annotation { "Feature Type Name" : "Feature", "Feature Type Description" : "" }
export const myFeature = defineFeature(function(context is Context, id is Id, definition is map)
    precondition{}
    {
        {
            var Q0;
            Q0=qCreatedBy(makeId("Front.planeOp"),FACE);
            var sketch = newSketch(context, id + "F0", { "sketchPlane" : qUnion([Q0])});
            skLineSegment(sketch, "E0.bottom", {"start": v(-63.5, 38.1) * mm, "end": v(63.5, 38.1) * mm});
            skLineSegment(sketch, "E0.top", {"start": v(-63.5, -38.1) * mm, "end": v(63.5, -38.1) * mm});
            skLineSegment(sketch, "E0.left", {"start": v(-63.5, 38.1) * mm, "end": v(-63.5, -38.1) * mm});
            skLineSegment(sketch, "E0.right", {"start": v(63.5, 38.1) * mm, "end": v(63.5, -38.1) * mm});
            skPoint(sketch, "E1", {"position": v(-57.15, 31.75) * mm});
            skPoint(sketch, "E2", {"position": v(57.15, 31.75) * mm});
            skPoint(sketch, "E3", {"position": v(57.15, -31.75) * mm});
            skPoint(sketch, "E4", {"position": v(-57.15, -31.75) * mm});
            skSolve(sketch);
        }
        {
            var Q0;
            Q0=makeQuery(id+"F0.imprint","IMPRINT",FACE,{"disambiguationData":[TD([[makeQuery(id+"F0.imprint","IMPRINT",EDGE,{"derivedFrom":sQuery(id+"F0.wireOp",EDGE,"E0.bottom")}),-1.0]])]});
            extrude(context, id + "F1", {"entities" : qUnion([Q0]), "depth" : 1.52 * mm});
        }
        {
            var Q0;
            Q0=makeQuery(id+"F1.opExtrude","CAP_FACE",FACE,{"disambiguationData":[OSD([sQuery(id+"F0.wireOp",EDGE,"E0.bottom"),sQuery(id+"F0.wireOp",EDGE,"E0.top"),sQuery(id+"F0.wireOp",EDGE,"E0.left"),sQuery(id+"F0.wireOp",EDGE,"E0.right")])],"isStart":false});
            var sketch = newSketch(context, id + "F2", { "sketchPlane" : qUnion([Q0])});
            skText(sketch, "E5", { "text": "DRIFTER II", "fontName": "OpenSans-Regular.ttf"});
            skLineSegment(sketch, "E6", {"start": v(0, 5.62) * mm, "end": v(0, -4.17) * mm, "construction": true});
            skText(sketch, "E7", { "text": "Rustler 36 designed by Holman and Pye", "fontName": "OpenSans-Regular.ttf"});
            skText(sketch, "E8", { "text": "Built by Orion Marine, Falmouth,England", "fontName": "OpenSans-Regular.ttf"});
            skText(sketch, "E9", { "text": "Fitted out by Paul Litton, Harold Greenslade\n", "fontName": "OpenSans-Regular.ttf"});
            skText(sketch, "E10", { "text": "and Walter Randolph to interior and \n\n", "fontName": "OpenSans-Regular.ttf"});
            skText(sketch, "E11", { "text": "extra rigging designs by Walter Randolph", "fontName": "OpenSans-Regular.ttf"});
            skText(sketch, "E12", { "text": "Launched August 1991", "fontName": "OpenSans-Regular.ttf"});
            skText(sketch, "E13", { "text": "Hull No. 40 - SSR 66775", "fontName": "OpenSans-Regular.ttf"});
            const initialGuessF2  = {"E5": [-0.02106, 0.02396, 1, 0, 0.00652], "E7": [-0.05139, 0.01598, 1, 0, 0.004], "E8": [-0.05248, 0.00799, 1, 0, 0.004], "E9": [-0.0566, 0, 1, 0, 0.004], "E10": [-0.04651, -0.00798, 1, 0, 0.00399], "E11": [-0.05278, -0.01595, 1, 0, 0.00399], "E12": [-0.02895, -0.03553, 1, 0, 0.00399], "E13": [-0.02999, -0.02756, 1, 0, 0.00399]};
            skSetInitialGuess(sketch, initialGuessF2);
            skSolve(sketch);
        }
        {
            var Q0;
            Q0=sQuery(id+"F0.wireOp",VERTEX,"E1");
            var Q1;
            Q1=sQuery(id+"F0.wireOp",VERTEX,"E2");
            var Q2;
            Q2=sQuery(id+"F0.wireOp",VERTEX,"E4");
            var Q3;
            Q3=sQuery(id+"F0.wireOp",VERTEX,"E3");
            var Q4;
            Q4=makeQuery(id+"F1.opExtrude","SWEPT_BODY",BODY,{"disambiguationData":[OSD([sQuery(id+"F0.wireOp",EDGE,"E0.bottom"),sQuery(id+"F0.wireOp",EDGE,"E0.top"),sQuery(id+"F0.wireOp",EDGE,"E0.left"),sQuery(id+"F0.wireOp",EDGE,"E0.right")])]});
            hole(context, id + "F3", {"style" : HoleStyle.SIMPLE, "endStyle" : HoleEndStyle.THROUGH, "oppositeDirection" : true, "holeDiameter" : 4 * mm, "isTappedThrough" : true, "tappedDepth" : 12.7 * mm, "tapClearance" : 0, "startFromSketch" : true, "locations" : qUnion([Q0, Q1, Q2, Q3]), "scope" : qUnion([Q4])});
        }
        {
            var Q0;
            Q0 = qSketchRegion(id + "F2", true);
            extrude(context, id + "F4", {"entities" : qUnion([Q0]), "oppositeDirection" : true, "offsetDistance" : 25.4 * mm, "depth" : 0.5 * mm});
        }
        {
            var Q0;
            Q0=makeQuery(id+"F4.opExtrude","SWEPT_BODY",BODY,{"disambiguationData":[OSD([sQuery(id+"F2.wireOp",EDGE,"E5.sketch_text.stroke-0"),sQuery(id+"F2.wireOp",EDGE,"E5.sketch_text.stroke-1"),sQuery(id+"F2.wireOp",EDGE,"E5.sketch_text.stroke-2"),sQuery(id+"F2.wireOp",EDGE,"E5.sketch_text.stroke-3"),sQuery(id+"F2.wireOp",EDGE,"E5.sketch_text.stroke-4"),sQuery(id+"F2.wireOp",EDGE,"E5.sketch_text.stroke-5"),sQuery(id+"F2.wireOp",EDGE,"E5.sketch_text.stroke-6"),sQuery(id+"F2.wireOp",EDGE,"E5.sketch_text.stroke-7"),sQuery(id+"F2.wireOp",EDGE,"E5.sketch_text.stroke-8"),sQuery(id+"F2.wireOp",EDGE,"E5.sketch_text.stroke-9"),sQuery(id+"F2.wireOp",EDGE,"E5.sketch_text.stroke-10"),sQuery(id+"F2.wireOp",EDGE,"E5.sketch_text.stroke-11"),sQuery(id+"F2.wireOp",EDGE,"E5.sketch_text.stroke-12"),sQuery(id+"F2.wireOp",EDGE,"E5.sketch_text.stroke-13")])]});
            var Q1;
            Q1=makeQuery(id+"F4.opExtrude","SWEPT_BODY",BODY,{"disambiguationData":[OSD([sQuery(id+"F2.wireOp",EDGE,"E13.sketch_text.stroke-246"),sQuery(id+"F2.wireOp",EDGE,"E13.sketch_text.stroke-247"),sQuery(id+"F2.wireOp",EDGE,"E13.sketch_text.stroke-248"),sQuery(id+"F2.wireOp",EDGE,"E13.sketch_text.stroke-249"),sQuery(id+"F2.wireOp",EDGE,"E13.sketch_text.stroke-250"),sQuery(id+"F2.wireOp",EDGE,"E13.sketch_text.stroke-251"),sQuery(id+"F2.wireOp",EDGE,"E13.sketch_text.stroke-252"),sQuery(id+"F2.wireOp",EDGE,"E13.sketch_text.stroke-253"),sQuery(id+"F2.wireOp",EDGE,"E13.sketch_text.stroke-254"),sQuery(id+"F2.wireOp",EDGE,"E13.sketch_text.stroke-255"),sQuery(id+"F2.wireOp",EDGE,"E13.sketch_text.stroke-256"),sQuery(id+"F2.wireOp",EDGE,"E13.sketch_text.stroke-257"),sQuery(id+"F2.wireOp",EDGE,"E13.sketch_text.stroke-258"),sQuery(id+"F2.wireOp",EDGE,"E13.sketch_text.stroke-259"),sQuery(id+"F2.wireOp",EDGE,"E13.sketch_text.stroke-260"),sQuery(id+"F2.wireOp",EDGE,"E13.sketch_text.stroke-261"),sQuery(id+"F2.wireOp",EDGE,"E13.sketch_text.stroke-262"),sQuery(id+"F2.wireOp",EDGE,"E13.sketch_text.stroke-263"),sQuery(id+"F2.wireOp",EDGE,"E13.sketch_text.stroke-264")])]});
            var Q2;
            Q2=makeQuery(id+"F4.opExtrude","SWEPT_BODY",BODY,{"disambiguationData":[OSD([sQuery(id+"F2.wireOp",EDGE,"E7.sketch_text.stroke-523"),sQuery(id+"F2.wireOp",EDGE,"E7.sketch_text.stroke-524"),sQuery(id+"F2.wireOp",EDGE,"E7.sketch_text.stroke-525"),sQuery(id+"F2.wireOp",EDGE,"E7.sketch_text.stroke-526"),sQuery(id+"F2.wireOp",EDGE,"E7.sketch_text.stroke-527"),sQuery(id+"F2.wireOp",EDGE,"E7.sketch_text.stroke-528"),sQuery(id+"F2.wireOp",EDGE,"E7.sketch_text.stroke-529"),sQuery(id+"F2.wireOp",EDGE,"E7.sketch_text.stroke-530"),sQuery(id+"F2.wireOp",EDGE,"E7.sketch_text.stroke-531"),sQuery(id+"F2.wireOp",EDGE,"E7.sketch_text.stroke-532"),sQuery(id+"F2.wireOp",EDGE,"E7.sketch_text.stroke-533"),sQuery(id+"F2.wireOp",EDGE,"E7.sketch_text.stroke-534"),sQuery(id+"F2.wireOp",EDGE,"E7.sketch_text.stroke-535"),sQuery(id+"F2.wireOp",EDGE,"E7.sketch_text.stroke-536"),sQuery(id+"F2.wireOp",EDGE,"E7.sketch_text.stroke-537"),sQuery(id+"F2.wireOp",EDGE,"E7.sketch_text.stroke-538"),sQuery(id+"F2.wireOp",EDGE,"E7.sketch_text.stroke-539")])]});
            var Q3;
            Q3=makeQuery(id+"F4.opExtrude","SWEPT_BODY",BODY,{"disambiguationData":[OSD([sQuery(id+"F2.wireOp",EDGE,"E7.sketch_text.stroke-540"),sQuery(id+"F2.wireOp",EDGE,"E7.sketch_text.stroke-541"),sQuery(id+"F2.wireOp",EDGE,"E7.sketch_text.stroke-542"),sQuery(id+"F2.wireOp",EDGE,"E7.sketch_text.stroke-543"),sQuery(id+"F2.wireOp",EDGE,"E7.sketch_text.stroke-544"),sQuery(id+"F2.wireOp",EDGE,"E7.sketch_text.stroke-545"),sQuery(id+"F2.wireOp",EDGE,"E7.sketch_text.stroke-546"),sQuery(id+"F2.wireOp",EDGE,"E7.sketch_text.stroke-547"),sQuery(id+"F2.wireOp",EDGE,"E7.sketch_text.stroke-548"),sQuery(id+"F2.wireOp",EDGE,"E7.sketch_text.stroke-549"),sQuery(id+"F2.wireOp",EDGE,"E7.sketch_text.stroke-550"),sQuery(id+"F2.wireOp",EDGE,"E7.sketch_text.stroke-551"),sQuery(id+"F2.wireOp",EDGE,"E7.sketch_text.stroke-552"),sQuery(id+"F2.wireOp",EDGE,"E7.sketch_text.stroke-553"),sQuery(id+"F2.wireOp",EDGE,"E7.sketch_text.stroke-554"),sQuery(id+"F2.wireOp",EDGE,"E7.sketch_text.stroke-555"),sQuery(id+"F2.wireOp",EDGE,"E7.sketch_text.stroke-556"),sQuery(id+"F2.wireOp",EDGE,"E7.sketch_text.stroke-557"),sQuery(id+"F2.wireOp",EDGE,"E7.sketch_text.stroke-558"),sQuery(id+"F2.wireOp",EDGE,"E7.sketch_text.stroke-559"),sQuery(id+"F2.wireOp",EDGE,"E7.sketch_text.stroke-560"),sQuery(id+"F2.wireOp",EDGE,"E7.sketch_text.stroke-561"),sQuery(id+"F2.wireOp",EDGE,"E7.sketch_text.stroke-562"),sQuery(id+"F2.wireOp",EDGE,"E7.sketch_text.stroke-563")])]});
            var Q4;
            Q4=makeQuery(id+"F4.opExtrude","SWEPT_BODY",BODY,{"disambiguationData":[OSD([sQuery(id+"F2.wireOp",EDGE,"E7.sketch_text.stroke-564"),sQuery(id+"F2.wireOp",EDGE,"E7.sketch_text.stroke-565"),sQuery(id+"F2.wireOp",EDGE,"E7.sketch_text.stroke-566"),sQuery(id+"F2.wireOp",EDGE,"E7.sketch_text.stroke-567"),sQuery(id+"F2.wireOp",EDGE,"E7.sketch_text.stroke-568"),sQuery(id+"F2.wireOp",EDGE,"E7.sketch_text.stroke-569"),sQuery(id+"F2.wireOp",EDGE,"E7.sketch_text.stroke-570"),sQuery(id+"F2.wireOp",EDGE,"E7.sketch_text.stroke-571"),sQuery(id+"F2.wireOp",EDGE,"E7.sketch_text.stroke-572"),sQuery(id+"F2.wireOp",EDGE,"E7.sketch_text.stroke-573"),sQuery(id+"F2.wireOp",EDGE,"E7.sketch_text.stroke-574"),sQuery(id+"F2.wireOp",EDGE,"E7.sketch_text.stroke-575"),sQuery(id+"F2.wireOp",EDGE,"E7.sketch_text.stroke-576"),sQuery(id+"F2.wireOp",EDGE,"E7.sketch_text.stroke-577"),sQuery(id+"F2.wireOp",EDGE,"E7.sketch_text.stroke-578")])]});
            var Q5;
            Q5=makeQuery(id+"F4.opExtrude","SWEPT_BODY",BODY,{"disambiguationData":[OSD([sQuery(id+"F2.wireOp",EDGE,"E7.sketch_text.stroke-579"),sQuery(id+"F2.wireOp",EDGE,"E7.sketch_text.stroke-580"),sQuery(id+"F2.wireOp",EDGE,"E7.sketch_text.stroke-581"),sQuery(id+"F2.wireOp",EDGE,"E7.sketch_text.stroke-582"),sQuery(id+"F2.wireOp",EDGE,"E7.sketch_text.stroke-583"),sQuery(id+"F2.wireOp",EDGE,"E7.sketch_text.stroke-584"),sQuery(id+"F2.wireOp",EDGE,"E7.sketch_text.stroke-585"),sQuery(id+"F2.wireOp",EDGE,"E7.sketch_text.stroke-586"),sQuery(id+"F2.wireOp",EDGE,"E7.sketch_text.stroke-587"),sQuery(id+"F2.wireOp",EDGE,"E7.sketch_text.stroke-588"),sQuery(id+"F2.wireOp",EDGE,"E7.sketch_text.stroke-589"),sQuery(id+"F2.wireOp",EDGE,"E7.sketch_text.stroke-590"),sQuery(id+"F2.wireOp",EDGE,"E7.sketch_text.stroke-591"),sQuery(id+"F2.wireOp",EDGE,"E7.sketch_text.stroke-592"),sQuery(id+"F2.wireOp",EDGE,"E7.sketch_text.stroke-593"),sQuery(id+"F2.wireOp",EDGE,"E7.sketch_text.stroke-594")])]});
            var Q6;
            Q6=makeQuery(id+"F4.opExtrude","SWEPT_BODY",BODY,{"disambiguationData":[OSD([sQuery(id+"F2.wireOp",EDGE,"E7.sketch_text.stroke-595"),sQuery(id+"F2.wireOp",EDGE,"E7.sketch_text.stroke-596"),sQuery(id+"F2.wireOp",EDGE,"E7.sketch_text.stroke-597"),sQuery(id+"F2.wireOp",EDGE,"E7.sketch_text.stroke-598"),sQuery(id+"F2.wireOp",EDGE,"E7.sketch_text.stroke-599"),sQuery(id+"F2.wireOp",EDGE,"E7.sketch_text.stroke-600"),sQuery(id+"F2.wireOp",EDGE,"E7.sketch_text.stroke-601"),sQuery(id+"F2.wireOp",EDGE,"E7.sketch_text.stroke-602"),sQuery(id+"F2.wireOp",EDGE,"E7.sketch_text.stroke-603"),sQuery(id+"F2.wireOp",EDGE,"E7.sketch_text.stroke-604"),sQuery(id+"F2.wireOp",EDGE,"E7.sketch_text.stroke-605"),sQuery(id+"F2.wireOp",EDGE,"E7.sketch_text.stroke-606"),sQuery(id+"F2.wireOp",EDGE,"E7.sketch_text.stroke-607"),sQuery(id+"F2.wireOp",EDGE,"E7.sketch_text.stroke-608"),sQuery(id+"F2.wireOp",EDGE,"E7.sketch_text.stroke-609"),sQuery(id+"F2.wireOp",EDGE,"E7.sketch_text.stroke-610"),sQuery(id+"F2.wireOp",EDGE,"E7.sketch_text.stroke-611"),sQuery(id+"F2.wireOp",EDGE,"E7.sketch_text.stroke-612"),sQuery(id+"F2.wireOp",EDGE,"E7.sketch_text.stroke-613")])]});
            var Q7;
            Q7=makeQuery(id+"F4.opExtrude","SWEPT_BODY",BODY,{"disambiguationData":[OSD([sQuery(id+"F2.wireOp",EDGE,"E8.sketch_text.stroke-0"),sQuery(id+"F2.wireOp",EDGE,"E8.sketch_text.stroke-1"),sQuery(id+"F2.wireOp",EDGE,"E8.sketch_text.stroke-2"),sQuery(id+"F2.wireOp",EDGE,"E8.sketch_text.stroke-3"),sQuery(id+"F2.wireOp",EDGE,"E8.sketch_text.stroke-4"),sQuery(id+"F2.wireOp",EDGE,"E8.sketch_text.stroke-5"),sQuery(id+"F2.wireOp",EDGE,"E8.sketch_text.stroke-6"),sQuery(id+"F2.wireOp",EDGE,"E8.sketch_text.stroke-7"),sQuery(id+"F2.wireOp",EDGE,"E8.sketch_text.stroke-8"),sQuery(id+"F2.wireOp",EDGE,"E8.sketch_text.stroke-9"),sQuery(id+"F2.wireOp",EDGE,"E8.sketch_text.stroke-10"),sQuery(id+"F2.wireOp",EDGE,"E8.sketch_text.stroke-11"),sQuery(id+"F2.wireOp",EDGE,"E8.sketch_text.stroke-12"),sQuery(id+"F2.wireOp",EDGE,"E8.sketch_text.stroke-13"),sQuery(id+"F2.wireOp",EDGE,"E8.sketch_text.stroke-14"),sQuery(id+"F2.wireOp",EDGE,"E8.sketch_text.stroke-15"),sQuery(id+"F2.wireOp",EDGE,"E8.sketch_text.stroke-16"),sQuery(id+"F2.wireOp",EDGE,"E8.sketch_text.stroke-17"),sQuery(id+"F2.wireOp",EDGE,"E8.sketch_text.stroke-18"),sQuery(id+"F2.wireOp",EDGE,"E8.sketch_text.stroke-19"),sQuery(id+"F2.wireOp",EDGE,"E8.sketch_text.stroke-20"),sQuery(id+"F2.wireOp",EDGE,"E8.sketch_text.stroke-21"),sQuery(id+"F2.wireOp",EDGE,"E8.sketch_text.stroke-22"),sQuery(id+"F2.wireOp",EDGE,"E8.sketch_text.stroke-23"),sQuery(id+"F2.wireOp",EDGE,"E8.sketch_text.stroke-24")])]});
            var Q8;
            Q8=makeQuery(id+"F4.opExtrude","SWEPT_BODY",BODY,{"disambiguationData":[OSD([sQuery(id+"F2.wireOp",EDGE,"E8.sketch_text.stroke-25"),sQuery(id+"F2.wireOp",EDGE,"E8.sketch_text.stroke-26"),sQuery(id+"F2.wireOp",EDGE,"E8.sketch_text.stroke-27"),sQuery(id+"F2.wireOp",EDGE,"E8.sketch_text.stroke-28"),sQuery(id+"F2.wireOp",EDGE,"E8.sketch_text.stroke-29"),sQuery(id+"F2.wireOp",EDGE,"E8.sketch_text.stroke-30"),sQuery(id+"F2.wireOp",EDGE,"E8.sketch_text.stroke-31"),sQuery(id+"F2.wireOp",EDGE,"E8.sketch_text.stroke-32"),sQuery(id+"F2.wireOp",EDGE,"E8.sketch_text.stroke-33"),sQuery(id+"F2.wireOp",EDGE,"E8.sketch_text.stroke-34"),sQuery(id+"F2.wireOp",EDGE,"E8.sketch_text.stroke-35"),sQuery(id+"F2.wireOp",EDGE,"E8.sketch_text.stroke-36"),sQuery(id+"F2.wireOp",EDGE,"E8.sketch_text.stroke-37"),sQuery(id+"F2.wireOp",EDGE,"E8.sketch_text.stroke-38"),sQuery(id+"F2.wireOp",EDGE,"E8.sketch_text.stroke-39"),sQuery(id+"F2.wireOp",EDGE,"E8.sketch_text.stroke-40"),sQuery(id+"F2.wireOp",EDGE,"E8.sketch_text.stroke-41")])]});
            var Q9;
            Q9=makeQuery(id+"F4.opExtrude","SWEPT_BODY",BODY,{"disambiguationData":[OSD([sQuery(id+"F2.wireOp",EDGE,"E8.sketch_text.stroke-42"),sQuery(id+"F2.wireOp",EDGE,"E8.sketch_text.stroke-43"),sQuery(id+"F2.wireOp",EDGE,"E8.sketch_text.stroke-44"),sQuery(id+"F2.wireOp",EDGE,"E8.sketch_text.stroke-45")])]});
            var Q10;
            Q10=makeQuery(id+"F4.opExtrude","SWEPT_BODY",BODY,{"disambiguationData":[OSD([sQuery(id+"F2.wireOp",EDGE,"E8.sketch_text.stroke-46"),sQuery(id+"F2.wireOp",EDGE,"E8.sketch_text.stroke-47"),sQuery(id+"F2.wireOp",EDGE,"E8.sketch_text.stroke-48"),sQuery(id+"F2.wireOp",EDGE,"E8.sketch_text.stroke-49"),sQuery(id+"F2.wireOp",EDGE,"E8.sketch_text.stroke-50"),sQuery(id+"F2.wireOp",EDGE,"E8.sketch_text.stroke-51"),sQuery(id+"F2.wireOp",EDGE,"E8.sketch_text.stroke-52"),sQuery(id+"F2.wireOp",EDGE,"E8.sketch_text.stroke-53")])]});
            var Q11;
            Q11=makeQuery(id+"F4.opExtrude","SWEPT_BODY",BODY,{"disambiguationData":[OSD([sQuery(id+"F2.wireOp",EDGE,"E8.sketch_text.stroke-54"),sQuery(id+"F2.wireOp",EDGE,"E8.sketch_text.stroke-55"),sQuery(id+"F2.wireOp",EDGE,"E8.sketch_text.stroke-56"),sQuery(id+"F2.wireOp",EDGE,"E8.sketch_text.stroke-57")])]});
            var Q12;
            Q12=makeQuery(id+"F4.opExtrude","SWEPT_BODY",BODY,{"disambiguationData":[OSD([sQuery(id+"F2.wireOp",EDGE,"E8.sketch_text.stroke-58"),sQuery(id+"F2.wireOp",EDGE,"E8.sketch_text.stroke-59"),sQuery(id+"F2.wireOp",EDGE,"E8.sketch_text.stroke-60"),sQuery(id+"F2.wireOp",EDGE,"E8.sketch_text.stroke-61"),sQuery(id+"F2.wireOp",EDGE,"E8.sketch_text.stroke-62"),sQuery(id+"F2.wireOp",EDGE,"E8.sketch_text.stroke-63"),sQuery(id+"F2.wireOp",EDGE,"E8.sketch_text.stroke-64"),sQuery(id+"F2.wireOp",EDGE,"E8.sketch_text.stroke-65"),sQuery(id+"F2.wireOp",EDGE,"E8.sketch_text.stroke-66"),sQuery(id+"F2.wireOp",EDGE,"E8.sketch_text.stroke-67"),sQuery(id+"F2.wireOp",EDGE,"E8.sketch_text.stroke-68"),sQuery(id+"F2.wireOp",EDGE,"E8.sketch_text.stroke-69"),sQuery(id+"F2.wireOp",EDGE,"E8.sketch_text.stroke-70"),sQuery(id+"F2.wireOp",EDGE,"E8.sketch_text.stroke-71"),sQuery(id+"F2.wireOp",EDGE,"E8.sketch_text.stroke-72"),sQuery(id+"F2.wireOp",EDGE,"E8.sketch_text.stroke-73"),sQuery(id+"F2.wireOp",EDGE,"E8.sketch_text.stroke-74"),sQuery(id+"F2.wireOp",EDGE,"E8.sketch_text.stroke-75"),sQuery(id+"F2.wireOp",EDGE,"E8.sketch_text.stroke-76")])]});
            var Q13;
            Q13=makeQuery(id+"F4.opExtrude","SWEPT_BODY",BODY,{"disambiguationData":[OSD([sQuery(id+"F2.wireOp",EDGE,"E8.sketch_text.stroke-77"),sQuery(id+"F2.wireOp",EDGE,"E8.sketch_text.stroke-78"),sQuery(id+"F2.wireOp",EDGE,"E8.sketch_text.stroke-79"),sQuery(id+"F2.wireOp",EDGE,"E8.sketch_text.stroke-80"),sQuery(id+"F2.wireOp",EDGE,"E8.sketch_text.stroke-81"),sQuery(id+"F2.wireOp",EDGE,"E8.sketch_text.stroke-82"),sQuery(id+"F2.wireOp",EDGE,"E8.sketch_text.stroke-83"),sQuery(id+"F2.wireOp",EDGE,"E8.sketch_text.stroke-84"),sQuery(id+"F2.wireOp",EDGE,"E8.sketch_text.stroke-85"),sQuery(id+"F2.wireOp",EDGE,"E8.sketch_text.stroke-86"),sQuery(id+"F2.wireOp",EDGE,"E8.sketch_text.stroke-87"),sQuery(id+"F2.wireOp",EDGE,"E8.sketch_text.stroke-88"),sQuery(id+"F2.wireOp",EDGE,"E8.sketch_text.stroke-89"),sQuery(id+"F2.wireOp",EDGE,"E8.sketch_text.stroke-90"),sQuery(id+"F2.wireOp",EDGE,"E8.sketch_text.stroke-91"),sQuery(id+"F2.wireOp",EDGE,"E8.sketch_text.stroke-92"),sQuery(id+"F2.wireOp",EDGE,"E8.sketch_text.stroke-93"),sQuery(id+"F2.wireOp",EDGE,"E8.sketch_text.stroke-94"),sQuery(id+"F2.wireOp",EDGE,"E8.sketch_text.stroke-95"),sQuery(id+"F2.wireOp",EDGE,"E8.sketch_text.stroke-96"),sQuery(id+"F2.wireOp",EDGE,"E8.sketch_text.stroke-97"),sQuery(id+"F2.wireOp",EDGE,"E8.sketch_text.stroke-98"),sQuery(id+"F2.wireOp",EDGE,"E8.sketch_text.stroke-99")])]});
            var Q14;
            Q14=makeQuery(id+"F4.opExtrude","SWEPT_BODY",BODY,{"disambiguationData":[OSD([sQuery(id+"F2.wireOp",EDGE,"E8.sketch_text.stroke-100"),sQuery(id+"F2.wireOp",EDGE,"E8.sketch_text.stroke-101"),sQuery(id+"F2.wireOp",EDGE,"E8.sketch_text.stroke-102"),sQuery(id+"F2.wireOp",EDGE,"E8.sketch_text.stroke-103"),sQuery(id+"F2.wireOp",EDGE,"E8.sketch_text.stroke-104"),sQuery(id+"F2.wireOp",EDGE,"E8.sketch_text.stroke-105"),sQuery(id+"F2.wireOp",EDGE,"E8.sketch_text.stroke-106"),sQuery(id+"F2.wireOp",EDGE,"E8.sketch_text.stroke-107"),sQuery(id+"F2.wireOp",EDGE,"E8.sketch_text.stroke-108"),sQuery(id+"F2.wireOp",EDGE,"E8.sketch_text.stroke-109"),sQuery(id+"F2.wireOp",EDGE,"E8.sketch_text.stroke-110"),sQuery(id+"F2.wireOp",EDGE,"E8.sketch_text.stroke-111"),sQuery(id+"F2.wireOp",EDGE,"E8.sketch_text.stroke-112"),sQuery(id+"F2.wireOp",EDGE,"E8.sketch_text.stroke-113"),sQuery(id+"F2.wireOp",EDGE,"E8.sketch_text.stroke-114"),sQuery(id+"F2.wireOp",EDGE,"E8.sketch_text.stroke-115")])]});
            var Q15;
            Q15=makeQuery(id+"F4.opExtrude","SWEPT_BODY",BODY,{"disambiguationData":[OSD([sQuery(id+"F2.wireOp",EDGE,"E8.sketch_text.stroke-116"),sQuery(id+"F2.wireOp",EDGE,"E8.sketch_text.stroke-117"),sQuery(id+"F2.wireOp",EDGE,"E8.sketch_text.stroke-118"),sQuery(id+"F2.wireOp",EDGE,"E8.sketch_text.stroke-119"),sQuery(id+"F2.wireOp",EDGE,"E8.sketch_text.stroke-120"),sQuery(id+"F2.wireOp",EDGE,"E8.sketch_text.stroke-121"),sQuery(id+"F2.wireOp",EDGE,"E8.sketch_text.stroke-122"),sQuery(id+"F2.wireOp",EDGE,"E8.sketch_text.stroke-123"),sQuery(id+"F2.wireOp",EDGE,"E8.sketch_text.stroke-124"),sQuery(id+"F2.wireOp",EDGE,"E8.sketch_text.stroke-125"),sQuery(id+"F2.wireOp",EDGE,"E8.sketch_text.stroke-126"),sQuery(id+"F2.wireOp",EDGE,"E8.sketch_text.stroke-127"),sQuery(id+"F2.wireOp",EDGE,"E8.sketch_text.stroke-128"),sQuery(id+"F2.wireOp",EDGE,"E8.sketch_text.stroke-129"),sQuery(id+"F2.wireOp",EDGE,"E8.sketch_text.stroke-130"),sQuery(id+"F2.wireOp",EDGE,"E8.sketch_text.stroke-131")])]});
            var Q16;
            Q16=makeQuery(id+"F4.opExtrude","SWEPT_BODY",BODY,{"disambiguationData":[OSD([sQuery(id+"F2.wireOp",EDGE,"E8.sketch_text.stroke-132"),sQuery(id+"F2.wireOp",EDGE,"E8.sketch_text.stroke-133"),sQuery(id+"F2.wireOp",EDGE,"E8.sketch_text.stroke-134"),sQuery(id+"F2.wireOp",EDGE,"E8.sketch_text.stroke-135"),sQuery(id+"F2.wireOp",EDGE,"E8.sketch_text.stroke-136"),sQuery(id+"F2.wireOp",EDGE,"E8.sketch_text.stroke-137"),sQuery(id+"F2.wireOp",EDGE,"E8.sketch_text.stroke-138"),sQuery(id+"F2.wireOp",EDGE,"E8.sketch_text.stroke-139"),sQuery(id+"F2.wireOp",EDGE,"E8.sketch_text.stroke-140"),sQuery(id+"F2.wireOp",EDGE,"E8.sketch_text.stroke-141"),sQuery(id+"F2.wireOp",EDGE,"E8.sketch_text.stroke-142"),sQuery(id+"F2.wireOp",EDGE,"E8.sketch_text.stroke-143"),sQuery(id+"F2.wireOp",EDGE,"E8.sketch_text.stroke-144")])]});
            var Q17;
            Q17=makeQuery(id+"F4.opExtrude","SWEPT_BODY",BODY,{"disambiguationData":[OSD([sQuery(id+"F2.wireOp",EDGE,"E8.sketch_text.stroke-145"),sQuery(id+"F2.wireOp",EDGE,"E8.sketch_text.stroke-146"),sQuery(id+"F2.wireOp",EDGE,"E8.sketch_text.stroke-147"),sQuery(id+"F2.wireOp",EDGE,"E8.sketch_text.stroke-148")])]});
            var Q18;
            Q18=makeQuery(id+"F4.opExtrude","SWEPT_BODY",BODY,{"disambiguationData":[OSD([sQuery(id+"F2.wireOp",EDGE,"E8.sketch_text.stroke-149"),sQuery(id+"F2.wireOp",EDGE,"E8.sketch_text.stroke-150"),sQuery(id+"F2.wireOp",EDGE,"E8.sketch_text.stroke-151"),sQuery(id+"F2.wireOp",EDGE,"E8.sketch_text.stroke-152"),sQuery(id+"F2.wireOp",EDGE,"E8.sketch_text.stroke-153"),sQuery(id+"F2.wireOp",EDGE,"E8.sketch_text.stroke-154"),sQuery(id+"F2.wireOp",EDGE,"E8.sketch_text.stroke-155"),sQuery(id+"F2.wireOp",EDGE,"E8.sketch_text.stroke-156")])]});
            var Q19;
            Q19=makeQuery(id+"F4.opExtrude","SWEPT_BODY",BODY,{"disambiguationData":[OSD([sQuery(id+"F2.wireOp",EDGE,"E8.sketch_text.stroke-157"),sQuery(id+"F2.wireOp",EDGE,"E8.sketch_text.stroke-158"),sQuery(id+"F2.wireOp",EDGE,"E8.sketch_text.stroke-159"),sQuery(id+"F2.wireOp",EDGE,"E8.sketch_text.stroke-160"),sQuery(id+"F2.wireOp",EDGE,"E8.sketch_text.stroke-161"),sQuery(id+"F2.wireOp",EDGE,"E8.sketch_text.stroke-162"),sQuery(id+"F2.wireOp",EDGE,"E8.sketch_text.stroke-163"),sQuery(id+"F2.wireOp",EDGE,"E8.sketch_text.stroke-164"),sQuery(id+"F2.wireOp",EDGE,"E8.sketch_text.stroke-165"),sQuery(id+"F2.wireOp",EDGE,"E8.sketch_text.stroke-166"),sQuery(id+"F2.wireOp",EDGE,"E8.sketch_text.stroke-167"),sQuery(id+"F2.wireOp",EDGE,"E8.sketch_text.stroke-168"),sQuery(id+"F2.wireOp",EDGE,"E8.sketch_text.stroke-169"),sQuery(id+"F2.wireOp",EDGE,"E8.sketch_text.stroke-170"),sQuery(id+"F2.wireOp",EDGE,"E8.sketch_text.stroke-171"),sQuery(id+"F2.wireOp",EDGE,"E8.sketch_text.stroke-172"),sQuery(id+"F2.wireOp",EDGE,"E8.sketch_text.stroke-173")])]});
            var Q20;
            Q20=makeQuery(id+"F4.opExtrude","SWEPT_BODY",BODY,{"disambiguationData":[OSD([sQuery(id+"F2.wireOp",EDGE,"E8.sketch_text.stroke-174"),sQuery(id+"F2.wireOp",EDGE,"E8.sketch_text.stroke-175"),sQuery(id+"F2.wireOp",EDGE,"E8.sketch_text.stroke-176"),sQuery(id+"F2.wireOp",EDGE,"E8.sketch_text.stroke-177"),sQuery(id+"F2.wireOp",EDGE,"E8.sketch_text.stroke-178"),sQuery(id+"F2.wireOp",EDGE,"E8.sketch_text.stroke-179"),sQuery(id+"F2.wireOp",EDGE,"E8.sketch_text.stroke-180"),sQuery(id+"F2.wireOp",EDGE,"E8.sketch_text.stroke-181"),sQuery(id+"F2.wireOp",EDGE,"E8.sketch_text.stroke-182"),sQuery(id+"F2.wireOp",EDGE,"E8.sketch_text.stroke-183"),sQuery(id+"F2.wireOp",EDGE,"E8.sketch_text.stroke-184"),sQuery(id+"F2.wireOp",EDGE,"E8.sketch_text.stroke-185"),sQuery(id+"F2.wireOp",EDGE,"E8.sketch_text.stroke-186"),sQuery(id+"F2.wireOp",EDGE,"E8.sketch_text.stroke-187"),sQuery(id+"F2.wireOp",EDGE,"E8.sketch_text.stroke-188"),sQuery(id+"F2.wireOp",EDGE,"E8.sketch_text.stroke-189"),sQuery(id+"F2.wireOp",EDGE,"E8.sketch_text.stroke-190")])]});
            var Q21;
            Q21=makeQuery(id+"F4.opExtrude","SWEPT_BODY",BODY,{"disambiguationData":[OSD([sQuery(id+"F2.wireOp",EDGE,"E8.sketch_text.stroke-191"),sQuery(id+"F2.wireOp",EDGE,"E8.sketch_text.stroke-192"),sQuery(id+"F2.wireOp",EDGE,"E8.sketch_text.stroke-193"),sQuery(id+"F2.wireOp",EDGE,"E8.sketch_text.stroke-194"),sQuery(id+"F2.wireOp",EDGE,"E8.sketch_text.stroke-195"),sQuery(id+"F2.wireOp",EDGE,"E8.sketch_text.stroke-196"),sQuery(id+"F2.wireOp",EDGE,"E8.sketch_text.stroke-197"),sQuery(id+"F2.wireOp",EDGE,"E8.sketch_text.stroke-198"),sQuery(id+"F2.wireOp",EDGE,"E8.sketch_text.stroke-199"),sQuery(id+"F2.wireOp",EDGE,"E8.sketch_text.stroke-200"),sQuery(id+"F2.wireOp",EDGE,"E8.sketch_text.stroke-201"),sQuery(id+"F2.wireOp",EDGE,"E8.sketch_text.stroke-202"),sQuery(id+"F2.wireOp",EDGE,"E8.sketch_text.stroke-203"),sQuery(id+"F2.wireOp",EDGE,"E8.sketch_text.stroke-204"),sQuery(id+"F2.wireOp",EDGE,"E8.sketch_text.stroke-205"),sQuery(id+"F2.wireOp",EDGE,"E8.sketch_text.stroke-206"),sQuery(id+"F2.wireOp",EDGE,"E8.sketch_text.stroke-207"),sQuery(id+"F2.wireOp",EDGE,"E8.sketch_text.stroke-208")])]});
            var Q22;
            Q22=makeQuery(id+"F4.opExtrude","SWEPT_BODY",BODY,{"disambiguationData":[OSD([sQuery(id+"F2.wireOp",EDGE,"E8.sketch_text.stroke-209"),sQuery(id+"F2.wireOp",EDGE,"E8.sketch_text.stroke-210"),sQuery(id+"F2.wireOp",EDGE,"E8.sketch_text.stroke-211"),sQuery(id+"F2.wireOp",EDGE,"E8.sketch_text.stroke-212"),sQuery(id+"F2.wireOp",EDGE,"E8.sketch_text.stroke-213"),sQuery(id+"F2.wireOp",EDGE,"E8.sketch_text.stroke-214"),sQuery(id+"F2.wireOp",EDGE,"E8.sketch_text.stroke-215"),sQuery(id+"F2.wireOp",EDGE,"E8.sketch_text.stroke-216"),sQuery(id+"F2.wireOp",EDGE,"E8.sketch_text.stroke-217"),sQuery(id+"F2.wireOp",EDGE,"E8.sketch_text.stroke-218"),sQuery(id+"F2.wireOp",EDGE,"E8.sketch_text.stroke-219"),sQuery(id+"F2.wireOp",EDGE,"E8.sketch_text.stroke-220"),sQuery(id+"F2.wireOp",EDGE,"E8.sketch_text.stroke-221"),sQuery(id+"F2.wireOp",EDGE,"E8.sketch_text.stroke-222"),sQuery(id+"F2.wireOp",EDGE,"E8.sketch_text.stroke-223"),sQuery(id+"F2.wireOp",EDGE,"E8.sketch_text.stroke-224"),sQuery(id+"F2.wireOp",EDGE,"E8.sketch_text.stroke-225"),sQuery(id+"F2.wireOp",EDGE,"E8.sketch_text.stroke-226"),sQuery(id+"F2.wireOp",EDGE,"E8.sketch_text.stroke-227"),sQuery(id+"F2.wireOp",EDGE,"E8.sketch_text.stroke-228"),sQuery(id+"F2.wireOp",EDGE,"E8.sketch_text.stroke-229"),sQuery(id+"F2.wireOp",EDGE,"E8.sketch_text.stroke-230"),sQuery(id+"F2.wireOp",EDGE,"E8.sketch_text.stroke-231"),sQuery(id+"F2.wireOp",EDGE,"E8.sketch_text.stroke-232"),sQuery(id+"F2.wireOp",EDGE,"E8.sketch_text.stroke-233"),sQuery(id+"F2.wireOp",EDGE,"E8.sketch_text.stroke-234"),sQuery(id+"F2.wireOp",EDGE,"E8.sketch_text.stroke-235")])]});
            var Q23;
            Q23=makeQuery(id+"F4.opExtrude","SWEPT_BODY",BODY,{"disambiguationData":[OSD([sQuery(id+"F2.wireOp",EDGE,"E8.sketch_text.stroke-236"),sQuery(id+"F2.wireOp",EDGE,"E8.sketch_text.stroke-237"),sQuery(id+"F2.wireOp",EDGE,"E8.sketch_text.stroke-238"),sQuery(id+"F2.wireOp",EDGE,"E8.sketch_text.stroke-239"),sQuery(id+"F2.wireOp",EDGE,"E8.sketch_text.stroke-240"),sQuery(id+"F2.wireOp",EDGE,"E8.sketch_text.stroke-241"),sQuery(id+"F2.wireOp",EDGE,"E8.sketch_text.stroke-242"),sQuery(id+"F2.wireOp",EDGE,"E8.sketch_text.stroke-243"),sQuery(id+"F2.wireOp",EDGE,"E8.sketch_text.stroke-244"),sQuery(id+"F2.wireOp",EDGE,"E8.sketch_text.stroke-245"),sQuery(id+"F2.wireOp",EDGE,"E8.sketch_text.stroke-246"),sQuery(id+"F2.wireOp",EDGE,"E8.sketch_text.stroke-247"),sQuery(id+"F2.wireOp",EDGE,"E8.sketch_text.stroke-248")])]});
            var Q24;
            Q24=makeQuery(id+"F4.opExtrude","SWEPT_BODY",BODY,{"disambiguationData":[OSD([sQuery(id+"F2.wireOp",EDGE,"E8.sketch_text.stroke-249"),sQuery(id+"F2.wireOp",EDGE,"E8.sketch_text.stroke-250"),sQuery(id+"F2.wireOp",EDGE,"E8.sketch_text.stroke-251"),sQuery(id+"F2.wireOp",EDGE,"E8.sketch_text.stroke-252")])]});
            var Q25;
            Q25=makeQuery(id+"F4.opExtrude","SWEPT_BODY",BODY,{"disambiguationData":[OSD([sQuery(id+"F2.wireOp",EDGE,"E8.sketch_text.stroke-253"),sQuery(id+"F2.wireOp",EDGE,"E8.sketch_text.stroke-254"),sQuery(id+"F2.wireOp",EDGE,"E8.sketch_text.stroke-255"),sQuery(id+"F2.wireOp",EDGE,"E8.sketch_text.stroke-256"),sQuery(id+"F2.wireOp",EDGE,"E8.sketch_text.stroke-257"),sQuery(id+"F2.wireOp",EDGE,"E8.sketch_text.stroke-258"),sQuery(id+"F2.wireOp",EDGE,"E8.sketch_text.stroke-259"),sQuery(id+"F2.wireOp",EDGE,"E8.sketch_text.stroke-260")])]});
            var Q26;
            Q26=makeQuery(id+"F4.opExtrude","SWEPT_BODY",BODY,{"disambiguationData":[OSD([sQuery(id+"F2.wireOp",EDGE,"E8.sketch_text.stroke-261"),sQuery(id+"F2.wireOp",EDGE,"E8.sketch_text.stroke-262"),sQuery(id+"F2.wireOp",EDGE,"E8.sketch_text.stroke-263"),sQuery(id+"F2.wireOp",EDGE,"E8.sketch_text.stroke-264"),sQuery(id+"F2.wireOp",EDGE,"E8.sketch_text.stroke-265"),sQuery(id+"F2.wireOp",EDGE,"E8.sketch_text.stroke-266"),sQuery(id+"F2.wireOp",EDGE,"E8.sketch_text.stroke-267"),sQuery(id+"F2.wireOp",EDGE,"E8.sketch_text.stroke-268"),sQuery(id+"F2.wireOp",EDGE,"E8.sketch_text.stroke-269"),sQuery(id+"F2.wireOp",EDGE,"E8.sketch_text.stroke-270"),sQuery(id+"F2.wireOp",EDGE,"E8.sketch_text.stroke-271"),sQuery(id+"F2.wireOp",EDGE,"E8.sketch_text.stroke-272"),sQuery(id+"F2.wireOp",EDGE,"E8.sketch_text.stroke-273"),sQuery(id+"F2.wireOp",EDGE,"E8.sketch_text.stroke-274"),sQuery(id+"F2.wireOp",EDGE,"E8.sketch_text.stroke-275"),sQuery(id+"F2.wireOp",EDGE,"E8.sketch_text.stroke-276"),sQuery(id+"F2.wireOp",EDGE,"E8.sketch_text.stroke-277")])]});
            var Q27;
            Q27=makeQuery(id+"F4.opExtrude","SWEPT_BODY",BODY,{"disambiguationData":[OSD([sQuery(id+"F2.wireOp",EDGE,"E8.sketch_text.stroke-278"),sQuery(id+"F2.wireOp",EDGE,"E8.sketch_text.stroke-279"),sQuery(id+"F2.wireOp",EDGE,"E8.sketch_text.stroke-280"),sQuery(id+"F2.wireOp",EDGE,"E8.sketch_text.stroke-281"),sQuery(id+"F2.wireOp",EDGE,"E8.sketch_text.stroke-282"),sQuery(id+"F2.wireOp",EDGE,"E8.sketch_text.stroke-283"),sQuery(id+"F2.wireOp",EDGE,"E8.sketch_text.stroke-284"),sQuery(id+"F2.wireOp",EDGE,"E8.sketch_text.stroke-285"),sQuery(id+"F2.wireOp",EDGE,"E8.sketch_text.stroke-286"),sQuery(id+"F2.wireOp",EDGE,"E8.sketch_text.stroke-287"),sQuery(id+"F2.wireOp",EDGE,"E8.sketch_text.stroke-288"),sQuery(id+"F2.wireOp",EDGE,"E8.sketch_text.stroke-289"),sQuery(id+"F2.wireOp",EDGE,"E8.sketch_text.stroke-290"),sQuery(id+"F2.wireOp",EDGE,"E8.sketch_text.stroke-291"),sQuery(id+"F2.wireOp",EDGE,"E8.sketch_text.stroke-292"),sQuery(id+"F2.wireOp",EDGE,"E8.sketch_text.stroke-293"),sQuery(id+"F2.wireOp",EDGE,"E8.sketch_text.stroke-294"),sQuery(id+"F2.wireOp",EDGE,"E8.sketch_text.stroke-295"),sQuery(id+"F2.wireOp",EDGE,"E8.sketch_text.stroke-296")])]});
            var Q28;
            Q28=makeQuery(id+"F4.opExtrude","SWEPT_BODY",BODY,{"disambiguationData":[OSD([sQuery(id+"F2.wireOp",EDGE,"E8.sketch_text.stroke-297"),sQuery(id+"F2.wireOp",EDGE,"E8.sketch_text.stroke-298"),sQuery(id+"F2.wireOp",EDGE,"E8.sketch_text.stroke-299"),sQuery(id+"F2.wireOp",EDGE,"E8.sketch_text.stroke-300"),sQuery(id+"F2.wireOp",EDGE,"E8.sketch_text.stroke-301"),sQuery(id+"F2.wireOp",EDGE,"E8.sketch_text.stroke-302"),sQuery(id+"F2.wireOp",EDGE,"E8.sketch_text.stroke-303")])]});
            var Q29;
            Q29=makeQuery(id+"F4.opExtrude","SWEPT_BODY",BODY,{"disambiguationData":[OSD([sQuery(id+"F2.wireOp",EDGE,"E8.sketch_text.stroke-304"),sQuery(id+"F2.wireOp",EDGE,"E8.sketch_text.stroke-305"),sQuery(id+"F2.wireOp",EDGE,"E8.sketch_text.stroke-306"),sQuery(id+"F2.wireOp",EDGE,"E8.sketch_text.stroke-307"),sQuery(id+"F2.wireOp",EDGE,"E8.sketch_text.stroke-308"),sQuery(id+"F2.wireOp",EDGE,"E8.sketch_text.stroke-309"),sQuery(id+"F2.wireOp",EDGE,"E8.sketch_text.stroke-310"),sQuery(id+"F2.wireOp",EDGE,"E8.sketch_text.stroke-311"),sQuery(id+"F2.wireOp",EDGE,"E8.sketch_text.stroke-312"),sQuery(id+"F2.wireOp",EDGE,"E8.sketch_text.stroke-313")])]});
            var Q30;
            Q30=makeQuery(id+"F4.opExtrude","SWEPT_BODY",BODY,{"disambiguationData":[OSD([sQuery(id+"F2.wireOp",EDGE,"E8.sketch_text.stroke-314"),sQuery(id+"F2.wireOp",EDGE,"E8.sketch_text.stroke-315"),sQuery(id+"F2.wireOp",EDGE,"E8.sketch_text.stroke-316"),sQuery(id+"F2.wireOp",EDGE,"E8.sketch_text.stroke-317"),sQuery(id+"F2.wireOp",EDGE,"E8.sketch_text.stroke-318"),sQuery(id+"F2.wireOp",EDGE,"E8.sketch_text.stroke-319"),sQuery(id+"F2.wireOp",EDGE,"E8.sketch_text.stroke-320"),sQuery(id+"F2.wireOp",EDGE,"E8.sketch_text.stroke-321"),sQuery(id+"F2.wireOp",EDGE,"E8.sketch_text.stroke-322"),sQuery(id+"F2.wireOp",EDGE,"E8.sketch_text.stroke-323"),sQuery(id+"F2.wireOp",EDGE,"E8.sketch_text.stroke-324"),sQuery(id+"F2.wireOp",EDGE,"E8.sketch_text.stroke-325"),sQuery(id+"F2.wireOp",EDGE,"E8.sketch_text.stroke-326"),sQuery(id+"F2.wireOp",EDGE,"E8.sketch_text.stroke-327"),sQuery(id+"F2.wireOp",EDGE,"E8.sketch_text.stroke-328"),sQuery(id+"F2.wireOp",EDGE,"E8.sketch_text.stroke-329"),sQuery(id+"F2.wireOp",EDGE,"E8.sketch_text.stroke-330"),sQuery(id+"F2.wireOp",EDGE,"E8.sketch_text.stroke-331"),sQuery(id+"F2.wireOp",EDGE,"E8.sketch_text.stroke-332"),sQuery(id+"F2.wireOp",EDGE,"E8.sketch_text.stroke-333"),sQuery(id+"F2.wireOp",EDGE,"E8.sketch_text.stroke-334"),sQuery(id+"F2.wireOp",EDGE,"E8.sketch_text.stroke-335"),sQuery(id+"F2.wireOp",EDGE,"E8.sketch_text.stroke-336"),sQuery(id+"F2.wireOp",EDGE,"E8.sketch_text.stroke-337"),sQuery(id+"F2.wireOp",EDGE,"E8.sketch_text.stroke-338"),sQuery(id+"F2.wireOp",EDGE,"E8.sketch_text.stroke-339"),sQuery(id+"F2.wireOp",EDGE,"E8.sketch_text.stroke-340")])]});
            var Q31;
            Q31=makeQuery(id+"F4.opExtrude","SWEPT_BODY",BODY,{"disambiguationData":[OSD([sQuery(id+"F2.wireOp",EDGE,"E8.sketch_text.stroke-341"),sQuery(id+"F2.wireOp",EDGE,"E8.sketch_text.stroke-342"),sQuery(id+"F2.wireOp",EDGE,"E8.sketch_text.stroke-343"),sQuery(id+"F2.wireOp",EDGE,"E8.sketch_text.stroke-344")])]});
            var Q32;
            Q32=makeQuery(id+"F4.opExtrude","SWEPT_BODY",BODY,{"disambiguationData":[OSD([sQuery(id+"F2.wireOp",EDGE,"E8.sketch_text.stroke-345"),sQuery(id+"F2.wireOp",EDGE,"E8.sketch_text.stroke-346"),sQuery(id+"F2.wireOp",EDGE,"E8.sketch_text.stroke-347"),sQuery(id+"F2.wireOp",EDGE,"E8.sketch_text.stroke-348"),sQuery(id+"F2.wireOp",EDGE,"E8.sketch_text.stroke-349"),sQuery(id+"F2.wireOp",EDGE,"E8.sketch_text.stroke-350"),sQuery(id+"F2.wireOp",EDGE,"E8.sketch_text.stroke-351"),sQuery(id+"F2.wireOp",EDGE,"E8.sketch_text.stroke-352"),sQuery(id+"F2.wireOp",EDGE,"E8.sketch_text.stroke-353"),sQuery(id+"F2.wireOp",EDGE,"E8.sketch_text.stroke-354"),sQuery(id+"F2.wireOp",EDGE,"E8.sketch_text.stroke-355"),sQuery(id+"F2.wireOp",EDGE,"E8.sketch_text.stroke-356"),sQuery(id+"F2.wireOp",EDGE,"E8.sketch_text.stroke-357"),sQuery(id+"F2.wireOp",EDGE,"E8.sketch_text.stroke-358"),sQuery(id+"F2.wireOp",EDGE,"E8.sketch_text.stroke-359"),sQuery(id+"F2.wireOp",EDGE,"E8.sketch_text.stroke-360"),sQuery(id+"F2.wireOp",EDGE,"E8.sketch_text.stroke-361"),sQuery(id+"F2.wireOp",EDGE,"E8.sketch_text.stroke-362"),sQuery(id+"F2.wireOp",EDGE,"E8.sketch_text.stroke-363"),sQuery(id+"F2.wireOp",EDGE,"E8.sketch_text.stroke-364"),sQuery(id+"F2.wireOp",EDGE,"E8.sketch_text.stroke-365"),sQuery(id+"F2.wireOp",EDGE,"E8.sketch_text.stroke-366"),sQuery(id+"F2.wireOp",EDGE,"E8.sketch_text.stroke-367"),sQuery(id+"F2.wireOp",EDGE,"E8.sketch_text.stroke-368"),sQuery(id+"F2.wireOp",EDGE,"E8.sketch_text.stroke-369"),sQuery(id+"F2.wireOp",EDGE,"E8.sketch_text.stroke-370"),sQuery(id+"F2.wireOp",EDGE,"E8.sketch_text.stroke-371"),sQuery(id+"F2.wireOp",EDGE,"E8.sketch_text.stroke-372")])]});
            var Q33;
            Q33=makeQuery(id+"F4.opExtrude","SWEPT_BODY",BODY,{"disambiguationData":[OSD([sQuery(id+"F2.wireOp",EDGE,"E8.sketch_text.stroke-373"),sQuery(id+"F2.wireOp",EDGE,"E8.sketch_text.stroke-374"),sQuery(id+"F2.wireOp",EDGE,"E8.sketch_text.stroke-375"),sQuery(id+"F2.wireOp",EDGE,"E8.sketch_text.stroke-376"),sQuery(id+"F2.wireOp",EDGE,"E8.sketch_text.stroke-377"),sQuery(id+"F2.wireOp",EDGE,"E8.sketch_text.stroke-378"),sQuery(id+"F2.wireOp",EDGE,"E8.sketch_text.stroke-379"),sQuery(id+"F2.wireOp",EDGE,"E8.sketch_text.stroke-380"),sQuery(id+"F2.wireOp",EDGE,"E8.sketch_text.stroke-381"),sQuery(id+"F2.wireOp",EDGE,"E8.sketch_text.stroke-382"),sQuery(id+"F2.wireOp",EDGE,"E8.sketch_text.stroke-383"),sQuery(id+"F2.wireOp",EDGE,"E8.sketch_text.stroke-384"),sQuery(id+"F2.wireOp",EDGE,"E8.sketch_text.stroke-385"),sQuery(id+"F2.wireOp",EDGE,"E8.sketch_text.stroke-386"),sQuery(id+"F2.wireOp",EDGE,"E8.sketch_text.stroke-387"),sQuery(id+"F2.wireOp",EDGE,"E8.sketch_text.stroke-388"),sQuery(id+"F2.wireOp",EDGE,"E8.sketch_text.stroke-389")])]});
            var Q34;
            Q34=makeQuery(id+"F4.opExtrude","SWEPT_BODY",BODY,{"disambiguationData":[OSD([sQuery(id+"F2.wireOp",EDGE,"E8.sketch_text.stroke-390"),sQuery(id+"F2.wireOp",EDGE,"E8.sketch_text.stroke-391"),sQuery(id+"F2.wireOp",EDGE,"E8.sketch_text.stroke-392"),sQuery(id+"F2.wireOp",EDGE,"E8.sketch_text.stroke-393"),sQuery(id+"F2.wireOp",EDGE,"E8.sketch_text.stroke-394"),sQuery(id+"F2.wireOp",EDGE,"E8.sketch_text.stroke-395"),sQuery(id+"F2.wireOp",EDGE,"E8.sketch_text.stroke-396"),sQuery(id+"F2.wireOp",EDGE,"E8.sketch_text.stroke-397"),sQuery(id+"F2.wireOp",EDGE,"E8.sketch_text.stroke-398"),sQuery(id+"F2.wireOp",EDGE,"E8.sketch_text.stroke-399"),sQuery(id+"F2.wireOp",EDGE,"E8.sketch_text.stroke-400"),sQuery(id+"F2.wireOp",EDGE,"E8.sketch_text.stroke-401"),sQuery(id+"F2.wireOp",EDGE,"E8.sketch_text.stroke-402"),sQuery(id+"F2.wireOp",EDGE,"E8.sketch_text.stroke-403"),sQuery(id+"F2.wireOp",EDGE,"E8.sketch_text.stroke-404"),sQuery(id+"F2.wireOp",EDGE,"E8.sketch_text.stroke-405"),sQuery(id+"F2.wireOp",EDGE,"E8.sketch_text.stroke-406")])]});
            var Q35;
            Q35=makeQuery(id+"F4.opExtrude","SWEPT_BODY",BODY,{"disambiguationData":[OSD([sQuery(id+"F2.wireOp",EDGE,"E8.sketch_text.stroke-407"),sQuery(id+"F2.wireOp",EDGE,"E8.sketch_text.stroke-408"),sQuery(id+"F2.wireOp",EDGE,"E8.sketch_text.stroke-409"),sQuery(id+"F2.wireOp",EDGE,"E8.sketch_text.stroke-410"),sQuery(id+"F2.wireOp",EDGE,"E8.sketch_text.stroke-411"),sQuery(id+"F2.wireOp",EDGE,"E8.sketch_text.stroke-412"),sQuery(id+"F2.wireOp",EDGE,"E8.sketch_text.stroke-413"),sQuery(id+"F2.wireOp",EDGE,"E8.sketch_text.stroke-414"),sQuery(id+"F2.wireOp",EDGE,"E8.sketch_text.stroke-415"),sQuery(id+"F2.wireOp",EDGE,"E8.sketch_text.stroke-416"),sQuery(id+"F2.wireOp",EDGE,"E8.sketch_text.stroke-417"),sQuery(id+"F2.wireOp",EDGE,"E8.sketch_text.stroke-418"),sQuery(id+"F2.wireOp",EDGE,"E8.sketch_text.stroke-419"),sQuery(id+"F2.wireOp",EDGE,"E8.sketch_text.stroke-420"),sQuery(id+"F2.wireOp",EDGE,"E8.sketch_text.stroke-421"),sQuery(id+"F2.wireOp",EDGE,"E8.sketch_text.stroke-422"),sQuery(id+"F2.wireOp",EDGE,"E8.sketch_text.stroke-423"),sQuery(id+"F2.wireOp",EDGE,"E8.sketch_text.stroke-424"),sQuery(id+"F2.wireOp",EDGE,"E8.sketch_text.stroke-425")])]});
            var Q36;
            Q36=makeQuery(id+"F4.opExtrude","SWEPT_BODY",BODY,{"disambiguationData":[OSD([sQuery(id+"F2.wireOp",EDGE,"E8.sketch_text.stroke-426"),sQuery(id+"F2.wireOp",EDGE,"E8.sketch_text.stroke-427"),sQuery(id+"F2.wireOp",EDGE,"E8.sketch_text.stroke-428"),sQuery(id+"F2.wireOp",EDGE,"E8.sketch_text.stroke-429"),sQuery(id+"F2.wireOp",EDGE,"E8.sketch_text.stroke-430"),sQuery(id+"F2.wireOp",EDGE,"E8.sketch_text.stroke-431"),sQuery(id+"F2.wireOp",EDGE,"E8.sketch_text.stroke-432"),sQuery(id+"F2.wireOp",EDGE,"E8.sketch_text.stroke-433"),sQuery(id+"F2.wireOp",EDGE,"E8.sketch_text.stroke-434"),sQuery(id+"F2.wireOp",EDGE,"E8.sketch_text.stroke-435"),sQuery(id+"F2.wireOp",EDGE,"E8.sketch_text.stroke-436"),sQuery(id+"F2.wireOp",EDGE,"E8.sketch_text.stroke-437"),sQuery(id+"F2.wireOp",EDGE,"E8.sketch_text.stroke-438"),sQuery(id+"F2.wireOp",EDGE,"E8.sketch_text.stroke-439"),sQuery(id+"F2.wireOp",EDGE,"E8.sketch_text.stroke-440"),sQuery(id+"F2.wireOp",EDGE,"E8.sketch_text.stroke-441"),sQuery(id+"F2.wireOp",EDGE,"E8.sketch_text.stroke-442"),sQuery(id+"F2.wireOp",EDGE,"E8.sketch_text.stroke-443")])]});
            var Q37;
            Q37=makeQuery(id+"F4.opExtrude","SWEPT_BODY",BODY,{"disambiguationData":[OSD([sQuery(id+"F2.wireOp",EDGE,"E8.sketch_text.stroke-444"),sQuery(id+"F2.wireOp",EDGE,"E8.sketch_text.stroke-445"),sQuery(id+"F2.wireOp",EDGE,"E8.sketch_text.stroke-446"),sQuery(id+"F2.wireOp",EDGE,"E8.sketch_text.stroke-447"),sQuery(id+"F2.wireOp",EDGE,"E8.sketch_text.stroke-448"),sQuery(id+"F2.wireOp",EDGE,"E8.sketch_text.stroke-449"),sQuery(id+"F2.wireOp",EDGE,"E8.sketch_text.stroke-450")])]});
            var Q38;
            Q38=makeQuery(id+"F4.opExtrude","SWEPT_BODY",BODY,{"disambiguationData":[OSD([sQuery(id+"F2.wireOp",EDGE,"E8.sketch_text.stroke-451"),sQuery(id+"F2.wireOp",EDGE,"E8.sketch_text.stroke-452"),sQuery(id+"F2.wireOp",EDGE,"E8.sketch_text.stroke-453"),sQuery(id+"F2.wireOp",EDGE,"E8.sketch_text.stroke-454"),sQuery(id+"F2.wireOp",EDGE,"E8.sketch_text.stroke-455"),sQuery(id+"F2.wireOp",EDGE,"E8.sketch_text.stroke-456"),sQuery(id+"F2.wireOp",EDGE,"E8.sketch_text.stroke-457"),sQuery(id+"F2.wireOp",EDGE,"E8.sketch_text.stroke-458"),sQuery(id+"F2.wireOp",EDGE,"E8.sketch_text.stroke-459"),sQuery(id+"F2.wireOp",EDGE,"E8.sketch_text.stroke-460"),sQuery(id+"F2.wireOp",EDGE,"E8.sketch_text.stroke-461"),sQuery(id+"F2.wireOp",EDGE,"E8.sketch_text.stroke-462")])]});
            var Q39;
            Q39=makeQuery(id+"F4.opExtrude","SWEPT_BODY",BODY,{"disambiguationData":[OSD([sQuery(id+"F2.wireOp",EDGE,"E8.sketch_text.stroke-463"),sQuery(id+"F2.wireOp",EDGE,"E8.sketch_text.stroke-464"),sQuery(id+"F2.wireOp",EDGE,"E8.sketch_text.stroke-465"),sQuery(id+"F2.wireOp",EDGE,"E8.sketch_text.stroke-466"),sQuery(id+"F2.wireOp",EDGE,"E8.sketch_text.stroke-467"),sQuery(id+"F2.wireOp",EDGE,"E8.sketch_text.stroke-468"),sQuery(id+"F2.wireOp",EDGE,"E8.sketch_text.stroke-469"),sQuery(id+"F2.wireOp",EDGE,"E8.sketch_text.stroke-470"),sQuery(id+"F2.wireOp",EDGE,"E8.sketch_text.stroke-471"),sQuery(id+"F2.wireOp",EDGE,"E8.sketch_text.stroke-472"),sQuery(id+"F2.wireOp",EDGE,"E8.sketch_text.stroke-473"),sQuery(id+"F2.wireOp",EDGE,"E8.sketch_text.stroke-474"),sQuery(id+"F2.wireOp",EDGE,"E8.sketch_text.stroke-475"),sQuery(id+"F2.wireOp",EDGE,"E8.sketch_text.stroke-476"),sQuery(id+"F2.wireOp",EDGE,"E8.sketch_text.stroke-477"),sQuery(id+"F2.wireOp",EDGE,"E8.sketch_text.stroke-478"),sQuery(id+"F2.wireOp",EDGE,"E8.sketch_text.stroke-479")])]});
            var Q40;
            Q40=makeQuery(id+"F4.opExtrude","SWEPT_BODY",BODY,{"disambiguationData":[OSD([sQuery(id+"F2.wireOp",EDGE,"E8.sketch_text.stroke-480"),sQuery(id+"F2.wireOp",EDGE,"E8.sketch_text.stroke-481"),sQuery(id+"F2.wireOp",EDGE,"E8.sketch_text.stroke-482"),sQuery(id+"F2.wireOp",EDGE,"E8.sketch_text.stroke-483"),sQuery(id+"F2.wireOp",EDGE,"E8.sketch_text.stroke-484"),sQuery(id+"F2.wireOp",EDGE,"E8.sketch_text.stroke-485"),sQuery(id+"F2.wireOp",EDGE,"E8.sketch_text.stroke-486"),sQuery(id+"F2.wireOp",EDGE,"E8.sketch_text.stroke-487"),sQuery(id+"F2.wireOp",EDGE,"E8.sketch_text.stroke-488"),sQuery(id+"F2.wireOp",EDGE,"E8.sketch_text.stroke-489"),sQuery(id+"F2.wireOp",EDGE,"E8.sketch_text.stroke-490"),sQuery(id+"F2.wireOp",EDGE,"E8.sketch_text.stroke-491"),sQuery(id+"F2.wireOp",EDGE,"E8.sketch_text.stroke-492"),sQuery(id+"F2.wireOp",EDGE,"E8.sketch_text.stroke-493"),sQuery(id+"F2.wireOp",EDGE,"E8.sketch_text.stroke-494"),sQuery(id+"F2.wireOp",EDGE,"E8.sketch_text.stroke-495"),sQuery(id+"F2.wireOp",EDGE,"E8.sketch_text.stroke-496"),sQuery(id+"F2.wireOp",EDGE,"E8.sketch_text.stroke-497"),sQuery(id+"F2.wireOp",EDGE,"E8.sketch_text.stroke-498"),sQuery(id+"F2.wireOp",EDGE,"E8.sketch_text.stroke-499"),sQuery(id+"F2.wireOp",EDGE,"E8.sketch_text.stroke-500"),sQuery(id+"F2.wireOp",EDGE,"E8.sketch_text.stroke-501"),sQuery(id+"F2.wireOp",EDGE,"E8.sketch_text.stroke-502"),sQuery(id+"F2.wireOp",EDGE,"E8.sketch_text.stroke-503"),sQuery(id+"F2.wireOp",EDGE,"E8.sketch_text.stroke-504"),sQuery(id+"F2.wireOp",EDGE,"E8.sketch_text.stroke-505"),sQuery(id+"F2.wireOp",EDGE,"E8.sketch_text.stroke-506"),sQuery(id+"F2.wireOp",EDGE,"E8.sketch_text.stroke-507"),sQuery(id+"F2.wireOp",EDGE,"E8.sketch_text.stroke-508"),sQuery(id+"F2.wireOp",EDGE,"E8.sketch_text.stroke-509"),sQuery(id+"F2.wireOp",EDGE,"E8.sketch_text.stroke-510"),sQuery(id+"F2.wireOp",EDGE,"E8.sketch_text.stroke-511"),sQuery(id+"F2.wireOp",EDGE,"E8.sketch_text.stroke-512"),sQuery(id+"F2.wireOp",EDGE,"E8.sketch_text.stroke-513"),sQuery(id+"F2.wireOp",EDGE,"E8.sketch_text.stroke-514"),sQuery(id+"F2.wireOp",EDGE,"E8.sketch_text.stroke-515"),sQuery(id+"F2.wireOp",EDGE,"E8.sketch_text.stroke-516"),sQuery(id+"F2.wireOp",EDGE,"E8.sketch_text.stroke-517"),sQuery(id+"F2.wireOp",EDGE,"E8.sketch_text.stroke-518"),sQuery(id+"F2.wireOp",EDGE,"E8.sketch_text.stroke-519"),sQuery(id+"F2.wireOp",EDGE,"E8.sketch_text.stroke-520"),sQuery(id+"F2.wireOp",EDGE,"E8.sketch_text.stroke-521"),sQuery(id+"F2.wireOp",EDGE,"E8.sketch_text.stroke-522"),sQuery(id+"F2.wireOp",EDGE,"E8.sketch_text.stroke-523")])]});
            var Q41;
            Q41=makeQuery(id+"F4.opExtrude","SWEPT_BODY",BODY,{"disambiguationData":[OSD([sQuery(id+"F2.wireOp",EDGE,"E8.sketch_text.stroke-524"),sQuery(id+"F2.wireOp",EDGE,"E8.sketch_text.stroke-525"),sQuery(id+"F2.wireOp",EDGE,"E8.sketch_text.stroke-526"),sQuery(id+"F2.wireOp",EDGE,"E8.sketch_text.stroke-527")])]});
            var Q42;
            Q42=makeQuery(id+"F4.opExtrude","SWEPT_BODY",BODY,{"disambiguationData":[OSD([sQuery(id+"F2.wireOp",EDGE,"E8.sketch_text.stroke-528"),sQuery(id+"F2.wireOp",EDGE,"E8.sketch_text.stroke-529"),sQuery(id+"F2.wireOp",EDGE,"E8.sketch_text.stroke-530"),sQuery(id+"F2.wireOp",EDGE,"E8.sketch_text.stroke-531"),sQuery(id+"F2.wireOp",EDGE,"E8.sketch_text.stroke-532"),sQuery(id+"F2.wireOp",EDGE,"E8.sketch_text.stroke-533"),sQuery(id+"F2.wireOp",EDGE,"E8.sketch_text.stroke-534"),sQuery(id+"F2.wireOp",EDGE,"E8.sketch_text.stroke-535"),sQuery(id+"F2.wireOp",EDGE,"E8.sketch_text.stroke-536"),sQuery(id+"F2.wireOp",EDGE,"E8.sketch_text.stroke-537"),sQuery(id+"F2.wireOp",EDGE,"E8.sketch_text.stroke-538"),sQuery(id+"F2.wireOp",EDGE,"E8.sketch_text.stroke-539"),sQuery(id+"F2.wireOp",EDGE,"E8.sketch_text.stroke-540"),sQuery(id+"F2.wireOp",EDGE,"E8.sketch_text.stroke-541"),sQuery(id+"F2.wireOp",EDGE,"E8.sketch_text.stroke-542"),sQuery(id+"F2.wireOp",EDGE,"E8.sketch_text.stroke-543"),sQuery(id+"F2.wireOp",EDGE,"E8.sketch_text.stroke-544"),sQuery(id+"F2.wireOp",EDGE,"E8.sketch_text.stroke-545"),sQuery(id+"F2.wireOp",EDGE,"E8.sketch_text.stroke-546"),sQuery(id+"F2.wireOp",EDGE,"E8.sketch_text.stroke-547"),sQuery(id+"F2.wireOp",EDGE,"E8.sketch_text.stroke-548"),sQuery(id+"F2.wireOp",EDGE,"E8.sketch_text.stroke-549"),sQuery(id+"F2.wireOp",EDGE,"E8.sketch_text.stroke-550"),sQuery(id+"F2.wireOp",EDGE,"E8.sketch_text.stroke-551"),sQuery(id+"F2.wireOp",EDGE,"E8.sketch_text.stroke-552"),sQuery(id+"F2.wireOp",EDGE,"E8.sketch_text.stroke-553"),sQuery(id+"F2.wireOp",EDGE,"E8.sketch_text.stroke-554")])]});
            var Q43;
            Q43=makeQuery(id+"F4.opExtrude","SWEPT_BODY",BODY,{"disambiguationData":[OSD([sQuery(id+"F2.wireOp",EDGE,"E8.sketch_text.stroke-555"),sQuery(id+"F2.wireOp",EDGE,"E8.sketch_text.stroke-556"),sQuery(id+"F2.wireOp",EDGE,"E8.sketch_text.stroke-557"),sQuery(id+"F2.wireOp",EDGE,"E8.sketch_text.stroke-558"),sQuery(id+"F2.wireOp",EDGE,"E8.sketch_text.stroke-559"),sQuery(id+"F2.wireOp",EDGE,"E8.sketch_text.stroke-560"),sQuery(id+"F2.wireOp",EDGE,"E8.sketch_text.stroke-561"),sQuery(id+"F2.wireOp",EDGE,"E8.sketch_text.stroke-562"),sQuery(id+"F2.wireOp",EDGE,"E8.sketch_text.stroke-563"),sQuery(id+"F2.wireOp",EDGE,"E8.sketch_text.stroke-564"),sQuery(id+"F2.wireOp",EDGE,"E8.sketch_text.stroke-565"),sQuery(id+"F2.wireOp",EDGE,"E8.sketch_text.stroke-566"),sQuery(id+"F2.wireOp",EDGE,"E8.sketch_text.stroke-567"),sQuery(id+"F2.wireOp",EDGE,"E8.sketch_text.stroke-568"),sQuery(id+"F2.wireOp",EDGE,"E8.sketch_text.stroke-569"),sQuery(id+"F2.wireOp",EDGE,"E8.sketch_text.stroke-570"),sQuery(id+"F2.wireOp",EDGE,"E8.sketch_text.stroke-571")])]});
            var Q44;
            Q44=makeQuery(id+"F4.opExtrude","SWEPT_BODY",BODY,{"disambiguationData":[OSD([sQuery(id+"F2.wireOp",EDGE,"E8.sketch_text.stroke-572"),sQuery(id+"F2.wireOp",EDGE,"E8.sketch_text.stroke-573"),sQuery(id+"F2.wireOp",EDGE,"E8.sketch_text.stroke-574"),sQuery(id+"F2.wireOp",EDGE,"E8.sketch_text.stroke-575"),sQuery(id+"F2.wireOp",EDGE,"E8.sketch_text.stroke-576"),sQuery(id+"F2.wireOp",EDGE,"E8.sketch_text.stroke-577"),sQuery(id+"F2.wireOp",EDGE,"E8.sketch_text.stroke-578"),sQuery(id+"F2.wireOp",EDGE,"E8.sketch_text.stroke-579"),sQuery(id+"F2.wireOp",EDGE,"E8.sketch_text.stroke-580"),sQuery(id+"F2.wireOp",EDGE,"E8.sketch_text.stroke-581"),sQuery(id+"F2.wireOp",EDGE,"E8.sketch_text.stroke-582"),sQuery(id+"F2.wireOp",EDGE,"E8.sketch_text.stroke-583"),sQuery(id+"F2.wireOp",EDGE,"E8.sketch_text.stroke-584"),sQuery(id+"F2.wireOp",EDGE,"E8.sketch_text.stroke-585"),sQuery(id+"F2.wireOp",EDGE,"E8.sketch_text.stroke-586"),sQuery(id+"F2.wireOp",EDGE,"E8.sketch_text.stroke-587"),sQuery(id+"F2.wireOp",EDGE,"E8.sketch_text.stroke-588"),sQuery(id+"F2.wireOp",EDGE,"E8.sketch_text.stroke-589"),sQuery(id+"F2.wireOp",EDGE,"E8.sketch_text.stroke-590"),sQuery(id+"F2.wireOp",EDGE,"E8.sketch_text.stroke-591"),sQuery(id+"F2.wireOp",EDGE,"E8.sketch_text.stroke-592"),sQuery(id+"F2.wireOp",EDGE,"E8.sketch_text.stroke-593"),sQuery(id+"F2.wireOp",EDGE,"E8.sketch_text.stroke-594"),sQuery(id+"F2.wireOp",EDGE,"E8.sketch_text.stroke-595")])]});
            var Q45;
            Q45=makeQuery(id+"F4.opExtrude","SWEPT_BODY",BODY,{"disambiguationData":[OSD([sQuery(id+"F2.wireOp",EDGE,"E9.sketch_text.stroke-0"),sQuery(id+"F2.wireOp",EDGE,"E9.sketch_text.stroke-1"),sQuery(id+"F2.wireOp",EDGE,"E9.sketch_text.stroke-2"),sQuery(id+"F2.wireOp",EDGE,"E9.sketch_text.stroke-3"),sQuery(id+"F2.wireOp",EDGE,"E9.sketch_text.stroke-4"),sQuery(id+"F2.wireOp",EDGE,"E9.sketch_text.stroke-5"),sQuery(id+"F2.wireOp",EDGE,"E9.sketch_text.stroke-6"),sQuery(id+"F2.wireOp",EDGE,"E9.sketch_text.stroke-7"),sQuery(id+"F2.wireOp",EDGE,"E9.sketch_text.stroke-8"),sQuery(id+"F2.wireOp",EDGE,"E9.sketch_text.stroke-9")])]});
            var Q46;
            Q46=makeQuery(id+"F4.opExtrude","SWEPT_BODY",BODY,{"disambiguationData":[OSD([sQuery(id+"F2.wireOp",EDGE,"E9.sketch_text.stroke-10"),sQuery(id+"F2.wireOp",EDGE,"E9.sketch_text.stroke-11"),sQuery(id+"F2.wireOp",EDGE,"E9.sketch_text.stroke-12"),sQuery(id+"F2.wireOp",EDGE,"E9.sketch_text.stroke-13")])]});
            var Q47;
            Q47=makeQuery(id+"F4.opExtrude","SWEPT_BODY",BODY,{"disambiguationData":[OSD([sQuery(id+"F2.wireOp",EDGE,"E9.sketch_text.stroke-14"),sQuery(id+"F2.wireOp",EDGE,"E9.sketch_text.stroke-15"),sQuery(id+"F2.wireOp",EDGE,"E9.sketch_text.stroke-16"),sQuery(id+"F2.wireOp",EDGE,"E9.sketch_text.stroke-17"),sQuery(id+"F2.wireOp",EDGE,"E9.sketch_text.stroke-18"),sQuery(id+"F2.wireOp",EDGE,"E9.sketch_text.stroke-19"),sQuery(id+"F2.wireOp",EDGE,"E9.sketch_text.stroke-20"),sQuery(id+"F2.wireOp",EDGE,"E9.sketch_text.stroke-21")])]});
            var Q48;
            Q48=makeQuery(id+"F4.opExtrude","SWEPT_BODY",BODY,{"disambiguationData":[OSD([sQuery(id+"F2.wireOp",EDGE,"E9.sketch_text.stroke-22"),sQuery(id+"F2.wireOp",EDGE,"E9.sketch_text.stroke-23"),sQuery(id+"F2.wireOp",EDGE,"E9.sketch_text.stroke-24"),sQuery(id+"F2.wireOp",EDGE,"E9.sketch_text.stroke-25"),sQuery(id+"F2.wireOp",EDGE,"E9.sketch_text.stroke-26"),sQuery(id+"F2.wireOp",EDGE,"E9.sketch_text.stroke-27"),sQuery(id+"F2.wireOp",EDGE,"E9.sketch_text.stroke-28"),sQuery(id+"F2.wireOp",EDGE,"E9.sketch_text.stroke-29"),sQuery(id+"F2.wireOp",EDGE,"E9.sketch_text.stroke-30"),sQuery(id+"F2.wireOp",EDGE,"E9.sketch_text.stroke-31"),sQuery(id+"F2.wireOp",EDGE,"E9.sketch_text.stroke-32"),sQuery(id+"F2.wireOp",EDGE,"E9.sketch_text.stroke-33"),sQuery(id+"F2.wireOp",EDGE,"E9.sketch_text.stroke-34"),sQuery(id+"F2.wireOp",EDGE,"E9.sketch_text.stroke-35"),sQuery(id+"F2.wireOp",EDGE,"E9.sketch_text.stroke-36"),sQuery(id+"F2.wireOp",EDGE,"E9.sketch_text.stroke-37"),sQuery(id+"F2.wireOp",EDGE,"E9.sketch_text.stroke-38"),sQuery(id+"F2.wireOp",EDGE,"E9.sketch_text.stroke-39"),sQuery(id+"F2.wireOp",EDGE,"E9.sketch_text.stroke-40")])]});
            var Q49;
            Q49=makeQuery(id+"F4.opExtrude","SWEPT_BODY",BODY,{"disambiguationData":[OSD([sQuery(id+"F2.wireOp",EDGE,"E9.sketch_text.stroke-41"),sQuery(id+"F2.wireOp",EDGE,"E9.sketch_text.stroke-42"),sQuery(id+"F2.wireOp",EDGE,"E9.sketch_text.stroke-43"),sQuery(id+"F2.wireOp",EDGE,"E9.sketch_text.stroke-44"),sQuery(id+"F2.wireOp",EDGE,"E9.sketch_text.stroke-45"),sQuery(id+"F2.wireOp",EDGE,"E9.sketch_text.stroke-46"),sQuery(id+"F2.wireOp",EDGE,"E9.sketch_text.stroke-47"),sQuery(id+"F2.wireOp",EDGE,"E9.sketch_text.stroke-48"),sQuery(id+"F2.wireOp",EDGE,"E9.sketch_text.stroke-49"),sQuery(id+"F2.wireOp",EDGE,"E9.sketch_text.stroke-50"),sQuery(id+"F2.wireOp",EDGE,"E9.sketch_text.stroke-51"),sQuery(id+"F2.wireOp",EDGE,"E9.sketch_text.stroke-52"),sQuery(id+"F2.wireOp",EDGE,"E9.sketch_text.stroke-53"),sQuery(id+"F2.wireOp",EDGE,"E9.sketch_text.stroke-54"),sQuery(id+"F2.wireOp",EDGE,"E9.sketch_text.stroke-55"),sQuery(id+"F2.wireOp",EDGE,"E9.sketch_text.stroke-56"),sQuery(id+"F2.wireOp",EDGE,"E9.sketch_text.stroke-57"),sQuery(id+"F2.wireOp",EDGE,"E9.sketch_text.stroke-58"),sQuery(id+"F2.wireOp",EDGE,"E9.sketch_text.stroke-59")])]});
            var Q50;
            Q50=makeQuery(id+"F4.opExtrude","SWEPT_BODY",BODY,{"disambiguationData":[OSD([sQuery(id+"F2.wireOp",EDGE,"E9.sketch_text.stroke-60"),sQuery(id+"F2.wireOp",EDGE,"E9.sketch_text.stroke-61"),sQuery(id+"F2.wireOp",EDGE,"E9.sketch_text.stroke-62"),sQuery(id+"F2.wireOp",EDGE,"E9.sketch_text.stroke-63"),sQuery(id+"F2.wireOp",EDGE,"E9.sketch_text.stroke-64"),sQuery(id+"F2.wireOp",EDGE,"E9.sketch_text.stroke-65"),sQuery(id+"F2.wireOp",EDGE,"E9.sketch_text.stroke-66"),sQuery(id+"F2.wireOp",EDGE,"E9.sketch_text.stroke-67"),sQuery(id+"F2.wireOp",EDGE,"E9.sketch_text.stroke-68"),sQuery(id+"F2.wireOp",EDGE,"E9.sketch_text.stroke-69"),sQuery(id+"F2.wireOp",EDGE,"E9.sketch_text.stroke-70"),sQuery(id+"F2.wireOp",EDGE,"E9.sketch_text.stroke-71"),sQuery(id+"F2.wireOp",EDGE,"E9.sketch_text.stroke-72"),sQuery(id+"F2.wireOp",EDGE,"E9.sketch_text.stroke-73"),sQuery(id+"F2.wireOp",EDGE,"E9.sketch_text.stroke-74"),sQuery(id+"F2.wireOp",EDGE,"E9.sketch_text.stroke-75"),sQuery(id+"F2.wireOp",EDGE,"E9.sketch_text.stroke-76"),sQuery(id+"F2.wireOp",EDGE,"E9.sketch_text.stroke-77"),sQuery(id+"F2.wireOp",EDGE,"E9.sketch_text.stroke-78")])]});
            var Q51;
            Q51=makeQuery(id+"F4.opExtrude","SWEPT_BODY",BODY,{"disambiguationData":[OSD([sQuery(id+"F2.wireOp",EDGE,"E9.sketch_text.stroke-79"),sQuery(id+"F2.wireOp",EDGE,"E9.sketch_text.stroke-80"),sQuery(id+"F2.wireOp",EDGE,"E9.sketch_text.stroke-81"),sQuery(id+"F2.wireOp",EDGE,"E9.sketch_text.stroke-82"),sQuery(id+"F2.wireOp",EDGE,"E9.sketch_text.stroke-83"),sQuery(id+"F2.wireOp",EDGE,"E9.sketch_text.stroke-84"),sQuery(id+"F2.wireOp",EDGE,"E9.sketch_text.stroke-85"),sQuery(id+"F2.wireOp",EDGE,"E9.sketch_text.stroke-86"),sQuery(id+"F2.wireOp",EDGE,"E9.sketch_text.stroke-87"),sQuery(id+"F2.wireOp",EDGE,"E9.sketch_text.stroke-88"),sQuery(id+"F2.wireOp",EDGE,"E9.sketch_text.stroke-89"),sQuery(id+"F2.wireOp",EDGE,"E9.sketch_text.stroke-90"),sQuery(id+"F2.wireOp",EDGE,"E9.sketch_text.stroke-91"),sQuery(id+"F2.wireOp",EDGE,"E9.sketch_text.stroke-92"),sQuery(id+"F2.wireOp",EDGE,"E9.sketch_text.stroke-93"),sQuery(id+"F2.wireOp",EDGE,"E9.sketch_text.stroke-94"),sQuery(id+"F2.wireOp",EDGE,"E9.sketch_text.stroke-95"),sQuery(id+"F2.wireOp",EDGE,"E9.sketch_text.stroke-96"),sQuery(id+"F2.wireOp",EDGE,"E9.sketch_text.stroke-97"),sQuery(id+"F2.wireOp",EDGE,"E9.sketch_text.stroke-98"),sQuery(id+"F2.wireOp",EDGE,"E9.sketch_text.stroke-99"),sQuery(id+"F2.wireOp",EDGE,"E9.sketch_text.stroke-100"),sQuery(id+"F2.wireOp",EDGE,"E9.sketch_text.stroke-101"),sQuery(id+"F2.wireOp",EDGE,"E9.sketch_text.stroke-102")])]});
            var Q52;
            Q52=makeQuery(id+"F4.opExtrude","SWEPT_BODY",BODY,{"disambiguationData":[OSD([sQuery(id+"F2.wireOp",EDGE,"E9.sketch_text.stroke-103"),sQuery(id+"F2.wireOp",EDGE,"E9.sketch_text.stroke-104"),sQuery(id+"F2.wireOp",EDGE,"E9.sketch_text.stroke-105"),sQuery(id+"F2.wireOp",EDGE,"E9.sketch_text.stroke-106"),sQuery(id+"F2.wireOp",EDGE,"E9.sketch_text.stroke-107"),sQuery(id+"F2.wireOp",EDGE,"E9.sketch_text.stroke-108"),sQuery(id+"F2.wireOp",EDGE,"E9.sketch_text.stroke-109"),sQuery(id+"F2.wireOp",EDGE,"E9.sketch_text.stroke-110"),sQuery(id+"F2.wireOp",EDGE,"E9.sketch_text.stroke-111"),sQuery(id+"F2.wireOp",EDGE,"E9.sketch_text.stroke-112"),sQuery(id+"F2.wireOp",EDGE,"E9.sketch_text.stroke-113"),sQuery(id+"F2.wireOp",EDGE,"E9.sketch_text.stroke-114"),sQuery(id+"F2.wireOp",EDGE,"E9.sketch_text.stroke-115"),sQuery(id+"F2.wireOp",EDGE,"E9.sketch_text.stroke-116"),sQuery(id+"F2.wireOp",EDGE,"E9.sketch_text.stroke-117"),sQuery(id+"F2.wireOp",EDGE,"E9.sketch_text.stroke-118"),sQuery(id+"F2.wireOp",EDGE,"E9.sketch_text.stroke-119")])]});
            var Q53;
            Q53=makeQuery(id+"F4.opExtrude","SWEPT_BODY",BODY,{"disambiguationData":[OSD([sQuery(id+"F2.wireOp",EDGE,"E9.sketch_text.stroke-120"),sQuery(id+"F2.wireOp",EDGE,"E9.sketch_text.stroke-121"),sQuery(id+"F2.wireOp",EDGE,"E9.sketch_text.stroke-122"),sQuery(id+"F2.wireOp",EDGE,"E9.sketch_text.stroke-123"),sQuery(id+"F2.wireOp",EDGE,"E9.sketch_text.stroke-124"),sQuery(id+"F2.wireOp",EDGE,"E9.sketch_text.stroke-125"),sQuery(id+"F2.wireOp",EDGE,"E9.sketch_text.stroke-126"),sQuery(id+"F2.wireOp",EDGE,"E9.sketch_text.stroke-127"),sQuery(id+"F2.wireOp",EDGE,"E9.sketch_text.stroke-128"),sQuery(id+"F2.wireOp",EDGE,"E9.sketch_text.stroke-129"),sQuery(id+"F2.wireOp",EDGE,"E9.sketch_text.stroke-130"),sQuery(id+"F2.wireOp",EDGE,"E9.sketch_text.stroke-131"),sQuery(id+"F2.wireOp",EDGE,"E9.sketch_text.stroke-132"),sQuery(id+"F2.wireOp",EDGE,"E9.sketch_text.stroke-133"),sQuery(id+"F2.wireOp",EDGE,"E9.sketch_text.stroke-134"),sQuery(id+"F2.wireOp",EDGE,"E9.sketch_text.stroke-135"),sQuery(id+"F2.wireOp",EDGE,"E9.sketch_text.stroke-136")])]});
            var Q54;
            Q54=makeQuery(id+"F4.opExtrude","SWEPT_BODY",BODY,{"disambiguationData":[OSD([sQuery(id+"F2.wireOp",EDGE,"E9.sketch_text.stroke-137"),sQuery(id+"F2.wireOp",EDGE,"E9.sketch_text.stroke-138"),sQuery(id+"F2.wireOp",EDGE,"E9.sketch_text.stroke-139"),sQuery(id+"F2.wireOp",EDGE,"E9.sketch_text.stroke-140"),sQuery(id+"F2.wireOp",EDGE,"E9.sketch_text.stroke-141"),sQuery(id+"F2.wireOp",EDGE,"E9.sketch_text.stroke-142"),sQuery(id+"F2.wireOp",EDGE,"E9.sketch_text.stroke-143"),sQuery(id+"F2.wireOp",EDGE,"E9.sketch_text.stroke-144"),sQuery(id+"F2.wireOp",EDGE,"E9.sketch_text.stroke-145"),sQuery(id+"F2.wireOp",EDGE,"E9.sketch_text.stroke-146"),sQuery(id+"F2.wireOp",EDGE,"E9.sketch_text.stroke-147"),sQuery(id+"F2.wireOp",EDGE,"E9.sketch_text.stroke-148"),sQuery(id+"F2.wireOp",EDGE,"E9.sketch_text.stroke-149"),sQuery(id+"F2.wireOp",EDGE,"E9.sketch_text.stroke-150"),sQuery(id+"F2.wireOp",EDGE,"E9.sketch_text.stroke-151"),sQuery(id+"F2.wireOp",EDGE,"E9.sketch_text.stroke-152"),sQuery(id+"F2.wireOp",EDGE,"E9.sketch_text.stroke-153"),sQuery(id+"F2.wireOp",EDGE,"E9.sketch_text.stroke-154"),sQuery(id+"F2.wireOp",EDGE,"E9.sketch_text.stroke-155")])]});
            var Q55;
            Q55=makeQuery(id+"F4.opExtrude","SWEPT_BODY",BODY,{"disambiguationData":[OSD([sQuery(id+"F2.wireOp",EDGE,"E9.sketch_text.stroke-156"),sQuery(id+"F2.wireOp",EDGE,"E9.sketch_text.stroke-157"),sQuery(id+"F2.wireOp",EDGE,"E9.sketch_text.stroke-158"),sQuery(id+"F2.wireOp",EDGE,"E9.sketch_text.stroke-159"),sQuery(id+"F2.wireOp",EDGE,"E9.sketch_text.stroke-160"),sQuery(id+"F2.wireOp",EDGE,"E9.sketch_text.stroke-161"),sQuery(id+"F2.wireOp",EDGE,"E9.sketch_text.stroke-162"),sQuery(id+"F2.wireOp",EDGE,"E9.sketch_text.stroke-163"),sQuery(id+"F2.wireOp",EDGE,"E9.sketch_text.stroke-164"),sQuery(id+"F2.wireOp",EDGE,"E9.sketch_text.stroke-165"),sQuery(id+"F2.wireOp",EDGE,"E9.sketch_text.stroke-166"),sQuery(id+"F2.wireOp",EDGE,"E9.sketch_text.stroke-167"),sQuery(id+"F2.wireOp",EDGE,"E9.sketch_text.stroke-168"),sQuery(id+"F2.wireOp",EDGE,"E9.sketch_text.stroke-169"),sQuery(id+"F2.wireOp",EDGE,"E9.sketch_text.stroke-170"),sQuery(id+"F2.wireOp",EDGE,"E9.sketch_text.stroke-171"),sQuery(id+"F2.wireOp",EDGE,"E9.sketch_text.stroke-172"),sQuery(id+"F2.wireOp",EDGE,"E9.sketch_text.stroke-173"),sQuery(id+"F2.wireOp",EDGE,"E9.sketch_text.stroke-174"),sQuery(id+"F2.wireOp",EDGE,"E9.sketch_text.stroke-175"),sQuery(id+"F2.wireOp",EDGE,"E9.sketch_text.stroke-176"),sQuery(id+"F2.wireOp",EDGE,"E9.sketch_text.stroke-177"),sQuery(id+"F2.wireOp",EDGE,"E9.sketch_text.stroke-178")])]});
            var Q56;
            Q56=makeQuery(id+"F4.opExtrude","SWEPT_BODY",BODY,{"disambiguationData":[OSD([sQuery(id+"F2.wireOp",EDGE,"E9.sketch_text.stroke-179"),sQuery(id+"F2.wireOp",EDGE,"E9.sketch_text.stroke-180"),sQuery(id+"F2.wireOp",EDGE,"E9.sketch_text.stroke-181"),sQuery(id+"F2.wireOp",EDGE,"E9.sketch_text.stroke-182"),sQuery(id+"F2.wireOp",EDGE,"E9.sketch_text.stroke-183"),sQuery(id+"F2.wireOp",EDGE,"E9.sketch_text.stroke-184"),sQuery(id+"F2.wireOp",EDGE,"E9.sketch_text.stroke-185"),sQuery(id+"F2.wireOp",EDGE,"E9.sketch_text.stroke-186"),sQuery(id+"F2.wireOp",EDGE,"E9.sketch_text.stroke-187"),sQuery(id+"F2.wireOp",EDGE,"E9.sketch_text.stroke-188"),sQuery(id+"F2.wireOp",EDGE,"E9.sketch_text.stroke-189"),sQuery(id+"F2.wireOp",EDGE,"E9.sketch_text.stroke-190"),sQuery(id+"F2.wireOp",EDGE,"E9.sketch_text.stroke-191"),sQuery(id+"F2.wireOp",EDGE,"E9.sketch_text.stroke-192"),sQuery(id+"F2.wireOp",EDGE,"E9.sketch_text.stroke-193"),sQuery(id+"F2.wireOp",EDGE,"E9.sketch_text.stroke-194")])]});
            var Q57;
            Q57=makeQuery(id+"F4.opExtrude","SWEPT_BODY",BODY,{"disambiguationData":[OSD([sQuery(id+"F2.wireOp",EDGE,"E9.sketch_text.stroke-195"),sQuery(id+"F2.wireOp",EDGE,"E9.sketch_text.stroke-196"),sQuery(id+"F2.wireOp",EDGE,"E9.sketch_text.stroke-197"),sQuery(id+"F2.wireOp",EDGE,"E9.sketch_text.stroke-198"),sQuery(id+"F2.wireOp",EDGE,"E9.sketch_text.stroke-199"),sQuery(id+"F2.wireOp",EDGE,"E9.sketch_text.stroke-200"),sQuery(id+"F2.wireOp",EDGE,"E9.sketch_text.stroke-201"),sQuery(id+"F2.wireOp",EDGE,"E9.sketch_text.stroke-202"),sQuery(id+"F2.wireOp",EDGE,"E9.sketch_text.stroke-203"),sQuery(id+"F2.wireOp",EDGE,"E9.sketch_text.stroke-204"),sQuery(id+"F2.wireOp",EDGE,"E9.sketch_text.stroke-205"),sQuery(id+"F2.wireOp",EDGE,"E9.sketch_text.stroke-206"),sQuery(id+"F2.wireOp",EDGE,"E9.sketch_text.stroke-207"),sQuery(id+"F2.wireOp",EDGE,"E9.sketch_text.stroke-208"),sQuery(id+"F2.wireOp",EDGE,"E9.sketch_text.stroke-209")])]});
            var Q58;
            Q58=makeQuery(id+"F4.opExtrude","SWEPT_BODY",BODY,{"disambiguationData":[OSD([sQuery(id+"F2.wireOp",EDGE,"E9.sketch_text.stroke-210"),sQuery(id+"F2.wireOp",EDGE,"E9.sketch_text.stroke-211"),sQuery(id+"F2.wireOp",EDGE,"E9.sketch_text.stroke-212"),sQuery(id+"F2.wireOp",EDGE,"E9.sketch_text.stroke-213"),sQuery(id+"F2.wireOp",EDGE,"E9.sketch_text.stroke-214"),sQuery(id+"F2.wireOp",EDGE,"E9.sketch_text.stroke-215"),sQuery(id+"F2.wireOp",EDGE,"E9.sketch_text.stroke-216"),sQuery(id+"F2.wireOp",EDGE,"E9.sketch_text.stroke-217"),sQuery(id+"F2.wireOp",EDGE,"E9.sketch_text.stroke-218"),sQuery(id+"F2.wireOp",EDGE,"E9.sketch_text.stroke-219"),sQuery(id+"F2.wireOp",EDGE,"E9.sketch_text.stroke-220"),sQuery(id+"F2.wireOp",EDGE,"E9.sketch_text.stroke-221"),sQuery(id+"F2.wireOp",EDGE,"E9.sketch_text.stroke-222"),sQuery(id+"F2.wireOp",EDGE,"E9.sketch_text.stroke-223"),sQuery(id+"F2.wireOp",EDGE,"E9.sketch_text.stroke-224"),sQuery(id+"F2.wireOp",EDGE,"E9.sketch_text.stroke-225"),sQuery(id+"F2.wireOp",EDGE,"E9.sketch_text.stroke-226"),sQuery(id+"F2.wireOp",EDGE,"E9.sketch_text.stroke-227"),sQuery(id+"F2.wireOp",EDGE,"E9.sketch_text.stroke-228"),sQuery(id+"F2.wireOp",EDGE,"E9.sketch_text.stroke-229"),sQuery(id+"F2.wireOp",EDGE,"E9.sketch_text.stroke-230"),sQuery(id+"F2.wireOp",EDGE,"E9.sketch_text.stroke-231"),sQuery(id+"F2.wireOp",EDGE,"E9.sketch_text.stroke-232"),sQuery(id+"F2.wireOp",EDGE,"E9.sketch_text.stroke-233"),sQuery(id+"F2.wireOp",EDGE,"E9.sketch_text.stroke-234"),sQuery(id+"F2.wireOp",EDGE,"E9.sketch_text.stroke-235"),sQuery(id+"F2.wireOp",EDGE,"E9.sketch_text.stroke-236")])]});
            var Q59;
            Q59=makeQuery(id+"F4.opExtrude","SWEPT_BODY",BODY,{"disambiguationData":[OSD([sQuery(id+"F2.wireOp",EDGE,"E9.sketch_text.stroke-237"),sQuery(id+"F2.wireOp",EDGE,"E9.sketch_text.stroke-238"),sQuery(id+"F2.wireOp",EDGE,"E9.sketch_text.stroke-239"),sQuery(id+"F2.wireOp",EDGE,"E9.sketch_text.stroke-240"),sQuery(id+"F2.wireOp",EDGE,"E9.sketch_text.stroke-241"),sQuery(id+"F2.wireOp",EDGE,"E9.sketch_text.stroke-242"),sQuery(id+"F2.wireOp",EDGE,"E9.sketch_text.stroke-243"),sQuery(id+"F2.wireOp",EDGE,"E9.sketch_text.stroke-244"),sQuery(id+"F2.wireOp",EDGE,"E9.sketch_text.stroke-245"),sQuery(id+"F2.wireOp",EDGE,"E9.sketch_text.stroke-246"),sQuery(id+"F2.wireOp",EDGE,"E9.sketch_text.stroke-247"),sQuery(id+"F2.wireOp",EDGE,"E9.sketch_text.stroke-248"),sQuery(id+"F2.wireOp",EDGE,"E9.sketch_text.stroke-249"),sQuery(id+"F2.wireOp",EDGE,"E9.sketch_text.stroke-250"),sQuery(id+"F2.wireOp",EDGE,"E9.sketch_text.stroke-251"),sQuery(id+"F2.wireOp",EDGE,"E9.sketch_text.stroke-252"),sQuery(id+"F2.wireOp",EDGE,"E9.sketch_text.stroke-253")])]});
            var Q60;
            Q60=makeQuery(id+"F4.opExtrude","SWEPT_BODY",BODY,{"disambiguationData":[OSD([sQuery(id+"F2.wireOp",EDGE,"E9.sketch_text.stroke-254"),sQuery(id+"F2.wireOp",EDGE,"E9.sketch_text.stroke-255"),sQuery(id+"F2.wireOp",EDGE,"E9.sketch_text.stroke-256"),sQuery(id+"F2.wireOp",EDGE,"E9.sketch_text.stroke-257")])]});
            var Q61;
            Q61=makeQuery(id+"F4.opExtrude","SWEPT_BODY",BODY,{"disambiguationData":[OSD([sQuery(id+"F2.wireOp",EDGE,"E9.sketch_text.stroke-258"),sQuery(id+"F2.wireOp",EDGE,"E9.sketch_text.stroke-259"),sQuery(id+"F2.wireOp",EDGE,"E9.sketch_text.stroke-260"),sQuery(id+"F2.wireOp",EDGE,"E9.sketch_text.stroke-261"),sQuery(id+"F2.wireOp",EDGE,"E9.sketch_text.stroke-262"),sQuery(id+"F2.wireOp",EDGE,"E9.sketch_text.stroke-263")])]});
            var Q62;
            Q62=makeQuery(id+"F4.opExtrude","SWEPT_BODY",BODY,{"disambiguationData":[OSD([sQuery(id+"F2.wireOp",EDGE,"E9.sketch_text.stroke-264"),sQuery(id+"F2.wireOp",EDGE,"E9.sketch_text.stroke-265"),sQuery(id+"F2.wireOp",EDGE,"E9.sketch_text.stroke-266"),sQuery(id+"F2.wireOp",EDGE,"E9.sketch_text.stroke-267")])]});
            var Q63;
            Q63=makeQuery(id+"F4.opExtrude","SWEPT_BODY",BODY,{"disambiguationData":[OSD([sQuery(id+"F2.wireOp",EDGE,"E9.sketch_text.stroke-268"),sQuery(id+"F2.wireOp",EDGE,"E9.sketch_text.stroke-269"),sQuery(id+"F2.wireOp",EDGE,"E9.sketch_text.stroke-270"),sQuery(id+"F2.wireOp",EDGE,"E9.sketch_text.stroke-271"),sQuery(id+"F2.wireOp",EDGE,"E9.sketch_text.stroke-272"),sQuery(id+"F2.wireOp",EDGE,"E9.sketch_text.stroke-273"),sQuery(id+"F2.wireOp",EDGE,"E9.sketch_text.stroke-274"),sQuery(id+"F2.wireOp",EDGE,"E9.sketch_text.stroke-275")])]});
            var Q64;
            Q64=makeQuery(id+"F4.opExtrude","SWEPT_BODY",BODY,{"disambiguationData":[OSD([sQuery(id+"F2.wireOp",EDGE,"E9.sketch_text.stroke-276"),sQuery(id+"F2.wireOp",EDGE,"E9.sketch_text.stroke-277"),sQuery(id+"F2.wireOp",EDGE,"E9.sketch_text.stroke-278"),sQuery(id+"F2.wireOp",EDGE,"E9.sketch_text.stroke-279"),sQuery(id+"F2.wireOp",EDGE,"E9.sketch_text.stroke-280"),sQuery(id+"F2.wireOp",EDGE,"E9.sketch_text.stroke-281"),sQuery(id+"F2.wireOp",EDGE,"E9.sketch_text.stroke-282"),sQuery(id+"F2.wireOp",EDGE,"E9.sketch_text.stroke-283"),sQuery(id+"F2.wireOp",EDGE,"E9.sketch_text.stroke-284"),sQuery(id+"F2.wireOp",EDGE,"E9.sketch_text.stroke-285"),sQuery(id+"F2.wireOp",EDGE,"E9.sketch_text.stroke-286"),sQuery(id+"F2.wireOp",EDGE,"E9.sketch_text.stroke-287"),sQuery(id+"F2.wireOp",EDGE,"E9.sketch_text.stroke-288"),sQuery(id+"F2.wireOp",EDGE,"E9.sketch_text.stroke-289"),sQuery(id+"F2.wireOp",EDGE,"E9.sketch_text.stroke-290"),sQuery(id+"F2.wireOp",EDGE,"E9.sketch_text.stroke-291"),sQuery(id+"F2.wireOp",EDGE,"E9.sketch_text.stroke-292"),sQuery(id+"F2.wireOp",EDGE,"E9.sketch_text.stroke-293"),sQuery(id+"F2.wireOp",EDGE,"E9.sketch_text.stroke-294")])]});
            var Q65;
            Q65=makeQuery(id+"F4.opExtrude","SWEPT_BODY",BODY,{"disambiguationData":[OSD([sQuery(id+"F2.wireOp",EDGE,"E9.sketch_text.stroke-295"),sQuery(id+"F2.wireOp",EDGE,"E9.sketch_text.stroke-296"),sQuery(id+"F2.wireOp",EDGE,"E9.sketch_text.stroke-297"),sQuery(id+"F2.wireOp",EDGE,"E9.sketch_text.stroke-298"),sQuery(id+"F2.wireOp",EDGE,"E9.sketch_text.stroke-299"),sQuery(id+"F2.wireOp",EDGE,"E9.sketch_text.stroke-300"),sQuery(id+"F2.wireOp",EDGE,"E9.sketch_text.stroke-301"),sQuery(id+"F2.wireOp",EDGE,"E9.sketch_text.stroke-302"),sQuery(id+"F2.wireOp",EDGE,"E9.sketch_text.stroke-303"),sQuery(id+"F2.wireOp",EDGE,"E9.sketch_text.stroke-304"),sQuery(id+"F2.wireOp",EDGE,"E9.sketch_text.stroke-305"),sQuery(id+"F2.wireOp",EDGE,"E9.sketch_text.stroke-306"),sQuery(id+"F2.wireOp",EDGE,"E9.sketch_text.stroke-307"),sQuery(id+"F2.wireOp",EDGE,"E9.sketch_text.stroke-308"),sQuery(id+"F2.wireOp",EDGE,"E9.sketch_text.stroke-309"),sQuery(id+"F2.wireOp",EDGE,"E9.sketch_text.stroke-310"),sQuery(id+"F2.wireOp",EDGE,"E9.sketch_text.stroke-311"),sQuery(id+"F2.wireOp",EDGE,"E9.sketch_text.stroke-312"),sQuery(id+"F2.wireOp",EDGE,"E9.sketch_text.stroke-313")])]});
            var Q66;
            Q66=makeQuery(id+"F4.opExtrude","SWEPT_BODY",BODY,{"disambiguationData":[OSD([sQuery(id+"F2.wireOp",EDGE,"E9.sketch_text.stroke-314"),sQuery(id+"F2.wireOp",EDGE,"E9.sketch_text.stroke-315"),sQuery(id+"F2.wireOp",EDGE,"E9.sketch_text.stroke-316"),sQuery(id+"F2.wireOp",EDGE,"E9.sketch_text.stroke-317"),sQuery(id+"F2.wireOp",EDGE,"E9.sketch_text.stroke-318"),sQuery(id+"F2.wireOp",EDGE,"E9.sketch_text.stroke-319"),sQuery(id+"F2.wireOp",EDGE,"E9.sketch_text.stroke-320"),sQuery(id+"F2.wireOp",EDGE,"E9.sketch_text.stroke-321"),sQuery(id+"F2.wireOp",EDGE,"E9.sketch_text.stroke-322"),sQuery(id+"F2.wireOp",EDGE,"E9.sketch_text.stroke-323"),sQuery(id+"F2.wireOp",EDGE,"E9.sketch_text.stroke-324"),sQuery(id+"F2.wireOp",EDGE,"E9.sketch_text.stroke-325"),sQuery(id+"F2.wireOp",EDGE,"E9.sketch_text.stroke-326"),sQuery(id+"F2.wireOp",EDGE,"E9.sketch_text.stroke-327"),sQuery(id+"F2.wireOp",EDGE,"E9.sketch_text.stroke-328"),sQuery(id+"F2.wireOp",EDGE,"E9.sketch_text.stroke-329"),sQuery(id+"F2.wireOp",EDGE,"E9.sketch_text.stroke-330")])]});
            var Q67;
            Q67=makeQuery(id+"F4.opExtrude","SWEPT_BODY",BODY,{"disambiguationData":[OSD([sQuery(id+"F2.wireOp",EDGE,"E9.sketch_text.stroke-331"),sQuery(id+"F2.wireOp",EDGE,"E9.sketch_text.stroke-332"),sQuery(id+"F2.wireOp",EDGE,"E9.sketch_text.stroke-333"),sQuery(id+"F2.wireOp",EDGE,"E9.sketch_text.stroke-334"),sQuery(id+"F2.wireOp",EDGE,"E9.sketch_text.stroke-335"),sQuery(id+"F2.wireOp",EDGE,"E9.sketch_text.stroke-336"),sQuery(id+"F2.wireOp",EDGE,"E9.sketch_text.stroke-337"),sQuery(id+"F2.wireOp",EDGE,"E9.sketch_text.stroke-338"),sQuery(id+"F2.wireOp",EDGE,"E9.sketch_text.stroke-339"),sQuery(id+"F2.wireOp",EDGE,"E9.sketch_text.stroke-340"),sQuery(id+"F2.wireOp",EDGE,"E9.sketch_text.stroke-341"),sQuery(id+"F2.wireOp",EDGE,"E9.sketch_text.stroke-342"),sQuery(id+"F2.wireOp",EDGE,"E9.sketch_text.stroke-343"),sQuery(id+"F2.wireOp",EDGE,"E9.sketch_text.stroke-344"),sQuery(id+"F2.wireOp",EDGE,"E9.sketch_text.stroke-345"),sQuery(id+"F2.wireOp",EDGE,"E9.sketch_text.stroke-346"),sQuery(id+"F2.wireOp",EDGE,"E9.sketch_text.stroke-347")])]});
            var Q68;
            Q68=makeQuery(id+"F4.opExtrude","SWEPT_BODY",BODY,{"disambiguationData":[OSD([sQuery(id+"F2.wireOp",EDGE,"E9.sketch_text.stroke-348"),sQuery(id+"F2.wireOp",EDGE,"E9.sketch_text.stroke-349"),sQuery(id+"F2.wireOp",EDGE,"E9.sketch_text.stroke-350"),sQuery(id+"F2.wireOp",EDGE,"E9.sketch_text.stroke-351"),sQuery(id+"F2.wireOp",EDGE,"E9.sketch_text.stroke-352"),sQuery(id+"F2.wireOp",EDGE,"E9.sketch_text.stroke-353"),sQuery(id+"F2.wireOp",EDGE,"E9.sketch_text.stroke-354")])]});
            var Q69;
            Q69=makeQuery(id+"F4.opExtrude","SWEPT_BODY",BODY,{"disambiguationData":[OSD([sQuery(id+"F2.wireOp",EDGE,"E9.sketch_text.stroke-355"),sQuery(id+"F2.wireOp",EDGE,"E9.sketch_text.stroke-356"),sQuery(id+"F2.wireOp",EDGE,"E9.sketch_text.stroke-357"),sQuery(id+"F2.wireOp",EDGE,"E9.sketch_text.stroke-358"),sQuery(id+"F2.wireOp",EDGE,"E9.sketch_text.stroke-359"),sQuery(id+"F2.wireOp",EDGE,"E9.sketch_text.stroke-360"),sQuery(id+"F2.wireOp",EDGE,"E9.sketch_text.stroke-361"),sQuery(id+"F2.wireOp",EDGE,"E9.sketch_text.stroke-362"),sQuery(id+"F2.wireOp",EDGE,"E9.sketch_text.stroke-363"),sQuery(id+"F2.wireOp",EDGE,"E9.sketch_text.stroke-364"),sQuery(id+"F2.wireOp",EDGE,"E9.sketch_text.stroke-365"),sQuery(id+"F2.wireOp",EDGE,"E9.sketch_text.stroke-366")])]});
            var Q70;
            Q70=makeQuery(id+"F4.opExtrude","SWEPT_BODY",BODY,{"disambiguationData":[OSD([sQuery(id+"F2.wireOp",EDGE,"E9.sketch_text.stroke-367"),sQuery(id+"F2.wireOp",EDGE,"E9.sketch_text.stroke-368"),sQuery(id+"F2.wireOp",EDGE,"E9.sketch_text.stroke-369"),sQuery(id+"F2.wireOp",EDGE,"E9.sketch_text.stroke-370"),sQuery(id+"F2.wireOp",EDGE,"E9.sketch_text.stroke-371"),sQuery(id+"F2.wireOp",EDGE,"E9.sketch_text.stroke-372"),sQuery(id+"F2.wireOp",EDGE,"E9.sketch_text.stroke-373"),sQuery(id+"F2.wireOp",EDGE,"E9.sketch_text.stroke-374"),sQuery(id+"F2.wireOp",EDGE,"E9.sketch_text.stroke-375"),sQuery(id+"F2.wireOp",EDGE,"E9.sketch_text.stroke-376"),sQuery(id+"F2.wireOp",EDGE,"E9.sketch_text.stroke-377"),sQuery(id+"F2.wireOp",EDGE,"E9.sketch_text.stroke-378"),sQuery(id+"F2.wireOp",EDGE,"E9.sketch_text.stroke-379"),sQuery(id+"F2.wireOp",EDGE,"E9.sketch_text.stroke-380"),sQuery(id+"F2.wireOp",EDGE,"E9.sketch_text.stroke-381"),sQuery(id+"F2.wireOp",EDGE,"E9.sketch_text.stroke-382"),sQuery(id+"F2.wireOp",EDGE,"E9.sketch_text.stroke-383"),sQuery(id+"F2.wireOp",EDGE,"E9.sketch_text.stroke-384"),sQuery(id+"F2.wireOp",EDGE,"E9.sketch_text.stroke-385"),sQuery(id+"F2.wireOp",EDGE,"E9.sketch_text.stroke-386"),sQuery(id+"F2.wireOp",EDGE,"E9.sketch_text.stroke-387"),sQuery(id+"F2.wireOp",EDGE,"E9.sketch_text.stroke-388"),sQuery(id+"F2.wireOp",EDGE,"E9.sketch_text.stroke-389"),sQuery(id+"F2.wireOp",EDGE,"E9.sketch_text.stroke-390"),sQuery(id+"F2.wireOp",EDGE,"E9.sketch_text.stroke-391"),sQuery(id+"F2.wireOp",EDGE,"E9.sketch_text.stroke-392"),sQuery(id+"F2.wireOp",EDGE,"E9.sketch_text.stroke-393")])]});
            var Q71;
            Q71=makeQuery(id+"F4.opExtrude","SWEPT_BODY",BODY,{"disambiguationData":[OSD([sQuery(id+"F2.wireOp",EDGE,"E9.sketch_text.stroke-394"),sQuery(id+"F2.wireOp",EDGE,"E9.sketch_text.stroke-395"),sQuery(id+"F2.wireOp",EDGE,"E9.sketch_text.stroke-396"),sQuery(id+"F2.wireOp",EDGE,"E9.sketch_text.stroke-397"),sQuery(id+"F2.wireOp",EDGE,"E9.sketch_text.stroke-398"),sQuery(id+"F2.wireOp",EDGE,"E9.sketch_text.stroke-399"),sQuery(id+"F2.wireOp",EDGE,"E9.sketch_text.stroke-400"),sQuery(id+"F2.wireOp",EDGE,"E9.sketch_text.stroke-401"),sQuery(id+"F2.wireOp",EDGE,"E9.sketch_text.stroke-402"),sQuery(id+"F2.wireOp",EDGE,"E9.sketch_text.stroke-403"),sQuery(id+"F2.wireOp",EDGE,"E9.sketch_text.stroke-404"),sQuery(id+"F2.wireOp",EDGE,"E9.sketch_text.stroke-405"),sQuery(id+"F2.wireOp",EDGE,"E9.sketch_text.stroke-406")])]});
            var Q72;
            Q72=makeQuery(id+"F4.opExtrude","SWEPT_BODY",BODY,{"disambiguationData":[OSD([sQuery(id+"F2.wireOp",EDGE,"E9.sketch_text.stroke-407"),sQuery(id+"F2.wireOp",EDGE,"E9.sketch_text.stroke-408"),sQuery(id+"F2.wireOp",EDGE,"E9.sketch_text.stroke-409"),sQuery(id+"F2.wireOp",EDGE,"E9.sketch_text.stroke-410"),sQuery(id+"F2.wireOp",EDGE,"E9.sketch_text.stroke-411"),sQuery(id+"F2.wireOp",EDGE,"E9.sketch_text.stroke-412"),sQuery(id+"F2.wireOp",EDGE,"E9.sketch_text.stroke-413"),sQuery(id+"F2.wireOp",EDGE,"E9.sketch_text.stroke-414"),sQuery(id+"F2.wireOp",EDGE,"E9.sketch_text.stroke-415"),sQuery(id+"F2.wireOp",EDGE,"E9.sketch_text.stroke-416"),sQuery(id+"F2.wireOp",EDGE,"E9.sketch_text.stroke-417"),sQuery(id+"F2.wireOp",EDGE,"E9.sketch_text.stroke-418"),sQuery(id+"F2.wireOp",EDGE,"E9.sketch_text.stroke-419"),sQuery(id+"F2.wireOp",EDGE,"E9.sketch_text.stroke-420"),sQuery(id+"F2.wireOp",EDGE,"E9.sketch_text.stroke-421"),sQuery(id+"F2.wireOp",EDGE,"E9.sketch_text.stroke-422"),sQuery(id+"F2.wireOp",EDGE,"E9.sketch_text.stroke-423")])]});
            var Q73;
            Q73=makeQuery(id+"F4.opExtrude","SWEPT_BODY",BODY,{"disambiguationData":[OSD([sQuery(id+"F2.wireOp",EDGE,"E9.sketch_text.stroke-424"),sQuery(id+"F2.wireOp",EDGE,"E9.sketch_text.stroke-425"),sQuery(id+"F2.wireOp",EDGE,"E9.sketch_text.stroke-426"),sQuery(id+"F2.wireOp",EDGE,"E9.sketch_text.stroke-427")])]});
            var Q74;
            Q74=makeQuery(id+"F4.opExtrude","SWEPT_BODY",BODY,{"disambiguationData":[OSD([sQuery(id+"F2.wireOp",EDGE,"E9.sketch_text.stroke-428"),sQuery(id+"F2.wireOp",EDGE,"E9.sketch_text.stroke-429"),sQuery(id+"F2.wireOp",EDGE,"E9.sketch_text.stroke-430"),sQuery(id+"F2.wireOp",EDGE,"E9.sketch_text.stroke-431"),sQuery(id+"F2.wireOp",EDGE,"E9.sketch_text.stroke-432"),sQuery(id+"F2.wireOp",EDGE,"E9.sketch_text.stroke-433"),sQuery(id+"F2.wireOp",EDGE,"E9.sketch_text.stroke-434"),sQuery(id+"F2.wireOp",EDGE,"E9.sketch_text.stroke-435"),sQuery(id+"F2.wireOp",EDGE,"E9.sketch_text.stroke-436"),sQuery(id+"F2.wireOp",EDGE,"E9.sketch_text.stroke-437"),sQuery(id+"F2.wireOp",EDGE,"E9.sketch_text.stroke-438"),sQuery(id+"F2.wireOp",EDGE,"E9.sketch_text.stroke-439"),sQuery(id+"F2.wireOp",EDGE,"E9.sketch_text.stroke-440"),sQuery(id+"F2.wireOp",EDGE,"E9.sketch_text.stroke-441"),sQuery(id+"F2.wireOp",EDGE,"E9.sketch_text.stroke-442"),sQuery(id+"F2.wireOp",EDGE,"E9.sketch_text.stroke-443"),sQuery(id+"F2.wireOp",EDGE,"E9.sketch_text.stroke-444"),sQuery(id+"F2.wireOp",EDGE,"E9.sketch_text.stroke-445"),sQuery(id+"F2.wireOp",EDGE,"E9.sketch_text.stroke-446"),sQuery(id+"F2.wireOp",EDGE,"E9.sketch_text.stroke-447"),sQuery(id+"F2.wireOp",EDGE,"E9.sketch_text.stroke-448"),sQuery(id+"F2.wireOp",EDGE,"E9.sketch_text.stroke-449"),sQuery(id+"F2.wireOp",EDGE,"E9.sketch_text.stroke-450"),sQuery(id+"F2.wireOp",EDGE,"E9.sketch_text.stroke-451")])]});
            var Q75;
            Q75=makeQuery(id+"F4.opExtrude","SWEPT_BODY",BODY,{"disambiguationData":[OSD([sQuery(id+"F2.wireOp",EDGE,"E9.sketch_text.stroke-452"),sQuery(id+"F2.wireOp",EDGE,"E9.sketch_text.stroke-453"),sQuery(id+"F2.wireOp",EDGE,"E9.sketch_text.stroke-454"),sQuery(id+"F2.wireOp",EDGE,"E9.sketch_text.stroke-455"),sQuery(id+"F2.wireOp",EDGE,"E9.sketch_text.stroke-456"),sQuery(id+"F2.wireOp",EDGE,"E9.sketch_text.stroke-457"),sQuery(id+"F2.wireOp",EDGE,"E9.sketch_text.stroke-458"),sQuery(id+"F2.wireOp",EDGE,"E9.sketch_text.stroke-459"),sQuery(id+"F2.wireOp",EDGE,"E9.sketch_text.stroke-460"),sQuery(id+"F2.wireOp",EDGE,"E9.sketch_text.stroke-461"),sQuery(id+"F2.wireOp",EDGE,"E9.sketch_text.stroke-462"),sQuery(id+"F2.wireOp",EDGE,"E9.sketch_text.stroke-463"),sQuery(id+"F2.wireOp",EDGE,"E9.sketch_text.stroke-464"),sQuery(id+"F2.wireOp",EDGE,"E9.sketch_text.stroke-465"),sQuery(id+"F2.wireOp",EDGE,"E9.sketch_text.stroke-466"),sQuery(id+"F2.wireOp",EDGE,"E9.sketch_text.stroke-467"),sQuery(id+"F2.wireOp",EDGE,"E9.sketch_text.stroke-468"),sQuery(id+"F2.wireOp",EDGE,"E9.sketch_text.stroke-469"),sQuery(id+"F2.wireOp",EDGE,"E9.sketch_text.stroke-470"),sQuery(id+"F2.wireOp",EDGE,"E9.sketch_text.stroke-471")])]});
            var Q76;
            Q76=makeQuery(id+"F4.opExtrude","SWEPT_BODY",BODY,{"disambiguationData":[OSD([sQuery(id+"F2.wireOp",EDGE,"E9.sketch_text.stroke-472"),sQuery(id+"F2.wireOp",EDGE,"E9.sketch_text.stroke-473"),sQuery(id+"F2.wireOp",EDGE,"E9.sketch_text.stroke-474"),sQuery(id+"F2.wireOp",EDGE,"E9.sketch_text.stroke-475"),sQuery(id+"F2.wireOp",EDGE,"E9.sketch_text.stroke-476"),sQuery(id+"F2.wireOp",EDGE,"E9.sketch_text.stroke-477"),sQuery(id+"F2.wireOp",EDGE,"E9.sketch_text.stroke-478"),sQuery(id+"F2.wireOp",EDGE,"E9.sketch_text.stroke-479"),sQuery(id+"F2.wireOp",EDGE,"E9.sketch_text.stroke-480"),sQuery(id+"F2.wireOp",EDGE,"E9.sketch_text.stroke-481"),sQuery(id+"F2.wireOp",EDGE,"E9.sketch_text.stroke-482"),sQuery(id+"F2.wireOp",EDGE,"E9.sketch_text.stroke-483"),sQuery(id+"F2.wireOp",EDGE,"E9.sketch_text.stroke-484")])]});
            var Q77;
            Q77=makeQuery(id+"F4.opExtrude","SWEPT_BODY",BODY,{"disambiguationData":[OSD([sQuery(id+"F2.wireOp",EDGE,"E9.sketch_text.stroke-485"),sQuery(id+"F2.wireOp",EDGE,"E9.sketch_text.stroke-486"),sQuery(id+"F2.wireOp",EDGE,"E9.sketch_text.stroke-487"),sQuery(id+"F2.wireOp",EDGE,"E9.sketch_text.stroke-488"),sQuery(id+"F2.wireOp",EDGE,"E9.sketch_text.stroke-489"),sQuery(id+"F2.wireOp",EDGE,"E9.sketch_text.stroke-490"),sQuery(id+"F2.wireOp",EDGE,"E9.sketch_text.stroke-491"),sQuery(id+"F2.wireOp",EDGE,"E9.sketch_text.stroke-492"),sQuery(id+"F2.wireOp",EDGE,"E9.sketch_text.stroke-493"),sQuery(id+"F2.wireOp",EDGE,"E9.sketch_text.stroke-494"),sQuery(id+"F2.wireOp",EDGE,"E9.sketch_text.stroke-495"),sQuery(id+"F2.wireOp",EDGE,"E9.sketch_text.stroke-496"),sQuery(id+"F2.wireOp",EDGE,"E9.sketch_text.stroke-497"),sQuery(id+"F2.wireOp",EDGE,"E9.sketch_text.stroke-498"),sQuery(id+"F2.wireOp",EDGE,"E9.sketch_text.stroke-499"),sQuery(id+"F2.wireOp",EDGE,"E9.sketch_text.stroke-500"),sQuery(id+"F2.wireOp",EDGE,"E9.sketch_text.stroke-501"),sQuery(id+"F2.wireOp",EDGE,"E9.sketch_text.stroke-502"),sQuery(id+"F2.wireOp",EDGE,"E9.sketch_text.stroke-503")])]});
            var Q78;
            Q78=makeQuery(id+"F4.opExtrude","SWEPT_BODY",BODY,{"disambiguationData":[OSD([sQuery(id+"F2.wireOp",EDGE,"E9.sketch_text.stroke-504"),sQuery(id+"F2.wireOp",EDGE,"E9.sketch_text.stroke-505"),sQuery(id+"F2.wireOp",EDGE,"E9.sketch_text.stroke-506"),sQuery(id+"F2.wireOp",EDGE,"E9.sketch_text.stroke-507"),sQuery(id+"F2.wireOp",EDGE,"E9.sketch_text.stroke-508"),sQuery(id+"F2.wireOp",EDGE,"E9.sketch_text.stroke-509"),sQuery(id+"F2.wireOp",EDGE,"E9.sketch_text.stroke-510"),sQuery(id+"F2.wireOp",EDGE,"E9.sketch_text.stroke-511"),sQuery(id+"F2.wireOp",EDGE,"E9.sketch_text.stroke-512"),sQuery(id+"F2.wireOp",EDGE,"E9.sketch_text.stroke-513"),sQuery(id+"F2.wireOp",EDGE,"E9.sketch_text.stroke-514"),sQuery(id+"F2.wireOp",EDGE,"E9.sketch_text.stroke-515"),sQuery(id+"F2.wireOp",EDGE,"E9.sketch_text.stroke-516"),sQuery(id+"F2.wireOp",EDGE,"E9.sketch_text.stroke-517"),sQuery(id+"F2.wireOp",EDGE,"E9.sketch_text.stroke-518"),sQuery(id+"F2.wireOp",EDGE,"E9.sketch_text.stroke-519"),sQuery(id+"F2.wireOp",EDGE,"E9.sketch_text.stroke-520"),sQuery(id+"F2.wireOp",EDGE,"E9.sketch_text.stroke-521"),sQuery(id+"F2.wireOp",EDGE,"E9.sketch_text.stroke-522")])]});
            var Q79;
            Q79=makeQuery(id+"F4.opExtrude","SWEPT_BODY",BODY,{"disambiguationData":[OSD([sQuery(id+"F2.wireOp",EDGE,"E9.sketch_text.stroke-523"),sQuery(id+"F2.wireOp",EDGE,"E9.sketch_text.stroke-524"),sQuery(id+"F2.wireOp",EDGE,"E9.sketch_text.stroke-525"),sQuery(id+"F2.wireOp",EDGE,"E9.sketch_text.stroke-526"),sQuery(id+"F2.wireOp",EDGE,"E9.sketch_text.stroke-527"),sQuery(id+"F2.wireOp",EDGE,"E9.sketch_text.stroke-528"),sQuery(id+"F2.wireOp",EDGE,"E9.sketch_text.stroke-529"),sQuery(id+"F2.wireOp",EDGE,"E9.sketch_text.stroke-530"),sQuery(id+"F2.wireOp",EDGE,"E9.sketch_text.stroke-531"),sQuery(id+"F2.wireOp",EDGE,"E9.sketch_text.stroke-532"),sQuery(id+"F2.wireOp",EDGE,"E9.sketch_text.stroke-533"),sQuery(id+"F2.wireOp",EDGE,"E9.sketch_text.stroke-534"),sQuery(id+"F2.wireOp",EDGE,"E9.sketch_text.stroke-535"),sQuery(id+"F2.wireOp",EDGE,"E9.sketch_text.stroke-536"),sQuery(id+"F2.wireOp",EDGE,"E9.sketch_text.stroke-537"),sQuery(id+"F2.wireOp",EDGE,"E9.sketch_text.stroke-538"),sQuery(id+"F2.wireOp",EDGE,"E9.sketch_text.stroke-539")])]});
            var Q80;
            Q80=makeQuery(id+"F4.opExtrude","SWEPT_BODY",BODY,{"disambiguationData":[OSD([sQuery(id+"F2.wireOp",EDGE,"E9.sketch_text.stroke-540"),sQuery(id+"F2.wireOp",EDGE,"E9.sketch_text.stroke-541"),sQuery(id+"F2.wireOp",EDGE,"E9.sketch_text.stroke-542"),sQuery(id+"F2.wireOp",EDGE,"E9.sketch_text.stroke-543"),sQuery(id+"F2.wireOp",EDGE,"E9.sketch_text.stroke-544"),sQuery(id+"F2.wireOp",EDGE,"E9.sketch_text.stroke-545"),sQuery(id+"F2.wireOp",EDGE,"E9.sketch_text.stroke-546"),sQuery(id+"F2.wireOp",EDGE,"E9.sketch_text.stroke-547"),sQuery(id+"F2.wireOp",EDGE,"E9.sketch_text.stroke-548"),sQuery(id+"F2.wireOp",EDGE,"E9.sketch_text.stroke-549"),sQuery(id+"F2.wireOp",EDGE,"E9.sketch_text.stroke-550"),sQuery(id+"F2.wireOp",EDGE,"E9.sketch_text.stroke-551"),sQuery(id+"F2.wireOp",EDGE,"E9.sketch_text.stroke-552"),sQuery(id+"F2.wireOp",EDGE,"E9.sketch_text.stroke-553"),sQuery(id+"F2.wireOp",EDGE,"E9.sketch_text.stroke-554"),sQuery(id+"F2.wireOp",EDGE,"E9.sketch_text.stroke-555"),sQuery(id+"F2.wireOp",EDGE,"E9.sketch_text.stroke-556"),sQuery(id+"F2.wireOp",EDGE,"E9.sketch_text.stroke-557"),sQuery(id+"F2.wireOp",EDGE,"E9.sketch_text.stroke-558"),sQuery(id+"F2.wireOp",EDGE,"E9.sketch_text.stroke-559"),sQuery(id+"F2.wireOp",EDGE,"E9.sketch_text.stroke-560"),sQuery(id+"F2.wireOp",EDGE,"E9.sketch_text.stroke-561"),sQuery(id+"F2.wireOp",EDGE,"E9.sketch_text.stroke-562"),sQuery(id+"F2.wireOp",EDGE,"E9.sketch_text.stroke-563"),sQuery(id+"F2.wireOp",EDGE,"E9.sketch_text.stroke-564")])]});
            var Q81;
            Q81=makeQuery(id+"F4.opExtrude","SWEPT_BODY",BODY,{"disambiguationData":[OSD([sQuery(id+"F2.wireOp",EDGE,"E9.sketch_text.stroke-565"),sQuery(id+"F2.wireOp",EDGE,"E9.sketch_text.stroke-566"),sQuery(id+"F2.wireOp",EDGE,"E9.sketch_text.stroke-567"),sQuery(id+"F2.wireOp",EDGE,"E9.sketch_text.stroke-568")])]});
            var Q82;
            Q82=makeQuery(id+"F4.opExtrude","SWEPT_BODY",BODY,{"disambiguationData":[OSD([sQuery(id+"F2.wireOp",EDGE,"E9.sketch_text.stroke-569"),sQuery(id+"F2.wireOp",EDGE,"E9.sketch_text.stroke-570"),sQuery(id+"F2.wireOp",EDGE,"E9.sketch_text.stroke-571"),sQuery(id+"F2.wireOp",EDGE,"E9.sketch_text.stroke-572"),sQuery(id+"F2.wireOp",EDGE,"E9.sketch_text.stroke-573"),sQuery(id+"F2.wireOp",EDGE,"E9.sketch_text.stroke-574"),sQuery(id+"F2.wireOp",EDGE,"E9.sketch_text.stroke-575"),sQuery(id+"F2.wireOp",EDGE,"E9.sketch_text.stroke-576"),sQuery(id+"F2.wireOp",EDGE,"E9.sketch_text.stroke-577"),sQuery(id+"F2.wireOp",EDGE,"E9.sketch_text.stroke-578"),sQuery(id+"F2.wireOp",EDGE,"E9.sketch_text.stroke-579"),sQuery(id+"F2.wireOp",EDGE,"E9.sketch_text.stroke-580"),sQuery(id+"F2.wireOp",EDGE,"E9.sketch_text.stroke-581"),sQuery(id+"F2.wireOp",EDGE,"E9.sketch_text.stroke-582"),sQuery(id+"F2.wireOp",EDGE,"E9.sketch_text.stroke-583"),sQuery(id+"F2.wireOp",EDGE,"E9.sketch_text.stroke-584"),sQuery(id+"F2.wireOp",EDGE,"E9.sketch_text.stroke-585"),sQuery(id+"F2.wireOp",EDGE,"E9.sketch_text.stroke-586"),sQuery(id+"F2.wireOp",EDGE,"E9.sketch_text.stroke-587"),sQuery(id+"F2.wireOp",EDGE,"E9.sketch_text.stroke-588"),sQuery(id+"F2.wireOp",EDGE,"E9.sketch_text.stroke-589"),sQuery(id+"F2.wireOp",EDGE,"E9.sketch_text.stroke-590"),sQuery(id+"F2.wireOp",EDGE,"E9.sketch_text.stroke-591"),sQuery(id+"F2.wireOp",EDGE,"E9.sketch_text.stroke-592"),sQuery(id+"F2.wireOp",EDGE,"E9.sketch_text.stroke-593"),sQuery(id+"F2.wireOp",EDGE,"E9.sketch_text.stroke-594"),sQuery(id+"F2.wireOp",EDGE,"E9.sketch_text.stroke-595")])]});
            var Q83;
            Q83=makeQuery(id+"F4.opExtrude","SWEPT_BODY",BODY,{"disambiguationData":[OSD([sQuery(id+"F2.wireOp",EDGE,"E9.sketch_text.stroke-596"),sQuery(id+"F2.wireOp",EDGE,"E9.sketch_text.stroke-597"),sQuery(id+"F2.wireOp",EDGE,"E9.sketch_text.stroke-598"),sQuery(id+"F2.wireOp",EDGE,"E9.sketch_text.stroke-599"),sQuery(id+"F2.wireOp",EDGE,"E9.sketch_text.stroke-600"),sQuery(id+"F2.wireOp",EDGE,"E9.sketch_text.stroke-601"),sQuery(id+"F2.wireOp",EDGE,"E9.sketch_text.stroke-602"),sQuery(id+"F2.wireOp",EDGE,"E9.sketch_text.stroke-603"),sQuery(id+"F2.wireOp",EDGE,"E9.sketch_text.stroke-604"),sQuery(id+"F2.wireOp",EDGE,"E9.sketch_text.stroke-605"),sQuery(id+"F2.wireOp",EDGE,"E9.sketch_text.stroke-606"),sQuery(id+"F2.wireOp",EDGE,"E9.sketch_text.stroke-607"),sQuery(id+"F2.wireOp",EDGE,"E9.sketch_text.stroke-608"),sQuery(id+"F2.wireOp",EDGE,"E9.sketch_text.stroke-609"),sQuery(id+"F2.wireOp",EDGE,"E9.sketch_text.stroke-610"),sQuery(id+"F2.wireOp",EDGE,"E9.sketch_text.stroke-611"),sQuery(id+"F2.wireOp",EDGE,"E9.sketch_text.stroke-612"),sQuery(id+"F2.wireOp",EDGE,"E9.sketch_text.stroke-613"),sQuery(id+"F2.wireOp",EDGE,"E9.sketch_text.stroke-614"),sQuery(id+"F2.wireOp",EDGE,"E9.sketch_text.stroke-615"),sQuery(id+"F2.wireOp",EDGE,"E9.sketch_text.stroke-616"),sQuery(id+"F2.wireOp",EDGE,"E9.sketch_text.stroke-617"),sQuery(id+"F2.wireOp",EDGE,"E9.sketch_text.stroke-618"),sQuery(id+"F2.wireOp",EDGE,"E9.sketch_text.stroke-619")])]});
            var Q84;
            Q84=makeQuery(id+"F4.opExtrude","SWEPT_BODY",BODY,{"disambiguationData":[OSD([sQuery(id+"F2.wireOp",EDGE,"E9.sketch_text.stroke-620"),sQuery(id+"F2.wireOp",EDGE,"E9.sketch_text.stroke-621"),sQuery(id+"F2.wireOp",EDGE,"E9.sketch_text.stroke-622"),sQuery(id+"F2.wireOp",EDGE,"E9.sketch_text.stroke-623"),sQuery(id+"F2.wireOp",EDGE,"E9.sketch_text.stroke-624"),sQuery(id+"F2.wireOp",EDGE,"E9.sketch_text.stroke-625"),sQuery(id+"F2.wireOp",EDGE,"E9.sketch_text.stroke-626"),sQuery(id+"F2.wireOp",EDGE,"E9.sketch_text.stroke-627"),sQuery(id+"F2.wireOp",EDGE,"E9.sketch_text.stroke-628"),sQuery(id+"F2.wireOp",EDGE,"E9.sketch_text.stroke-629"),sQuery(id+"F2.wireOp",EDGE,"E9.sketch_text.stroke-630"),sQuery(id+"F2.wireOp",EDGE,"E9.sketch_text.stroke-631"),sQuery(id+"F2.wireOp",EDGE,"E9.sketch_text.stroke-632"),sQuery(id+"F2.wireOp",EDGE,"E9.sketch_text.stroke-633"),sQuery(id+"F2.wireOp",EDGE,"E9.sketch_text.stroke-634"),sQuery(id+"F2.wireOp",EDGE,"E9.sketch_text.stroke-635"),sQuery(id+"F2.wireOp",EDGE,"E9.sketch_text.stroke-636"),sQuery(id+"F2.wireOp",EDGE,"E9.sketch_text.stroke-637"),sQuery(id+"F2.wireOp",EDGE,"E9.sketch_text.stroke-638")])]});
            var Q85;
            Q85=makeQuery(id+"F4.opExtrude","SWEPT_BODY",BODY,{"disambiguationData":[OSD([sQuery(id+"F2.wireOp",EDGE,"E10.sketch_text.stroke-0"),sQuery(id+"F2.wireOp",EDGE,"E10.sketch_text.stroke-1"),sQuery(id+"F2.wireOp",EDGE,"E10.sketch_text.stroke-2"),sQuery(id+"F2.wireOp",EDGE,"E10.sketch_text.stroke-3"),sQuery(id+"F2.wireOp",EDGE,"E10.sketch_text.stroke-4"),sQuery(id+"F2.wireOp",EDGE,"E10.sketch_text.stroke-5"),sQuery(id+"F2.wireOp",EDGE,"E10.sketch_text.stroke-6"),sQuery(id+"F2.wireOp",EDGE,"E10.sketch_text.stroke-7"),sQuery(id+"F2.wireOp",EDGE,"E10.sketch_text.stroke-8"),sQuery(id+"F2.wireOp",EDGE,"E10.sketch_text.stroke-9"),sQuery(id+"F2.wireOp",EDGE,"E10.sketch_text.stroke-10"),sQuery(id+"F2.wireOp",EDGE,"E10.sketch_text.stroke-11"),sQuery(id+"F2.wireOp",EDGE,"E10.sketch_text.stroke-12"),sQuery(id+"F2.wireOp",EDGE,"E10.sketch_text.stroke-13"),sQuery(id+"F2.wireOp",EDGE,"E10.sketch_text.stroke-14"),sQuery(id+"F2.wireOp",EDGE,"E10.sketch_text.stroke-15"),sQuery(id+"F2.wireOp",EDGE,"E10.sketch_text.stroke-16"),sQuery(id+"F2.wireOp",EDGE,"E10.sketch_text.stroke-17"),sQuery(id+"F2.wireOp",EDGE,"E10.sketch_text.stroke-18"),sQuery(id+"F2.wireOp",EDGE,"E10.sketch_text.stroke-19"),sQuery(id+"F2.wireOp",EDGE,"E10.sketch_text.stroke-20"),sQuery(id+"F2.wireOp",EDGE,"E10.sketch_text.stroke-21"),sQuery(id+"F2.wireOp",EDGE,"E10.sketch_text.stroke-22"),sQuery(id+"F2.wireOp",EDGE,"E10.sketch_text.stroke-23"),sQuery(id+"F2.wireOp",EDGE,"E10.sketch_text.stroke-24"),sQuery(id+"F2.wireOp",EDGE,"E10.sketch_text.stroke-25"),sQuery(id+"F2.wireOp",EDGE,"E10.sketch_text.stroke-26")])]});
            var Q86;
            Q86=makeQuery(id+"F4.opExtrude","SWEPT_BODY",BODY,{"disambiguationData":[OSD([sQuery(id+"F2.wireOp",EDGE,"E10.sketch_text.stroke-27"),sQuery(id+"F2.wireOp",EDGE,"E10.sketch_text.stroke-28"),sQuery(id+"F2.wireOp",EDGE,"E10.sketch_text.stroke-29"),sQuery(id+"F2.wireOp",EDGE,"E10.sketch_text.stroke-30"),sQuery(id+"F2.wireOp",EDGE,"E10.sketch_text.stroke-31"),sQuery(id+"F2.wireOp",EDGE,"E10.sketch_text.stroke-32"),sQuery(id+"F2.wireOp",EDGE,"E10.sketch_text.stroke-33"),sQuery(id+"F2.wireOp",EDGE,"E10.sketch_text.stroke-34"),sQuery(id+"F2.wireOp",EDGE,"E10.sketch_text.stroke-35"),sQuery(id+"F2.wireOp",EDGE,"E10.sketch_text.stroke-36"),sQuery(id+"F2.wireOp",EDGE,"E10.sketch_text.stroke-37"),sQuery(id+"F2.wireOp",EDGE,"E10.sketch_text.stroke-38"),sQuery(id+"F2.wireOp",EDGE,"E10.sketch_text.stroke-39"),sQuery(id+"F2.wireOp",EDGE,"E10.sketch_text.stroke-40"),sQuery(id+"F2.wireOp",EDGE,"E10.sketch_text.stroke-41"),sQuery(id+"F2.wireOp",EDGE,"E10.sketch_text.stroke-42"),sQuery(id+"F2.wireOp",EDGE,"E10.sketch_text.stroke-43")])]});
            var Q87;
            Q87=makeQuery(id+"F4.opExtrude","SWEPT_BODY",BODY,{"disambiguationData":[OSD([sQuery(id+"F2.wireOp",EDGE,"E10.sketch_text.stroke-44"),sQuery(id+"F2.wireOp",EDGE,"E10.sketch_text.stroke-45"),sQuery(id+"F2.wireOp",EDGE,"E10.sketch_text.stroke-46"),sQuery(id+"F2.wireOp",EDGE,"E10.sketch_text.stroke-47"),sQuery(id+"F2.wireOp",EDGE,"E10.sketch_text.stroke-48"),sQuery(id+"F2.wireOp",EDGE,"E10.sketch_text.stroke-49"),sQuery(id+"F2.wireOp",EDGE,"E10.sketch_text.stroke-50"),sQuery(id+"F2.wireOp",EDGE,"E10.sketch_text.stroke-51"),sQuery(id+"F2.wireOp",EDGE,"E10.sketch_text.stroke-52"),sQuery(id+"F2.wireOp",EDGE,"E10.sketch_text.stroke-53"),sQuery(id+"F2.wireOp",EDGE,"E10.sketch_text.stroke-54"),sQuery(id+"F2.wireOp",EDGE,"E10.sketch_text.stroke-55"),sQuery(id+"F2.wireOp",EDGE,"E10.sketch_text.stroke-56"),sQuery(id+"F2.wireOp",EDGE,"E10.sketch_text.stroke-57"),sQuery(id+"F2.wireOp",EDGE,"E10.sketch_text.stroke-58"),sQuery(id+"F2.wireOp",EDGE,"E10.sketch_text.stroke-59"),sQuery(id+"F2.wireOp",EDGE,"E10.sketch_text.stroke-60"),sQuery(id+"F2.wireOp",EDGE,"E10.sketch_text.stroke-61"),sQuery(id+"F2.wireOp",EDGE,"E10.sketch_text.stroke-62"),sQuery(id+"F2.wireOp",EDGE,"E10.sketch_text.stroke-63"),sQuery(id+"F2.wireOp",EDGE,"E10.sketch_text.stroke-64"),sQuery(id+"F2.wireOp",EDGE,"E10.sketch_text.stroke-65"),sQuery(id+"F2.wireOp",EDGE,"E10.sketch_text.stroke-66"),sQuery(id+"F2.wireOp",EDGE,"E10.sketch_text.stroke-67")])]});
            var Q88;
            Q88=makeQuery(id+"F4.opExtrude","SWEPT_BODY",BODY,{"disambiguationData":[OSD([sQuery(id+"F2.wireOp",EDGE,"E10.sketch_text.stroke-68"),sQuery(id+"F2.wireOp",EDGE,"E10.sketch_text.stroke-69"),sQuery(id+"F2.wireOp",EDGE,"E10.sketch_text.stroke-70"),sQuery(id+"F2.wireOp",EDGE,"E10.sketch_text.stroke-71"),sQuery(id+"F2.wireOp",EDGE,"E10.sketch_text.stroke-72"),sQuery(id+"F2.wireOp",EDGE,"E10.sketch_text.stroke-73"),sQuery(id+"F2.wireOp",EDGE,"E10.sketch_text.stroke-74"),sQuery(id+"F2.wireOp",EDGE,"E10.sketch_text.stroke-75"),sQuery(id+"F2.wireOp",EDGE,"E10.sketch_text.stroke-76"),sQuery(id+"F2.wireOp",EDGE,"E10.sketch_text.stroke-77"),sQuery(id+"F2.wireOp",EDGE,"E10.sketch_text.stroke-78"),sQuery(id+"F2.wireOp",EDGE,"E10.sketch_text.stroke-79"),sQuery(id+"F2.wireOp",EDGE,"E10.sketch_text.stroke-80"),sQuery(id+"F2.wireOp",EDGE,"E10.sketch_text.stroke-81"),sQuery(id+"F2.wireOp",EDGE,"E10.sketch_text.stroke-82"),sQuery(id+"F2.wireOp",EDGE,"E10.sketch_text.stroke-83"),sQuery(id+"F2.wireOp",EDGE,"E10.sketch_text.stroke-84"),sQuery(id+"F2.wireOp",EDGE,"E10.sketch_text.stroke-85"),sQuery(id+"F2.wireOp",EDGE,"E10.sketch_text.stroke-86"),sQuery(id+"F2.wireOp",EDGE,"E10.sketch_text.stroke-87")])]});
            var Q89;
            Q89=makeQuery(id+"F4.opExtrude","SWEPT_BODY",BODY,{"disambiguationData":[OSD([sQuery(id+"F2.wireOp",EDGE,"E10.sketch_text.stroke-88"),sQuery(id+"F2.wireOp",EDGE,"E10.sketch_text.stroke-89"),sQuery(id+"F2.wireOp",EDGE,"E10.sketch_text.stroke-90"),sQuery(id+"F2.wireOp",EDGE,"E10.sketch_text.stroke-91"),sQuery(id+"F2.wireOp",EDGE,"E10.sketch_text.stroke-92"),sQuery(id+"F2.wireOp",EDGE,"E10.sketch_text.stroke-93"),sQuery(id+"F2.wireOp",EDGE,"E10.sketch_text.stroke-94"),sQuery(id+"F2.wireOp",EDGE,"E10.sketch_text.stroke-95"),sQuery(id+"F2.wireOp",EDGE,"E10.sketch_text.stroke-96"),sQuery(id+"F2.wireOp",EDGE,"E10.sketch_text.stroke-97"),sQuery(id+"F2.wireOp",EDGE,"E10.sketch_text.stroke-98"),sQuery(id+"F2.wireOp",EDGE,"E10.sketch_text.stroke-99"),sQuery(id+"F2.wireOp",EDGE,"E10.sketch_text.stroke-100"),sQuery(id+"F2.wireOp",EDGE,"E10.sketch_text.stroke-101"),sQuery(id+"F2.wireOp",EDGE,"E10.sketch_text.stroke-102"),sQuery(id+"F2.wireOp",EDGE,"E10.sketch_text.stroke-103"),sQuery(id+"F2.wireOp",EDGE,"E10.sketch_text.stroke-104"),sQuery(id+"F2.wireOp",EDGE,"E10.sketch_text.stroke-105"),sQuery(id+"F2.wireOp",EDGE,"E10.sketch_text.stroke-106"),sQuery(id+"F2.wireOp",EDGE,"E10.sketch_text.stroke-107"),sQuery(id+"F2.wireOp",EDGE,"E10.sketch_text.stroke-108"),sQuery(id+"F2.wireOp",EDGE,"E10.sketch_text.stroke-109"),sQuery(id+"F2.wireOp",EDGE,"E10.sketch_text.stroke-110"),sQuery(id+"F2.wireOp",EDGE,"E10.sketch_text.stroke-111"),sQuery(id+"F2.wireOp",EDGE,"E10.sketch_text.stroke-112"),sQuery(id+"F2.wireOp",EDGE,"E10.sketch_text.stroke-113"),sQuery(id+"F2.wireOp",EDGE,"E10.sketch_text.stroke-114")])]});
            var Q90;
            Q90=makeQuery(id+"F4.opExtrude","SWEPT_BODY",BODY,{"disambiguationData":[OSD([sQuery(id+"F2.wireOp",EDGE,"E10.sketch_text.stroke-115"),sQuery(id+"F2.wireOp",EDGE,"E10.sketch_text.stroke-116"),sQuery(id+"F2.wireOp",EDGE,"E10.sketch_text.stroke-117"),sQuery(id+"F2.wireOp",EDGE,"E10.sketch_text.stroke-118")])]});
            var Q91;
            Q91=makeQuery(id+"F4.opExtrude","SWEPT_BODY",BODY,{"disambiguationData":[OSD([sQuery(id+"F2.wireOp",EDGE,"E10.sketch_text.stroke-119"),sQuery(id+"F2.wireOp",EDGE,"E10.sketch_text.stroke-120"),sQuery(id+"F2.wireOp",EDGE,"E10.sketch_text.stroke-121"),sQuery(id+"F2.wireOp",EDGE,"E10.sketch_text.stroke-122"),sQuery(id+"F2.wireOp",EDGE,"E10.sketch_text.stroke-123"),sQuery(id+"F2.wireOp",EDGE,"E10.sketch_text.stroke-124"),sQuery(id+"F2.wireOp",EDGE,"E10.sketch_text.stroke-125"),sQuery(id+"F2.wireOp",EDGE,"E10.sketch_text.stroke-126"),sQuery(id+"F2.wireOp",EDGE,"E10.sketch_text.stroke-127"),sQuery(id+"F2.wireOp",EDGE,"E10.sketch_text.stroke-128"),sQuery(id+"F2.wireOp",EDGE,"E10.sketch_text.stroke-129"),sQuery(id+"F2.wireOp",EDGE,"E10.sketch_text.stroke-130"),sQuery(id+"F2.wireOp",EDGE,"E10.sketch_text.stroke-131"),sQuery(id+"F2.wireOp",EDGE,"E10.sketch_text.stroke-132"),sQuery(id+"F2.wireOp",EDGE,"E10.sketch_text.stroke-133"),sQuery(id+"F2.wireOp",EDGE,"E10.sketch_text.stroke-134"),sQuery(id+"F2.wireOp",EDGE,"E10.sketch_text.stroke-135"),sQuery(id+"F2.wireOp",EDGE,"E10.sketch_text.stroke-136"),sQuery(id+"F2.wireOp",EDGE,"E10.sketch_text.stroke-137")])]});
            var Q92;
            Q92=makeQuery(id+"F4.opExtrude","SWEPT_BODY",BODY,{"disambiguationData":[OSD([sQuery(id+"F2.wireOp",EDGE,"E10.sketch_text.stroke-138"),sQuery(id+"F2.wireOp",EDGE,"E10.sketch_text.stroke-139"),sQuery(id+"F2.wireOp",EDGE,"E10.sketch_text.stroke-140"),sQuery(id+"F2.wireOp",EDGE,"E10.sketch_text.stroke-141"),sQuery(id+"F2.wireOp",EDGE,"E10.sketch_text.stroke-142"),sQuery(id+"F2.wireOp",EDGE,"E10.sketch_text.stroke-143"),sQuery(id+"F2.wireOp",EDGE,"E10.sketch_text.stroke-144"),sQuery(id+"F2.wireOp",EDGE,"E10.sketch_text.stroke-145"),sQuery(id+"F2.wireOp",EDGE,"E10.sketch_text.stroke-146"),sQuery(id+"F2.wireOp",EDGE,"E10.sketch_text.stroke-147"),sQuery(id+"F2.wireOp",EDGE,"E10.sketch_text.stroke-148"),sQuery(id+"F2.wireOp",EDGE,"E10.sketch_text.stroke-149"),sQuery(id+"F2.wireOp",EDGE,"E10.sketch_text.stroke-150"),sQuery(id+"F2.wireOp",EDGE,"E10.sketch_text.stroke-151"),sQuery(id+"F2.wireOp",EDGE,"E10.sketch_text.stroke-152"),sQuery(id+"F2.wireOp",EDGE,"E10.sketch_text.stroke-153"),sQuery(id+"F2.wireOp",EDGE,"E10.sketch_text.stroke-154"),sQuery(id+"F2.wireOp",EDGE,"E10.sketch_text.stroke-155"),sQuery(id+"F2.wireOp",EDGE,"E10.sketch_text.stroke-156")])]});
            var Q93;
            Q93=makeQuery(id+"F4.opExtrude","SWEPT_BODY",BODY,{"disambiguationData":[OSD([sQuery(id+"F2.wireOp",EDGE,"E10.sketch_text.stroke-157"),sQuery(id+"F2.wireOp",EDGE,"E10.sketch_text.stroke-158"),sQuery(id+"F2.wireOp",EDGE,"E10.sketch_text.stroke-159"),sQuery(id+"F2.wireOp",EDGE,"E10.sketch_text.stroke-160"),sQuery(id+"F2.wireOp",EDGE,"E10.sketch_text.stroke-161"),sQuery(id+"F2.wireOp",EDGE,"E10.sketch_text.stroke-162"),sQuery(id+"F2.wireOp",EDGE,"E10.sketch_text.stroke-163"),sQuery(id+"F2.wireOp",EDGE,"E10.sketch_text.stroke-164"),sQuery(id+"F2.wireOp",EDGE,"E10.sketch_text.stroke-165"),sQuery(id+"F2.wireOp",EDGE,"E10.sketch_text.stroke-166"),sQuery(id+"F2.wireOp",EDGE,"E10.sketch_text.stroke-167"),sQuery(id+"F2.wireOp",EDGE,"E10.sketch_text.stroke-168"),sQuery(id+"F2.wireOp",EDGE,"E10.sketch_text.stroke-169")])]});
            var Q94;
            Q94=makeQuery(id+"F4.opExtrude","SWEPT_BODY",BODY,{"disambiguationData":[OSD([sQuery(id+"F2.wireOp",EDGE,"E10.sketch_text.stroke-170"),sQuery(id+"F2.wireOp",EDGE,"E10.sketch_text.stroke-171"),sQuery(id+"F2.wireOp",EDGE,"E10.sketch_text.stroke-172"),sQuery(id+"F2.wireOp",EDGE,"E10.sketch_text.stroke-173"),sQuery(id+"F2.wireOp",EDGE,"E10.sketch_text.stroke-174"),sQuery(id+"F2.wireOp",EDGE,"E10.sketch_text.stroke-175"),sQuery(id+"F2.wireOp",EDGE,"E10.sketch_text.stroke-176"),sQuery(id+"F2.wireOp",EDGE,"E10.sketch_text.stroke-177"),sQuery(id+"F2.wireOp",EDGE,"E10.sketch_text.stroke-178"),sQuery(id+"F2.wireOp",EDGE,"E10.sketch_text.stroke-179"),sQuery(id+"F2.wireOp",EDGE,"E10.sketch_text.stroke-180"),sQuery(id+"F2.wireOp",EDGE,"E10.sketch_text.stroke-181"),sQuery(id+"F2.wireOp",EDGE,"E10.sketch_text.stroke-182"),sQuery(id+"F2.wireOp",EDGE,"E10.sketch_text.stroke-183"),sQuery(id+"F2.wireOp",EDGE,"E10.sketch_text.stroke-184"),sQuery(id+"F2.wireOp",EDGE,"E10.sketch_text.stroke-185"),sQuery(id+"F2.wireOp",EDGE,"E10.sketch_text.stroke-186"),sQuery(id+"F2.wireOp",EDGE,"E10.sketch_text.stroke-187")])]});
            var Q95;
            Q95=makeQuery(id+"F4.opExtrude","SWEPT_BODY",BODY,{"disambiguationData":[OSD([sQuery(id+"F2.wireOp",EDGE,"E10.sketch_text.stroke-188"),sQuery(id+"F2.wireOp",EDGE,"E10.sketch_text.stroke-189"),sQuery(id+"F2.wireOp",EDGE,"E10.sketch_text.stroke-190"),sQuery(id+"F2.wireOp",EDGE,"E10.sketch_text.stroke-191"),sQuery(id+"F2.wireOp",EDGE,"E10.sketch_text.stroke-192"),sQuery(id+"F2.wireOp",EDGE,"E10.sketch_text.stroke-193"),sQuery(id+"F2.wireOp",EDGE,"E10.sketch_text.stroke-194"),sQuery(id+"F2.wireOp",EDGE,"E10.sketch_text.stroke-195"),sQuery(id+"F2.wireOp",EDGE,"E10.sketch_text.stroke-196"),sQuery(id+"F2.wireOp",EDGE,"E10.sketch_text.stroke-197"),sQuery(id+"F2.wireOp",EDGE,"E10.sketch_text.stroke-198"),sQuery(id+"F2.wireOp",EDGE,"E10.sketch_text.stroke-199"),sQuery(id+"F2.wireOp",EDGE,"E10.sketch_text.stroke-200"),sQuery(id+"F2.wireOp",EDGE,"E10.sketch_text.stroke-201"),sQuery(id+"F2.wireOp",EDGE,"E10.sketch_text.stroke-202"),sQuery(id+"F2.wireOp",EDGE,"E10.sketch_text.stroke-203"),sQuery(id+"F2.wireOp",EDGE,"E10.sketch_text.stroke-204"),sQuery(id+"F2.wireOp",EDGE,"E10.sketch_text.stroke-205"),sQuery(id+"F2.wireOp",EDGE,"E10.sketch_text.stroke-206"),sQuery(id+"F2.wireOp",EDGE,"E10.sketch_text.stroke-207"),sQuery(id+"F2.wireOp",EDGE,"E10.sketch_text.stroke-208"),sQuery(id+"F2.wireOp",EDGE,"E10.sketch_text.stroke-209"),sQuery(id+"F2.wireOp",EDGE,"E10.sketch_text.stroke-210"),sQuery(id+"F2.wireOp",EDGE,"E10.sketch_text.stroke-211"),sQuery(id+"F2.wireOp",EDGE,"E10.sketch_text.stroke-212"),sQuery(id+"F2.wireOp",EDGE,"E10.sketch_text.stroke-213"),sQuery(id+"F2.wireOp",EDGE,"E10.sketch_text.stroke-214")])]});
            var Q96;
            Q96=makeQuery(id+"F4.opExtrude","SWEPT_BODY",BODY,{"disambiguationData":[OSD([sQuery(id+"F2.wireOp",EDGE,"E10.sketch_text.stroke-215"),sQuery(id+"F2.wireOp",EDGE,"E10.sketch_text.stroke-216"),sQuery(id+"F2.wireOp",EDGE,"E10.sketch_text.stroke-217"),sQuery(id+"F2.wireOp",EDGE,"E10.sketch_text.stroke-218"),sQuery(id+"F2.wireOp",EDGE,"E10.sketch_text.stroke-219"),sQuery(id+"F2.wireOp",EDGE,"E10.sketch_text.stroke-220"),sQuery(id+"F2.wireOp",EDGE,"E10.sketch_text.stroke-221"),sQuery(id+"F2.wireOp",EDGE,"E10.sketch_text.stroke-222"),sQuery(id+"F2.wireOp",EDGE,"E10.sketch_text.stroke-223"),sQuery(id+"F2.wireOp",EDGE,"E10.sketch_text.stroke-224"),sQuery(id+"F2.wireOp",EDGE,"E10.sketch_text.stroke-225"),sQuery(id+"F2.wireOp",EDGE,"E10.sketch_text.stroke-226"),sQuery(id+"F2.wireOp",EDGE,"E10.sketch_text.stroke-227"),sQuery(id+"F2.wireOp",EDGE,"E10.sketch_text.stroke-228"),sQuery(id+"F2.wireOp",EDGE,"E10.sketch_text.stroke-229"),sQuery(id+"F2.wireOp",EDGE,"E10.sketch_text.stroke-230"),sQuery(id+"F2.wireOp",EDGE,"E10.sketch_text.stroke-231")])]});
            var Q97;
            Q97=makeQuery(id+"F4.opExtrude","SWEPT_BODY",BODY,{"disambiguationData":[OSD([sQuery(id+"F2.wireOp",EDGE,"E10.sketch_text.stroke-232"),sQuery(id+"F2.wireOp",EDGE,"E10.sketch_text.stroke-233"),sQuery(id+"F2.wireOp",EDGE,"E10.sketch_text.stroke-234"),sQuery(id+"F2.wireOp",EDGE,"E10.sketch_text.stroke-235"),sQuery(id+"F2.wireOp",EDGE,"E10.sketch_text.stroke-236"),sQuery(id+"F2.wireOp",EDGE,"E10.sketch_text.stroke-237"),sQuery(id+"F2.wireOp",EDGE,"E10.sketch_text.stroke-238"),sQuery(id+"F2.wireOp",EDGE,"E10.sketch_text.stroke-239"),sQuery(id+"F2.wireOp",EDGE,"E10.sketch_text.stroke-240"),sQuery(id+"F2.wireOp",EDGE,"E10.sketch_text.stroke-241"),sQuery(id+"F2.wireOp",EDGE,"E10.sketch_text.stroke-242"),sQuery(id+"F2.wireOp",EDGE,"E10.sketch_text.stroke-243"),sQuery(id+"F2.wireOp",EDGE,"E10.sketch_text.stroke-244"),sQuery(id+"F2.wireOp",EDGE,"E10.sketch_text.stroke-245"),sQuery(id+"F2.wireOp",EDGE,"E10.sketch_text.stroke-246"),sQuery(id+"F2.wireOp",EDGE,"E10.sketch_text.stroke-247"),sQuery(id+"F2.wireOp",EDGE,"E10.sketch_text.stroke-248"),sQuery(id+"F2.wireOp",EDGE,"E10.sketch_text.stroke-249"),sQuery(id+"F2.wireOp",EDGE,"E10.sketch_text.stroke-250"),sQuery(id+"F2.wireOp",EDGE,"E10.sketch_text.stroke-251"),sQuery(id+"F2.wireOp",EDGE,"E10.sketch_text.stroke-252"),sQuery(id+"F2.wireOp",EDGE,"E10.sketch_text.stroke-253"),sQuery(id+"F2.wireOp",EDGE,"E10.sketch_text.stroke-254"),sQuery(id+"F2.wireOp",EDGE,"E10.sketch_text.stroke-255")])]});
            var Q98;
            Q98=makeQuery(id+"F4.opExtrude","SWEPT_BODY",BODY,{"disambiguationData":[OSD([sQuery(id+"F2.wireOp",EDGE,"E10.sketch_text.stroke-256"),sQuery(id+"F2.wireOp",EDGE,"E10.sketch_text.stroke-257"),sQuery(id+"F2.wireOp",EDGE,"E10.sketch_text.stroke-258"),sQuery(id+"F2.wireOp",EDGE,"E10.sketch_text.stroke-259"),sQuery(id+"F2.wireOp",EDGE,"E10.sketch_text.stroke-260"),sQuery(id+"F2.wireOp",EDGE,"E10.sketch_text.stroke-261"),sQuery(id+"F2.wireOp",EDGE,"E10.sketch_text.stroke-262"),sQuery(id+"F2.wireOp",EDGE,"E10.sketch_text.stroke-263"),sQuery(id+"F2.wireOp",EDGE,"E10.sketch_text.stroke-264"),sQuery(id+"F2.wireOp",EDGE,"E10.sketch_text.stroke-265"),sQuery(id+"F2.wireOp",EDGE,"E10.sketch_text.stroke-266"),sQuery(id+"F2.wireOp",EDGE,"E10.sketch_text.stroke-267"),sQuery(id+"F2.wireOp",EDGE,"E10.sketch_text.stroke-268"),sQuery(id+"F2.wireOp",EDGE,"E10.sketch_text.stroke-269"),sQuery(id+"F2.wireOp",EDGE,"E10.sketch_text.stroke-270"),sQuery(id+"F2.wireOp",EDGE,"E10.sketch_text.stroke-271"),sQuery(id+"F2.wireOp",EDGE,"E10.sketch_text.stroke-272")])]});
            var Q99;
            Q99=makeQuery(id+"F4.opExtrude","SWEPT_BODY",BODY,{"disambiguationData":[OSD([sQuery(id+"F2.wireOp",EDGE,"E10.sketch_text.stroke-273"),sQuery(id+"F2.wireOp",EDGE,"E10.sketch_text.stroke-274"),sQuery(id+"F2.wireOp",EDGE,"E10.sketch_text.stroke-275"),sQuery(id+"F2.wireOp",EDGE,"E10.sketch_text.stroke-276")])]});
            var Q100;
            Q100=makeQuery(id+"F4.opExtrude","SWEPT_BODY",BODY,{"disambiguationData":[OSD([sQuery(id+"F2.wireOp",EDGE,"E10.sketch_text.stroke-277"),sQuery(id+"F2.wireOp",EDGE,"E10.sketch_text.stroke-278"),sQuery(id+"F2.wireOp",EDGE,"E10.sketch_text.stroke-279"),sQuery(id+"F2.wireOp",EDGE,"E10.sketch_text.stroke-280"),sQuery(id+"F2.wireOp",EDGE,"E10.sketch_text.stroke-281"),sQuery(id+"F2.wireOp",EDGE,"E10.sketch_text.stroke-282"),sQuery(id+"F2.wireOp",EDGE,"E10.sketch_text.stroke-283"),sQuery(id+"F2.wireOp",EDGE,"E10.sketch_text.stroke-284"),sQuery(id+"F2.wireOp",EDGE,"E10.sketch_text.stroke-285"),sQuery(id+"F2.wireOp",EDGE,"E10.sketch_text.stroke-286"),sQuery(id+"F2.wireOp",EDGE,"E10.sketch_text.stroke-287"),sQuery(id+"F2.wireOp",EDGE,"E10.sketch_text.stroke-288"),sQuery(id+"F2.wireOp",EDGE,"E10.sketch_text.stroke-289"),sQuery(id+"F2.wireOp",EDGE,"E10.sketch_text.stroke-290"),sQuery(id+"F2.wireOp",EDGE,"E10.sketch_text.stroke-291"),sQuery(id+"F2.wireOp",EDGE,"E10.sketch_text.stroke-292"),sQuery(id+"F2.wireOp",EDGE,"E10.sketch_text.stroke-293"),sQuery(id+"F2.wireOp",EDGE,"E10.sketch_text.stroke-294"),sQuery(id+"F2.wireOp",EDGE,"E10.sketch_text.stroke-295"),sQuery(id+"F2.wireOp",EDGE,"E10.sketch_text.stroke-296"),sQuery(id+"F2.wireOp",EDGE,"E10.sketch_text.stroke-297"),sQuery(id+"F2.wireOp",EDGE,"E10.sketch_text.stroke-298"),sQuery(id+"F2.wireOp",EDGE,"E10.sketch_text.stroke-299"),sQuery(id+"F2.wireOp",EDGE,"E10.sketch_text.stroke-300"),sQuery(id+"F2.wireOp",EDGE,"E10.sketch_text.stroke-301")])]});
            var Q101;
            Q101=makeQuery(id+"F4.opExtrude","SWEPT_BODY",BODY,{"disambiguationData":[OSD([sQuery(id+"F2.wireOp",EDGE,"E10.sketch_text.stroke-302"),sQuery(id+"F2.wireOp",EDGE,"E10.sketch_text.stroke-303"),sQuery(id+"F2.wireOp",EDGE,"E10.sketch_text.stroke-304"),sQuery(id+"F2.wireOp",EDGE,"E10.sketch_text.stroke-305"),sQuery(id+"F2.wireOp",EDGE,"E10.sketch_text.stroke-306"),sQuery(id+"F2.wireOp",EDGE,"E10.sketch_text.stroke-307"),sQuery(id+"F2.wireOp",EDGE,"E10.sketch_text.stroke-308"),sQuery(id+"F2.wireOp",EDGE,"E10.sketch_text.stroke-309"),sQuery(id+"F2.wireOp",EDGE,"E10.sketch_text.stroke-310"),sQuery(id+"F2.wireOp",EDGE,"E10.sketch_text.stroke-311"),sQuery(id+"F2.wireOp",EDGE,"E10.sketch_text.stroke-312"),sQuery(id+"F2.wireOp",EDGE,"E10.sketch_text.stroke-313"),sQuery(id+"F2.wireOp",EDGE,"E10.sketch_text.stroke-314"),sQuery(id+"F2.wireOp",EDGE,"E10.sketch_text.stroke-315"),sQuery(id+"F2.wireOp",EDGE,"E10.sketch_text.stroke-316"),sQuery(id+"F2.wireOp",EDGE,"E10.sketch_text.stroke-317"),sQuery(id+"F2.wireOp",EDGE,"E10.sketch_text.stroke-318"),sQuery(id+"F2.wireOp",EDGE,"E10.sketch_text.stroke-319")])]});
            var Q102;
            Q102=makeQuery(id+"F4.opExtrude","SWEPT_BODY",BODY,{"disambiguationData":[OSD([sQuery(id+"F2.wireOp",EDGE,"E10.sketch_text.stroke-320"),sQuery(id+"F2.wireOp",EDGE,"E10.sketch_text.stroke-321"),sQuery(id+"F2.wireOp",EDGE,"E10.sketch_text.stroke-322"),sQuery(id+"F2.wireOp",EDGE,"E10.sketch_text.stroke-323"),sQuery(id+"F2.wireOp",EDGE,"E10.sketch_text.stroke-324"),sQuery(id+"F2.wireOp",EDGE,"E10.sketch_text.stroke-325"),sQuery(id+"F2.wireOp",EDGE,"E10.sketch_text.stroke-326"),sQuery(id+"F2.wireOp",EDGE,"E10.sketch_text.stroke-327"),sQuery(id+"F2.wireOp",EDGE,"E10.sketch_text.stroke-328"),sQuery(id+"F2.wireOp",EDGE,"E10.sketch_text.stroke-329"),sQuery(id+"F2.wireOp",EDGE,"E10.sketch_text.stroke-330"),sQuery(id+"F2.wireOp",EDGE,"E10.sketch_text.stroke-331"),sQuery(id+"F2.wireOp",EDGE,"E10.sketch_text.stroke-332"),sQuery(id+"F2.wireOp",EDGE,"E10.sketch_text.stroke-333"),sQuery(id+"F2.wireOp",EDGE,"E10.sketch_text.stroke-334"),sQuery(id+"F2.wireOp",EDGE,"E10.sketch_text.stroke-335"),sQuery(id+"F2.wireOp",EDGE,"E10.sketch_text.stroke-336"),sQuery(id+"F2.wireOp",EDGE,"E10.sketch_text.stroke-337"),sQuery(id+"F2.wireOp",EDGE,"E10.sketch_text.stroke-338")])]});
            var Q103;
            Q103=makeQuery(id+"F4.opExtrude","SWEPT_BODY",BODY,{"disambiguationData":[OSD([sQuery(id+"F2.wireOp",EDGE,"E10.sketch_text.stroke-339"),sQuery(id+"F2.wireOp",EDGE,"E10.sketch_text.stroke-340"),sQuery(id+"F2.wireOp",EDGE,"E10.sketch_text.stroke-341"),sQuery(id+"F2.wireOp",EDGE,"E10.sketch_text.stroke-342"),sQuery(id+"F2.wireOp",EDGE,"E10.sketch_text.stroke-343"),sQuery(id+"F2.wireOp",EDGE,"E10.sketch_text.stroke-344"),sQuery(id+"F2.wireOp",EDGE,"E10.sketch_text.stroke-345"),sQuery(id+"F2.wireOp",EDGE,"E10.sketch_text.stroke-346"),sQuery(id+"F2.wireOp",EDGE,"E10.sketch_text.stroke-347"),sQuery(id+"F2.wireOp",EDGE,"E10.sketch_text.stroke-348"),sQuery(id+"F2.wireOp",EDGE,"E10.sketch_text.stroke-349"),sQuery(id+"F2.wireOp",EDGE,"E10.sketch_text.stroke-350"),sQuery(id+"F2.wireOp",EDGE,"E10.sketch_text.stroke-351"),sQuery(id+"F2.wireOp",EDGE,"E10.sketch_text.stroke-352"),sQuery(id+"F2.wireOp",EDGE,"E10.sketch_text.stroke-353"),sQuery(id+"F2.wireOp",EDGE,"E10.sketch_text.stroke-354"),sQuery(id+"F2.wireOp",EDGE,"E10.sketch_text.stroke-355")])]});
            var Q104;
            Q104=makeQuery(id+"F4.opExtrude","SWEPT_BODY",BODY,{"disambiguationData":[OSD([sQuery(id+"F2.wireOp",EDGE,"E10.sketch_text.stroke-356"),sQuery(id+"F2.wireOp",EDGE,"E10.sketch_text.stroke-357"),sQuery(id+"F2.wireOp",EDGE,"E10.sketch_text.stroke-358"),sQuery(id+"F2.wireOp",EDGE,"E10.sketch_text.stroke-359")])]});
            var Q105;
            Q105=makeQuery(id+"F4.opExtrude","SWEPT_BODY",BODY,{"disambiguationData":[OSD([sQuery(id+"F2.wireOp",EDGE,"E10.sketch_text.stroke-360"),sQuery(id+"F2.wireOp",EDGE,"E10.sketch_text.stroke-361"),sQuery(id+"F2.wireOp",EDGE,"E10.sketch_text.stroke-362"),sQuery(id+"F2.wireOp",EDGE,"E10.sketch_text.stroke-363"),sQuery(id+"F2.wireOp",EDGE,"E10.sketch_text.stroke-364"),sQuery(id+"F2.wireOp",EDGE,"E10.sketch_text.stroke-365"),sQuery(id+"F2.wireOp",EDGE,"E10.sketch_text.stroke-366"),sQuery(id+"F2.wireOp",EDGE,"E10.sketch_text.stroke-367")])]});
            var Q106;
            Q106=makeQuery(id+"F4.opExtrude","SWEPT_BODY",BODY,{"disambiguationData":[OSD([sQuery(id+"F2.wireOp",EDGE,"E10.sketch_text.stroke-368"),sQuery(id+"F2.wireOp",EDGE,"E10.sketch_text.stroke-369"),sQuery(id+"F2.wireOp",EDGE,"E10.sketch_text.stroke-370"),sQuery(id+"F2.wireOp",EDGE,"E10.sketch_text.stroke-371"),sQuery(id+"F2.wireOp",EDGE,"E10.sketch_text.stroke-372"),sQuery(id+"F2.wireOp",EDGE,"E10.sketch_text.stroke-373"),sQuery(id+"F2.wireOp",EDGE,"E10.sketch_text.stroke-374"),sQuery(id+"F2.wireOp",EDGE,"E10.sketch_text.stroke-375"),sQuery(id+"F2.wireOp",EDGE,"E10.sketch_text.stroke-376"),sQuery(id+"F2.wireOp",EDGE,"E10.sketch_text.stroke-377"),sQuery(id+"F2.wireOp",EDGE,"E10.sketch_text.stroke-378"),sQuery(id+"F2.wireOp",EDGE,"E10.sketch_text.stroke-379"),sQuery(id+"F2.wireOp",EDGE,"E10.sketch_text.stroke-380"),sQuery(id+"F2.wireOp",EDGE,"E10.sketch_text.stroke-381"),sQuery(id+"F2.wireOp",EDGE,"E10.sketch_text.stroke-382"),sQuery(id+"F2.wireOp",EDGE,"E10.sketch_text.stroke-383"),sQuery(id+"F2.wireOp",EDGE,"E10.sketch_text.stroke-384")])]});
            var Q107;
            Q107=makeQuery(id+"F4.opExtrude","SWEPT_BODY",BODY,{"disambiguationData":[OSD([sQuery(id+"F2.wireOp",EDGE,"E10.sketch_text.stroke-385"),sQuery(id+"F2.wireOp",EDGE,"E10.sketch_text.stroke-386"),sQuery(id+"F2.wireOp",EDGE,"E10.sketch_text.stroke-387"),sQuery(id+"F2.wireOp",EDGE,"E10.sketch_text.stroke-388"),sQuery(id+"F2.wireOp",EDGE,"E10.sketch_text.stroke-389"),sQuery(id+"F2.wireOp",EDGE,"E10.sketch_text.stroke-390"),sQuery(id+"F2.wireOp",EDGE,"E10.sketch_text.stroke-391"),sQuery(id+"F2.wireOp",EDGE,"E10.sketch_text.stroke-392"),sQuery(id+"F2.wireOp",EDGE,"E10.sketch_text.stroke-393"),sQuery(id+"F2.wireOp",EDGE,"E10.sketch_text.stroke-394"),sQuery(id+"F2.wireOp",EDGE,"E10.sketch_text.stroke-395"),sQuery(id+"F2.wireOp",EDGE,"E10.sketch_text.stroke-396"),sQuery(id+"F2.wireOp",EDGE,"E10.sketch_text.stroke-397"),sQuery(id+"F2.wireOp",EDGE,"E10.sketch_text.stroke-398"),sQuery(id+"F2.wireOp",EDGE,"E10.sketch_text.stroke-399"),sQuery(id+"F2.wireOp",EDGE,"E10.sketch_text.stroke-400"),sQuery(id+"F2.wireOp",EDGE,"E10.sketch_text.stroke-401"),sQuery(id+"F2.wireOp",EDGE,"E10.sketch_text.stroke-402"),sQuery(id+"F2.wireOp",EDGE,"E10.sketch_text.stroke-403")])]});
            var Q108;
            Q108=makeQuery(id+"F4.opExtrude","SWEPT_BODY",BODY,{"disambiguationData":[OSD([sQuery(id+"F2.wireOp",EDGE,"E10.sketch_text.stroke-404"),sQuery(id+"F2.wireOp",EDGE,"E10.sketch_text.stroke-405"),sQuery(id+"F2.wireOp",EDGE,"E10.sketch_text.stroke-406"),sQuery(id+"F2.wireOp",EDGE,"E10.sketch_text.stroke-407"),sQuery(id+"F2.wireOp",EDGE,"E10.sketch_text.stroke-408"),sQuery(id+"F2.wireOp",EDGE,"E10.sketch_text.stroke-409"),sQuery(id+"F2.wireOp",EDGE,"E10.sketch_text.stroke-410"),sQuery(id+"F2.wireOp",EDGE,"E10.sketch_text.stroke-411"),sQuery(id+"F2.wireOp",EDGE,"E10.sketch_text.stroke-412"),sQuery(id+"F2.wireOp",EDGE,"E10.sketch_text.stroke-413"),sQuery(id+"F2.wireOp",EDGE,"E10.sketch_text.stroke-414"),sQuery(id+"F2.wireOp",EDGE,"E10.sketch_text.stroke-415"),sQuery(id+"F2.wireOp",EDGE,"E10.sketch_text.stroke-416"),sQuery(id+"F2.wireOp",EDGE,"E10.sketch_text.stroke-417"),sQuery(id+"F2.wireOp",EDGE,"E10.sketch_text.stroke-418"),sQuery(id+"F2.wireOp",EDGE,"E10.sketch_text.stroke-419"),sQuery(id+"F2.wireOp",EDGE,"E10.sketch_text.stroke-420"),sQuery(id+"F2.wireOp",EDGE,"E10.sketch_text.stroke-421"),sQuery(id+"F2.wireOp",EDGE,"E10.sketch_text.stroke-422")])]});
            var Q109;
            Q109=makeQuery(id+"F4.opExtrude","SWEPT_BODY",BODY,{"disambiguationData":[OSD([sQuery(id+"F2.wireOp",EDGE,"E10.sketch_text.stroke-423"),sQuery(id+"F2.wireOp",EDGE,"E10.sketch_text.stroke-424"),sQuery(id+"F2.wireOp",EDGE,"E10.sketch_text.stroke-425"),sQuery(id+"F2.wireOp",EDGE,"E10.sketch_text.stroke-426"),sQuery(id+"F2.wireOp",EDGE,"E10.sketch_text.stroke-427"),sQuery(id+"F2.wireOp",EDGE,"E10.sketch_text.stroke-428"),sQuery(id+"F2.wireOp",EDGE,"E10.sketch_text.stroke-429"),sQuery(id+"F2.wireOp",EDGE,"E10.sketch_text.stroke-430"),sQuery(id+"F2.wireOp",EDGE,"E10.sketch_text.stroke-431"),sQuery(id+"F2.wireOp",EDGE,"E10.sketch_text.stroke-432"),sQuery(id+"F2.wireOp",EDGE,"E10.sketch_text.stroke-433"),sQuery(id+"F2.wireOp",EDGE,"E10.sketch_text.stroke-434"),sQuery(id+"F2.wireOp",EDGE,"E10.sketch_text.stroke-435")])]});
            var Q110;
            Q110=makeQuery(id+"F4.opExtrude","SWEPT_BODY",BODY,{"disambiguationData":[OSD([sQuery(id+"F2.wireOp",EDGE,"E10.sketch_text.stroke-436"),sQuery(id+"F2.wireOp",EDGE,"E10.sketch_text.stroke-437"),sQuery(id+"F2.wireOp",EDGE,"E10.sketch_text.stroke-438"),sQuery(id+"F2.wireOp",EDGE,"E10.sketch_text.stroke-439")])]});
            var Q111;
            Q111=makeQuery(id+"F4.opExtrude","SWEPT_BODY",BODY,{"disambiguationData":[OSD([sQuery(id+"F2.wireOp",EDGE,"E10.sketch_text.stroke-440"),sQuery(id+"F2.wireOp",EDGE,"E10.sketch_text.stroke-441"),sQuery(id+"F2.wireOp",EDGE,"E10.sketch_text.stroke-442"),sQuery(id+"F2.wireOp",EDGE,"E10.sketch_text.stroke-443"),sQuery(id+"F2.wireOp",EDGE,"E10.sketch_text.stroke-444"),sQuery(id+"F2.wireOp",EDGE,"E10.sketch_text.stroke-445"),sQuery(id+"F2.wireOp",EDGE,"E10.sketch_text.stroke-446"),sQuery(id+"F2.wireOp",EDGE,"E10.sketch_text.stroke-447")])]});
            var Q112;
            Q112=makeQuery(id+"F4.opExtrude","SWEPT_BODY",BODY,{"disambiguationData":[OSD([sQuery(id+"F2.wireOp",EDGE,"E10.sketch_text.stroke-448"),sQuery(id+"F2.wireOp",EDGE,"E10.sketch_text.stroke-449"),sQuery(id+"F2.wireOp",EDGE,"E10.sketch_text.stroke-450"),sQuery(id+"F2.wireOp",EDGE,"E10.sketch_text.stroke-451"),sQuery(id+"F2.wireOp",EDGE,"E10.sketch_text.stroke-452"),sQuery(id+"F2.wireOp",EDGE,"E10.sketch_text.stroke-453"),sQuery(id+"F2.wireOp",EDGE,"E10.sketch_text.stroke-454"),sQuery(id+"F2.wireOp",EDGE,"E10.sketch_text.stroke-455"),sQuery(id+"F2.wireOp",EDGE,"E10.sketch_text.stroke-456"),sQuery(id+"F2.wireOp",EDGE,"E10.sketch_text.stroke-457"),sQuery(id+"F2.wireOp",EDGE,"E10.sketch_text.stroke-458"),sQuery(id+"F2.wireOp",EDGE,"E10.sketch_text.stroke-459"),sQuery(id+"F2.wireOp",EDGE,"E10.sketch_text.stroke-460"),sQuery(id+"F2.wireOp",EDGE,"E10.sketch_text.stroke-461"),sQuery(id+"F2.wireOp",EDGE,"E10.sketch_text.stroke-462"),sQuery(id+"F2.wireOp",EDGE,"E10.sketch_text.stroke-463"),sQuery(id+"F2.wireOp",EDGE,"E10.sketch_text.stroke-464")])]});
            var Q113;
            Q113=makeQuery(id+"F4.opExtrude","SWEPT_BODY",BODY,{"disambiguationData":[OSD([sQuery(id+"F2.wireOp",EDGE,"E10.sketch_text.stroke-465"),sQuery(id+"F2.wireOp",EDGE,"E10.sketch_text.stroke-466"),sQuery(id+"F2.wireOp",EDGE,"E10.sketch_text.stroke-467"),sQuery(id+"F2.wireOp",EDGE,"E10.sketch_text.stroke-468"),sQuery(id+"F2.wireOp",EDGE,"E10.sketch_text.stroke-469"),sQuery(id+"F2.wireOp",EDGE,"E10.sketch_text.stroke-470"),sQuery(id+"F2.wireOp",EDGE,"E10.sketch_text.stroke-471"),sQuery(id+"F2.wireOp",EDGE,"E10.sketch_text.stroke-472"),sQuery(id+"F2.wireOp",EDGE,"E10.sketch_text.stroke-473"),sQuery(id+"F2.wireOp",EDGE,"E10.sketch_text.stroke-474"),sQuery(id+"F2.wireOp",EDGE,"E10.sketch_text.stroke-475"),sQuery(id+"F2.wireOp",EDGE,"E10.sketch_text.stroke-476"),sQuery(id+"F2.wireOp",EDGE,"E10.sketch_text.stroke-477")])]});
            var Q114;
            Q114=makeQuery(id+"F4.opExtrude","SWEPT_BODY",BODY,{"disambiguationData":[OSD([sQuery(id+"F2.wireOp",EDGE,"E10.sketch_text.stroke-478"),sQuery(id+"F2.wireOp",EDGE,"E10.sketch_text.stroke-479"),sQuery(id+"F2.wireOp",EDGE,"E10.sketch_text.stroke-480"),sQuery(id+"F2.wireOp",EDGE,"E10.sketch_text.stroke-481"),sQuery(id+"F2.wireOp",EDGE,"E10.sketch_text.stroke-482"),sQuery(id+"F2.wireOp",EDGE,"E10.sketch_text.stroke-483"),sQuery(id+"F2.wireOp",EDGE,"E10.sketch_text.stroke-484"),sQuery(id+"F2.wireOp",EDGE,"E10.sketch_text.stroke-485"),sQuery(id+"F2.wireOp",EDGE,"E10.sketch_text.stroke-486"),sQuery(id+"F2.wireOp",EDGE,"E10.sketch_text.stroke-487"),sQuery(id+"F2.wireOp",EDGE,"E10.sketch_text.stroke-488"),sQuery(id+"F2.wireOp",EDGE,"E10.sketch_text.stroke-489"),sQuery(id+"F2.wireOp",EDGE,"E10.sketch_text.stroke-490"),sQuery(id+"F2.wireOp",EDGE,"E10.sketch_text.stroke-491"),sQuery(id+"F2.wireOp",EDGE,"E10.sketch_text.stroke-492"),sQuery(id+"F2.wireOp",EDGE,"E10.sketch_text.stroke-493"),sQuery(id+"F2.wireOp",EDGE,"E10.sketch_text.stroke-494"),sQuery(id+"F2.wireOp",EDGE,"E10.sketch_text.stroke-495"),sQuery(id+"F2.wireOp",EDGE,"E10.sketch_text.stroke-496"),sQuery(id+"F2.wireOp",EDGE,"E10.sketch_text.stroke-497"),sQuery(id+"F2.wireOp",EDGE,"E10.sketch_text.stroke-498"),sQuery(id+"F2.wireOp",EDGE,"E10.sketch_text.stroke-499"),sQuery(id+"F2.wireOp",EDGE,"E10.sketch_text.stroke-500"),sQuery(id+"F2.wireOp",EDGE,"E10.sketch_text.stroke-501"),sQuery(id+"F2.wireOp",EDGE,"E10.sketch_text.stroke-502"),sQuery(id+"F2.wireOp",EDGE,"E10.sketch_text.stroke-503"),sQuery(id+"F2.wireOp",EDGE,"E10.sketch_text.stroke-504")])]});
            var Q115;
            Q115=makeQuery(id+"F4.opExtrude","SWEPT_BODY",BODY,{"disambiguationData":[OSD([sQuery(id+"F2.wireOp",EDGE,"E10.sketch_text.stroke-505"),sQuery(id+"F2.wireOp",EDGE,"E10.sketch_text.stroke-506"),sQuery(id+"F2.wireOp",EDGE,"E10.sketch_text.stroke-507"),sQuery(id+"F2.wireOp",EDGE,"E10.sketch_text.stroke-508"),sQuery(id+"F2.wireOp",EDGE,"E10.sketch_text.stroke-509"),sQuery(id+"F2.wireOp",EDGE,"E10.sketch_text.stroke-510"),sQuery(id+"F2.wireOp",EDGE,"E10.sketch_text.stroke-511"),sQuery(id+"F2.wireOp",EDGE,"E10.sketch_text.stroke-512"),sQuery(id+"F2.wireOp",EDGE,"E10.sketch_text.stroke-513"),sQuery(id+"F2.wireOp",EDGE,"E10.sketch_text.stroke-514"),sQuery(id+"F2.wireOp",EDGE,"E10.sketch_text.stroke-515"),sQuery(id+"F2.wireOp",EDGE,"E10.sketch_text.stroke-516"),sQuery(id+"F2.wireOp",EDGE,"E10.sketch_text.stroke-517"),sQuery(id+"F2.wireOp",EDGE,"E10.sketch_text.stroke-518"),sQuery(id+"F2.wireOp",EDGE,"E10.sketch_text.stroke-519"),sQuery(id+"F2.wireOp",EDGE,"E10.sketch_text.stroke-520"),sQuery(id+"F2.wireOp",EDGE,"E10.sketch_text.stroke-521")])]});
            var Q116;
            Q116=makeQuery(id+"F4.opExtrude","SWEPT_BODY",BODY,{"disambiguationData":[OSD([sQuery(id+"F2.wireOp",EDGE,"E10.sketch_text.stroke-522"),sQuery(id+"F2.wireOp",EDGE,"E10.sketch_text.stroke-523"),sQuery(id+"F2.wireOp",EDGE,"E10.sketch_text.stroke-524"),sQuery(id+"F2.wireOp",EDGE,"E10.sketch_text.stroke-525"),sQuery(id+"F2.wireOp",EDGE,"E10.sketch_text.stroke-526"),sQuery(id+"F2.wireOp",EDGE,"E10.sketch_text.stroke-527"),sQuery(id+"F2.wireOp",EDGE,"E10.sketch_text.stroke-528"),sQuery(id+"F2.wireOp",EDGE,"E10.sketch_text.stroke-529"),sQuery(id+"F2.wireOp",EDGE,"E10.sketch_text.stroke-530"),sQuery(id+"F2.wireOp",EDGE,"E10.sketch_text.stroke-531"),sQuery(id+"F2.wireOp",EDGE,"E10.sketch_text.stroke-532"),sQuery(id+"F2.wireOp",EDGE,"E10.sketch_text.stroke-533"),sQuery(id+"F2.wireOp",EDGE,"E10.sketch_text.stroke-534"),sQuery(id+"F2.wireOp",EDGE,"E10.sketch_text.stroke-535"),sQuery(id+"F2.wireOp",EDGE,"E10.sketch_text.stroke-536"),sQuery(id+"F2.wireOp",EDGE,"E10.sketch_text.stroke-537"),sQuery(id+"F2.wireOp",EDGE,"E10.sketch_text.stroke-538"),sQuery(id+"F2.wireOp",EDGE,"E10.sketch_text.stroke-539"),sQuery(id+"F2.wireOp",EDGE,"E10.sketch_text.stroke-540"),sQuery(id+"F2.wireOp",EDGE,"E10.sketch_text.stroke-541"),sQuery(id+"F2.wireOp",EDGE,"E10.sketch_text.stroke-542"),sQuery(id+"F2.wireOp",EDGE,"E10.sketch_text.stroke-543"),sQuery(id+"F2.wireOp",EDGE,"E10.sketch_text.stroke-544"),sQuery(id+"F2.wireOp",EDGE,"E10.sketch_text.stroke-545")])]});
            var Q117;
            Q117=makeQuery(id+"F4.opExtrude","SWEPT_BODY",BODY,{"disambiguationData":[OSD([sQuery(id+"F2.wireOp",EDGE,"E11.sketch_text.stroke-0"),sQuery(id+"F2.wireOp",EDGE,"E11.sketch_text.stroke-1"),sQuery(id+"F2.wireOp",EDGE,"E11.sketch_text.stroke-2"),sQuery(id+"F2.wireOp",EDGE,"E11.sketch_text.stroke-3"),sQuery(id+"F2.wireOp",EDGE,"E11.sketch_text.stroke-4"),sQuery(id+"F2.wireOp",EDGE,"E11.sketch_text.stroke-5"),sQuery(id+"F2.wireOp",EDGE,"E11.sketch_text.stroke-6"),sQuery(id+"F2.wireOp",EDGE,"E11.sketch_text.stroke-7"),sQuery(id+"F2.wireOp",EDGE,"E11.sketch_text.stroke-8"),sQuery(id+"F2.wireOp",EDGE,"E11.sketch_text.stroke-9"),sQuery(id+"F2.wireOp",EDGE,"E11.sketch_text.stroke-10"),sQuery(id+"F2.wireOp",EDGE,"E11.sketch_text.stroke-11"),sQuery(id+"F2.wireOp",EDGE,"E11.sketch_text.stroke-12"),sQuery(id+"F2.wireOp",EDGE,"E11.sketch_text.stroke-13"),sQuery(id+"F2.wireOp",EDGE,"E11.sketch_text.stroke-14"),sQuery(id+"F2.wireOp",EDGE,"E11.sketch_text.stroke-15"),sQuery(id+"F2.wireOp",EDGE,"E11.sketch_text.stroke-16"),sQuery(id+"F2.wireOp",EDGE,"E11.sketch_text.stroke-17"),sQuery(id+"F2.wireOp",EDGE,"E11.sketch_text.stroke-18")])]});
            var Q118;
            Q118=makeQuery(id+"F4.opExtrude","SWEPT_BODY",BODY,{"disambiguationData":[OSD([sQuery(id+"F2.wireOp",EDGE,"E11.sketch_text.stroke-19"),sQuery(id+"F2.wireOp",EDGE,"E11.sketch_text.stroke-20"),sQuery(id+"F2.wireOp",EDGE,"E11.sketch_text.stroke-21"),sQuery(id+"F2.wireOp",EDGE,"E11.sketch_text.stroke-22"),sQuery(id+"F2.wireOp",EDGE,"E11.sketch_text.stroke-23"),sQuery(id+"F2.wireOp",EDGE,"E11.sketch_text.stroke-24"),sQuery(id+"F2.wireOp",EDGE,"E11.sketch_text.stroke-25"),sQuery(id+"F2.wireOp",EDGE,"E11.sketch_text.stroke-26"),sQuery(id+"F2.wireOp",EDGE,"E11.sketch_text.stroke-27"),sQuery(id+"F2.wireOp",EDGE,"E11.sketch_text.stroke-28"),sQuery(id+"F2.wireOp",EDGE,"E11.sketch_text.stroke-29"),sQuery(id+"F2.wireOp",EDGE,"E11.sketch_text.stroke-30")])]});
            var Q119;
            Q119=makeQuery(id+"F4.opExtrude","SWEPT_BODY",BODY,{"disambiguationData":[OSD([sQuery(id+"F2.wireOp",EDGE,"E11.sketch_text.stroke-31"),sQuery(id+"F2.wireOp",EDGE,"E11.sketch_text.stroke-32"),sQuery(id+"F2.wireOp",EDGE,"E11.sketch_text.stroke-33"),sQuery(id+"F2.wireOp",EDGE,"E11.sketch_text.stroke-34"),sQuery(id+"F2.wireOp",EDGE,"E11.sketch_text.stroke-35"),sQuery(id+"F2.wireOp",EDGE,"E11.sketch_text.stroke-36"),sQuery(id+"F2.wireOp",EDGE,"E11.sketch_text.stroke-37"),sQuery(id+"F2.wireOp",EDGE,"E11.sketch_text.stroke-38"),sQuery(id+"F2.wireOp",EDGE,"E11.sketch_text.stroke-39"),sQuery(id+"F2.wireOp",EDGE,"E11.sketch_text.stroke-40"),sQuery(id+"F2.wireOp",EDGE,"E11.sketch_text.stroke-41"),sQuery(id+"F2.wireOp",EDGE,"E11.sketch_text.stroke-42"),sQuery(id+"F2.wireOp",EDGE,"E11.sketch_text.stroke-43"),sQuery(id+"F2.wireOp",EDGE,"E11.sketch_text.stroke-44"),sQuery(id+"F2.wireOp",EDGE,"E11.sketch_text.stroke-45"),sQuery(id+"F2.wireOp",EDGE,"E11.sketch_text.stroke-46"),sQuery(id+"F2.wireOp",EDGE,"E11.sketch_text.stroke-47"),sQuery(id+"F2.wireOp",EDGE,"E11.sketch_text.stroke-48"),sQuery(id+"F2.wireOp",EDGE,"E11.sketch_text.stroke-49")])]});
            var Q120;
            Q120=makeQuery(id+"F4.opExtrude","SWEPT_BODY",BODY,{"disambiguationData":[OSD([sQuery(id+"F2.wireOp",EDGE,"E11.sketch_text.stroke-50"),sQuery(id+"F2.wireOp",EDGE,"E11.sketch_text.stroke-51"),sQuery(id+"F2.wireOp",EDGE,"E11.sketch_text.stroke-52"),sQuery(id+"F2.wireOp",EDGE,"E11.sketch_text.stroke-53"),sQuery(id+"F2.wireOp",EDGE,"E11.sketch_text.stroke-54"),sQuery(id+"F2.wireOp",EDGE,"E11.sketch_text.stroke-55"),sQuery(id+"F2.wireOp",EDGE,"E11.sketch_text.stroke-56"),sQuery(id+"F2.wireOp",EDGE,"E11.sketch_text.stroke-57"),sQuery(id+"F2.wireOp",EDGE,"E11.sketch_text.stroke-58"),sQuery(id+"F2.wireOp",EDGE,"E11.sketch_text.stroke-59"),sQuery(id+"F2.wireOp",EDGE,"E11.sketch_text.stroke-60"),sQuery(id+"F2.wireOp",EDGE,"E11.sketch_text.stroke-61"),sQuery(id+"F2.wireOp",EDGE,"E11.sketch_text.stroke-62")])]});
            var Q121;
            Q121=makeQuery(id+"F4.opExtrude","SWEPT_BODY",BODY,{"disambiguationData":[OSD([sQuery(id+"F2.wireOp",EDGE,"E11.sketch_text.stroke-63"),sQuery(id+"F2.wireOp",EDGE,"E11.sketch_text.stroke-64"),sQuery(id+"F2.wireOp",EDGE,"E11.sketch_text.stroke-65"),sQuery(id+"F2.wireOp",EDGE,"E11.sketch_text.stroke-66"),sQuery(id+"F2.wireOp",EDGE,"E11.sketch_text.stroke-67"),sQuery(id+"F2.wireOp",EDGE,"E11.sketch_text.stroke-68"),sQuery(id+"F2.wireOp",EDGE,"E11.sketch_text.stroke-69"),sQuery(id+"F2.wireOp",EDGE,"E11.sketch_text.stroke-70"),sQuery(id+"F2.wireOp",EDGE,"E11.sketch_text.stroke-71"),sQuery(id+"F2.wireOp",EDGE,"E11.sketch_text.stroke-72"),sQuery(id+"F2.wireOp",EDGE,"E11.sketch_text.stroke-73"),sQuery(id+"F2.wireOp",EDGE,"E11.sketch_text.stroke-74"),sQuery(id+"F2.wireOp",EDGE,"E11.sketch_text.stroke-75"),sQuery(id+"F2.wireOp",EDGE,"E11.sketch_text.stroke-76"),sQuery(id+"F2.wireOp",EDGE,"E11.sketch_text.stroke-77"),sQuery(id+"F2.wireOp",EDGE,"E11.sketch_text.stroke-78"),sQuery(id+"F2.wireOp",EDGE,"E11.sketch_text.stroke-79"),sQuery(id+"F2.wireOp",EDGE,"E11.sketch_text.stroke-80"),sQuery(id+"F2.wireOp",EDGE,"E11.sketch_text.stroke-81"),sQuery(id+"F2.wireOp",EDGE,"E11.sketch_text.stroke-82"),sQuery(id+"F2.wireOp",EDGE,"E11.sketch_text.stroke-83"),sQuery(id+"F2.wireOp",EDGE,"E11.sketch_text.stroke-84"),sQuery(id+"F2.wireOp",EDGE,"E11.sketch_text.stroke-85"),sQuery(id+"F2.wireOp",EDGE,"E11.sketch_text.stroke-86"),sQuery(id+"F2.wireOp",EDGE,"E11.sketch_text.stroke-87"),sQuery(id+"F2.wireOp",EDGE,"E11.sketch_text.stroke-88"),sQuery(id+"F2.wireOp",EDGE,"E11.sketch_text.stroke-89")])]});
            var Q122;
            Q122=makeQuery(id+"F4.opExtrude","SWEPT_BODY",BODY,{"disambiguationData":[OSD([sQuery(id+"F2.wireOp",EDGE,"E11.sketch_text.stroke-90"),sQuery(id+"F2.wireOp",EDGE,"E11.sketch_text.stroke-91"),sQuery(id+"F2.wireOp",EDGE,"E11.sketch_text.stroke-92"),sQuery(id+"F2.wireOp",EDGE,"E11.sketch_text.stroke-93"),sQuery(id+"F2.wireOp",EDGE,"E11.sketch_text.stroke-94"),sQuery(id+"F2.wireOp",EDGE,"E11.sketch_text.stroke-95"),sQuery(id+"F2.wireOp",EDGE,"E11.sketch_text.stroke-96"),sQuery(id+"F2.wireOp",EDGE,"E11.sketch_text.stroke-97"),sQuery(id+"F2.wireOp",EDGE,"E11.sketch_text.stroke-98"),sQuery(id+"F2.wireOp",EDGE,"E11.sketch_text.stroke-99"),sQuery(id+"F2.wireOp",EDGE,"E11.sketch_text.stroke-100"),sQuery(id+"F2.wireOp",EDGE,"E11.sketch_text.stroke-101"),sQuery(id+"F2.wireOp",EDGE,"E11.sketch_text.stroke-102")])]});
            var Q123;
            Q123=makeQuery(id+"F4.opExtrude","SWEPT_BODY",BODY,{"disambiguationData":[OSD([sQuery(id+"F2.wireOp",EDGE,"E11.sketch_text.stroke-103"),sQuery(id+"F2.wireOp",EDGE,"E11.sketch_text.stroke-104"),sQuery(id+"F2.wireOp",EDGE,"E11.sketch_text.stroke-105"),sQuery(id+"F2.wireOp",EDGE,"E11.sketch_text.stroke-106")])]});
            var Q124;
            Q124=makeQuery(id+"F4.opExtrude","SWEPT_BODY",BODY,{"disambiguationData":[OSD([sQuery(id+"F2.wireOp",EDGE,"E11.sketch_text.stroke-107"),sQuery(id+"F2.wireOp",EDGE,"E11.sketch_text.stroke-108"),sQuery(id+"F2.wireOp",EDGE,"E11.sketch_text.stroke-109"),sQuery(id+"F2.wireOp",EDGE,"E11.sketch_text.stroke-110"),sQuery(id+"F2.wireOp",EDGE,"E11.sketch_text.stroke-111"),sQuery(id+"F2.wireOp",EDGE,"E11.sketch_text.stroke-112"),sQuery(id+"F2.wireOp",EDGE,"E11.sketch_text.stroke-113"),sQuery(id+"F2.wireOp",EDGE,"E11.sketch_text.stroke-114")])]});
            var Q125;
            Q125=makeQuery(id+"F4.opExtrude","SWEPT_BODY",BODY,{"disambiguationData":[OSD([sQuery(id+"F2.wireOp",EDGE,"E11.sketch_text.stroke-115"),sQuery(id+"F2.wireOp",EDGE,"E11.sketch_text.stroke-116"),sQuery(id+"F2.wireOp",EDGE,"E11.sketch_text.stroke-117"),sQuery(id+"F2.wireOp",EDGE,"E11.sketch_text.stroke-118"),sQuery(id+"F2.wireOp",EDGE,"E11.sketch_text.stroke-119"),sQuery(id+"F2.wireOp",EDGE,"E11.sketch_text.stroke-120"),sQuery(id+"F2.wireOp",EDGE,"E11.sketch_text.stroke-121"),sQuery(id+"F2.wireOp",EDGE,"E11.sketch_text.stroke-122"),sQuery(id+"F2.wireOp",EDGE,"E11.sketch_text.stroke-123"),sQuery(id+"F2.wireOp",EDGE,"E11.sketch_text.stroke-124"),sQuery(id+"F2.wireOp",EDGE,"E11.sketch_text.stroke-125"),sQuery(id+"F2.wireOp",EDGE,"E11.sketch_text.stroke-126"),sQuery(id+"F2.wireOp",EDGE,"E11.sketch_text.stroke-127"),sQuery(id+"F2.wireOp",EDGE,"E11.sketch_text.stroke-128"),sQuery(id+"F2.wireOp",EDGE,"E11.sketch_text.stroke-129"),sQuery(id+"F2.wireOp",EDGE,"E11.sketch_text.stroke-130"),sQuery(id+"F2.wireOp",EDGE,"E11.sketch_text.stroke-131"),sQuery(id+"F2.wireOp",EDGE,"E11.sketch_text.stroke-132"),sQuery(id+"F2.wireOp",EDGE,"E11.sketch_text.stroke-133"),sQuery(id+"F2.wireOp",EDGE,"E11.sketch_text.stroke-134"),sQuery(id+"F2.wireOp",EDGE,"E11.sketch_text.stroke-135"),sQuery(id+"F2.wireOp",EDGE,"E11.sketch_text.stroke-136"),sQuery(id+"F2.wireOp",EDGE,"E11.sketch_text.stroke-137"),sQuery(id+"F2.wireOp",EDGE,"E11.sketch_text.stroke-138"),sQuery(id+"F2.wireOp",EDGE,"E11.sketch_text.stroke-139"),sQuery(id+"F2.wireOp",EDGE,"E11.sketch_text.stroke-140"),sQuery(id+"F2.wireOp",EDGE,"E11.sketch_text.stroke-141"),sQuery(id+"F2.wireOp",EDGE,"E11.sketch_text.stroke-142"),sQuery(id+"F2.wireOp",EDGE,"E11.sketch_text.stroke-143"),sQuery(id+"F2.wireOp",EDGE,"E11.sketch_text.stroke-144"),sQuery(id+"F2.wireOp",EDGE,"E11.sketch_text.stroke-145"),sQuery(id+"F2.wireOp",EDGE,"E11.sketch_text.stroke-146"),sQuery(id+"F2.wireOp",EDGE,"E11.sketch_text.stroke-147"),sQuery(id+"F2.wireOp",EDGE,"E11.sketch_text.stroke-148"),sQuery(id+"F2.wireOp",EDGE,"E11.sketch_text.stroke-149"),sQuery(id+"F2.wireOp",EDGE,"E11.sketch_text.stroke-150"),sQuery(id+"F2.wireOp",EDGE,"E11.sketch_text.stroke-151"),sQuery(id+"F2.wireOp",EDGE,"E11.sketch_text.stroke-152"),sQuery(id+"F2.wireOp",EDGE,"E11.sketch_text.stroke-153"),sQuery(id+"F2.wireOp",EDGE,"E11.sketch_text.stroke-154"),sQuery(id+"F2.wireOp",EDGE,"E11.sketch_text.stroke-155"),sQuery(id+"F2.wireOp",EDGE,"E11.sketch_text.stroke-156"),sQuery(id+"F2.wireOp",EDGE,"E11.sketch_text.stroke-157"),sQuery(id+"F2.wireOp",EDGE,"E11.sketch_text.stroke-158")])]});
            var Q126;
            Q126=makeQuery(id+"F4.opExtrude","SWEPT_BODY",BODY,{"disambiguationData":[OSD([sQuery(id+"F2.wireOp",EDGE,"E11.sketch_text.stroke-159"),sQuery(id+"F2.wireOp",EDGE,"E11.sketch_text.stroke-160"),sQuery(id+"F2.wireOp",EDGE,"E11.sketch_text.stroke-161"),sQuery(id+"F2.wireOp",EDGE,"E11.sketch_text.stroke-162"),sQuery(id+"F2.wireOp",EDGE,"E11.sketch_text.stroke-163"),sQuery(id+"F2.wireOp",EDGE,"E11.sketch_text.stroke-164"),sQuery(id+"F2.wireOp",EDGE,"E11.sketch_text.stroke-165"),sQuery(id+"F2.wireOp",EDGE,"E11.sketch_text.stroke-166"),sQuery(id+"F2.wireOp",EDGE,"E11.sketch_text.stroke-167"),sQuery(id+"F2.wireOp",EDGE,"E11.sketch_text.stroke-168"),sQuery(id+"F2.wireOp",EDGE,"E11.sketch_text.stroke-169"),sQuery(id+"F2.wireOp",EDGE,"E11.sketch_text.stroke-170"),sQuery(id+"F2.wireOp",EDGE,"E11.sketch_text.stroke-171"),sQuery(id+"F2.wireOp",EDGE,"E11.sketch_text.stroke-172"),sQuery(id+"F2.wireOp",EDGE,"E11.sketch_text.stroke-173"),sQuery(id+"F2.wireOp",EDGE,"E11.sketch_text.stroke-174"),sQuery(id+"F2.wireOp",EDGE,"E11.sketch_text.stroke-175"),sQuery(id+"F2.wireOp",EDGE,"E11.sketch_text.stroke-176"),sQuery(id+"F2.wireOp",EDGE,"E11.sketch_text.stroke-177"),sQuery(id+"F2.wireOp",EDGE,"E11.sketch_text.stroke-178"),sQuery(id+"F2.wireOp",EDGE,"E11.sketch_text.stroke-179"),sQuery(id+"F2.wireOp",EDGE,"E11.sketch_text.stroke-180"),sQuery(id+"F2.wireOp",EDGE,"E11.sketch_text.stroke-181"),sQuery(id+"F2.wireOp",EDGE,"E11.sketch_text.stroke-182"),sQuery(id+"F2.wireOp",EDGE,"E11.sketch_text.stroke-183"),sQuery(id+"F2.wireOp",EDGE,"E11.sketch_text.stroke-184"),sQuery(id+"F2.wireOp",EDGE,"E11.sketch_text.stroke-185"),sQuery(id+"F2.wireOp",EDGE,"E11.sketch_text.stroke-186"),sQuery(id+"F2.wireOp",EDGE,"E11.sketch_text.stroke-187"),sQuery(id+"F2.wireOp",EDGE,"E11.sketch_text.stroke-188"),sQuery(id+"F2.wireOp",EDGE,"E11.sketch_text.stroke-189"),sQuery(id+"F2.wireOp",EDGE,"E11.sketch_text.stroke-190"),sQuery(id+"F2.wireOp",EDGE,"E11.sketch_text.stroke-191"),sQuery(id+"F2.wireOp",EDGE,"E11.sketch_text.stroke-192"),sQuery(id+"F2.wireOp",EDGE,"E11.sketch_text.stroke-193"),sQuery(id+"F2.wireOp",EDGE,"E11.sketch_text.stroke-194"),sQuery(id+"F2.wireOp",EDGE,"E11.sketch_text.stroke-195"),sQuery(id+"F2.wireOp",EDGE,"E11.sketch_text.stroke-196"),sQuery(id+"F2.wireOp",EDGE,"E11.sketch_text.stroke-197"),sQuery(id+"F2.wireOp",EDGE,"E11.sketch_text.stroke-198"),sQuery(id+"F2.wireOp",EDGE,"E11.sketch_text.stroke-199"),sQuery(id+"F2.wireOp",EDGE,"E11.sketch_text.stroke-200"),sQuery(id+"F2.wireOp",EDGE,"E11.sketch_text.stroke-201"),sQuery(id+"F2.wireOp",EDGE,"E11.sketch_text.stroke-202")])]});
            var Q127;
            Q127=makeQuery(id+"F4.opExtrude","SWEPT_BODY",BODY,{"disambiguationData":[OSD([sQuery(id+"F2.wireOp",EDGE,"E11.sketch_text.stroke-203"),sQuery(id+"F2.wireOp",EDGE,"E11.sketch_text.stroke-204"),sQuery(id+"F2.wireOp",EDGE,"E11.sketch_text.stroke-205"),sQuery(id+"F2.wireOp",EDGE,"E11.sketch_text.stroke-206")])]});
            var Q128;
            Q128=makeQuery(id+"F4.opExtrude","SWEPT_BODY",BODY,{"disambiguationData":[OSD([sQuery(id+"F2.wireOp",EDGE,"E11.sketch_text.stroke-207"),sQuery(id+"F2.wireOp",EDGE,"E11.sketch_text.stroke-208"),sQuery(id+"F2.wireOp",EDGE,"E11.sketch_text.stroke-209"),sQuery(id+"F2.wireOp",EDGE,"E11.sketch_text.stroke-210"),sQuery(id+"F2.wireOp",EDGE,"E11.sketch_text.stroke-211"),sQuery(id+"F2.wireOp",EDGE,"E11.sketch_text.stroke-212"),sQuery(id+"F2.wireOp",EDGE,"E11.sketch_text.stroke-213"),sQuery(id+"F2.wireOp",EDGE,"E11.sketch_text.stroke-214")])]});
            var Q129;
            Q129=makeQuery(id+"F4.opExtrude","SWEPT_BODY",BODY,{"disambiguationData":[OSD([sQuery(id+"F2.wireOp",EDGE,"E11.sketch_text.stroke-215"),sQuery(id+"F2.wireOp",EDGE,"E11.sketch_text.stroke-216"),sQuery(id+"F2.wireOp",EDGE,"E11.sketch_text.stroke-217"),sQuery(id+"F2.wireOp",EDGE,"E11.sketch_text.stroke-218"),sQuery(id+"F2.wireOp",EDGE,"E11.sketch_text.stroke-219"),sQuery(id+"F2.wireOp",EDGE,"E11.sketch_text.stroke-220"),sQuery(id+"F2.wireOp",EDGE,"E11.sketch_text.stroke-221"),sQuery(id+"F2.wireOp",EDGE,"E11.sketch_text.stroke-222"),sQuery(id+"F2.wireOp",EDGE,"E11.sketch_text.stroke-223"),sQuery(id+"F2.wireOp",EDGE,"E11.sketch_text.stroke-224"),sQuery(id+"F2.wireOp",EDGE,"E11.sketch_text.stroke-225"),sQuery(id+"F2.wireOp",EDGE,"E11.sketch_text.stroke-226"),sQuery(id+"F2.wireOp",EDGE,"E11.sketch_text.stroke-227"),sQuery(id+"F2.wireOp",EDGE,"E11.sketch_text.stroke-228"),sQuery(id+"F2.wireOp",EDGE,"E11.sketch_text.stroke-229"),sQuery(id+"F2.wireOp",EDGE,"E11.sketch_text.stroke-230"),sQuery(id+"F2.wireOp",EDGE,"E11.sketch_text.stroke-231")])]});
            var Q130;
            Q130=makeQuery(id+"F4.opExtrude","SWEPT_BODY",BODY,{"disambiguationData":[OSD([sQuery(id+"F2.wireOp",EDGE,"E11.sketch_text.stroke-232"),sQuery(id+"F2.wireOp",EDGE,"E11.sketch_text.stroke-233"),sQuery(id+"F2.wireOp",EDGE,"E11.sketch_text.stroke-234"),sQuery(id+"F2.wireOp",EDGE,"E11.sketch_text.stroke-235"),sQuery(id+"F2.wireOp",EDGE,"E11.sketch_text.stroke-236"),sQuery(id+"F2.wireOp",EDGE,"E11.sketch_text.stroke-237"),sQuery(id+"F2.wireOp",EDGE,"E11.sketch_text.stroke-238"),sQuery(id+"F2.wireOp",EDGE,"E11.sketch_text.stroke-239"),sQuery(id+"F2.wireOp",EDGE,"E11.sketch_text.stroke-240"),sQuery(id+"F2.wireOp",EDGE,"E11.sketch_text.stroke-241"),sQuery(id+"F2.wireOp",EDGE,"E11.sketch_text.stroke-242"),sQuery(id+"F2.wireOp",EDGE,"E11.sketch_text.stroke-243"),sQuery(id+"F2.wireOp",EDGE,"E11.sketch_text.stroke-244"),sQuery(id+"F2.wireOp",EDGE,"E11.sketch_text.stroke-245"),sQuery(id+"F2.wireOp",EDGE,"E11.sketch_text.stroke-246"),sQuery(id+"F2.wireOp",EDGE,"E11.sketch_text.stroke-247"),sQuery(id+"F2.wireOp",EDGE,"E11.sketch_text.stroke-248"),sQuery(id+"F2.wireOp",EDGE,"E11.sketch_text.stroke-249"),sQuery(id+"F2.wireOp",EDGE,"E11.sketch_text.stroke-250"),sQuery(id+"F2.wireOp",EDGE,"E11.sketch_text.stroke-251"),sQuery(id+"F2.wireOp",EDGE,"E11.sketch_text.stroke-252"),sQuery(id+"F2.wireOp",EDGE,"E11.sketch_text.stroke-253"),sQuery(id+"F2.wireOp",EDGE,"E11.sketch_text.stroke-254"),sQuery(id+"F2.wireOp",EDGE,"E11.sketch_text.stroke-255"),sQuery(id+"F2.wireOp",EDGE,"E11.sketch_text.stroke-256"),sQuery(id+"F2.wireOp",EDGE,"E11.sketch_text.stroke-257"),sQuery(id+"F2.wireOp",EDGE,"E11.sketch_text.stroke-258"),sQuery(id+"F2.wireOp",EDGE,"E11.sketch_text.stroke-259"),sQuery(id+"F2.wireOp",EDGE,"E11.sketch_text.stroke-260"),sQuery(id+"F2.wireOp",EDGE,"E11.sketch_text.stroke-261"),sQuery(id+"F2.wireOp",EDGE,"E11.sketch_text.stroke-262"),sQuery(id+"F2.wireOp",EDGE,"E11.sketch_text.stroke-263"),sQuery(id+"F2.wireOp",EDGE,"E11.sketch_text.stroke-264"),sQuery(id+"F2.wireOp",EDGE,"E11.sketch_text.stroke-265"),sQuery(id+"F2.wireOp",EDGE,"E11.sketch_text.stroke-266"),sQuery(id+"F2.wireOp",EDGE,"E11.sketch_text.stroke-267"),sQuery(id+"F2.wireOp",EDGE,"E11.sketch_text.stroke-268"),sQuery(id+"F2.wireOp",EDGE,"E11.sketch_text.stroke-269"),sQuery(id+"F2.wireOp",EDGE,"E11.sketch_text.stroke-270"),sQuery(id+"F2.wireOp",EDGE,"E11.sketch_text.stroke-271"),sQuery(id+"F2.wireOp",EDGE,"E11.sketch_text.stroke-272"),sQuery(id+"F2.wireOp",EDGE,"E11.sketch_text.stroke-273"),sQuery(id+"F2.wireOp",EDGE,"E11.sketch_text.stroke-274"),sQuery(id+"F2.wireOp",EDGE,"E11.sketch_text.stroke-275")])]});
            var Q131;
            Q131=makeQuery(id+"F4.opExtrude","SWEPT_BODY",BODY,{"disambiguationData":[OSD([sQuery(id+"F2.wireOp",EDGE,"E11.sketch_text.stroke-276"),sQuery(id+"F2.wireOp",EDGE,"E11.sketch_text.stroke-277"),sQuery(id+"F2.wireOp",EDGE,"E11.sketch_text.stroke-278"),sQuery(id+"F2.wireOp",EDGE,"E11.sketch_text.stroke-279"),sQuery(id+"F2.wireOp",EDGE,"E11.sketch_text.stroke-280"),sQuery(id+"F2.wireOp",EDGE,"E11.sketch_text.stroke-281"),sQuery(id+"F2.wireOp",EDGE,"E11.sketch_text.stroke-282"),sQuery(id+"F2.wireOp",EDGE,"E11.sketch_text.stroke-283"),sQuery(id+"F2.wireOp",EDGE,"E11.sketch_text.stroke-284"),sQuery(id+"F2.wireOp",EDGE,"E11.sketch_text.stroke-285"),sQuery(id+"F2.wireOp",EDGE,"E11.sketch_text.stroke-286"),sQuery(id+"F2.wireOp",EDGE,"E11.sketch_text.stroke-287"),sQuery(id+"F2.wireOp",EDGE,"E11.sketch_text.stroke-288"),sQuery(id+"F2.wireOp",EDGE,"E11.sketch_text.stroke-289"),sQuery(id+"F2.wireOp",EDGE,"E11.sketch_text.stroke-290"),sQuery(id+"F2.wireOp",EDGE,"E11.sketch_text.stroke-291"),sQuery(id+"F2.wireOp",EDGE,"E11.sketch_text.stroke-292"),sQuery(id+"F2.wireOp",EDGE,"E11.sketch_text.stroke-293"),sQuery(id+"F2.wireOp",EDGE,"E11.sketch_text.stroke-294"),sQuery(id+"F2.wireOp",EDGE,"E11.sketch_text.stroke-295"),sQuery(id+"F2.wireOp",EDGE,"E11.sketch_text.stroke-296"),sQuery(id+"F2.wireOp",EDGE,"E11.sketch_text.stroke-297"),sQuery(id+"F2.wireOp",EDGE,"E11.sketch_text.stroke-298"),sQuery(id+"F2.wireOp",EDGE,"E11.sketch_text.stroke-299")])]});
            var Q132;
            Q132=makeQuery(id+"F4.opExtrude","SWEPT_BODY",BODY,{"disambiguationData":[OSD([sQuery(id+"F2.wireOp",EDGE,"E11.sketch_text.stroke-300"),sQuery(id+"F2.wireOp",EDGE,"E11.sketch_text.stroke-301"),sQuery(id+"F2.wireOp",EDGE,"E11.sketch_text.stroke-302"),sQuery(id+"F2.wireOp",EDGE,"E11.sketch_text.stroke-303"),sQuery(id+"F2.wireOp",EDGE,"E11.sketch_text.stroke-304"),sQuery(id+"F2.wireOp",EDGE,"E11.sketch_text.stroke-305"),sQuery(id+"F2.wireOp",EDGE,"E11.sketch_text.stroke-306"),sQuery(id+"F2.wireOp",EDGE,"E11.sketch_text.stroke-307"),sQuery(id+"F2.wireOp",EDGE,"E11.sketch_text.stroke-308"),sQuery(id+"F2.wireOp",EDGE,"E11.sketch_text.stroke-309"),sQuery(id+"F2.wireOp",EDGE,"E11.sketch_text.stroke-310"),sQuery(id+"F2.wireOp",EDGE,"E11.sketch_text.stroke-311"),sQuery(id+"F2.wireOp",EDGE,"E11.sketch_text.stroke-312"),sQuery(id+"F2.wireOp",EDGE,"E11.sketch_text.stroke-313"),sQuery(id+"F2.wireOp",EDGE,"E11.sketch_text.stroke-314"),sQuery(id+"F2.wireOp",EDGE,"E11.sketch_text.stroke-315"),sQuery(id+"F2.wireOp",EDGE,"E11.sketch_text.stroke-316"),sQuery(id+"F2.wireOp",EDGE,"E11.sketch_text.stroke-317"),sQuery(id+"F2.wireOp",EDGE,"E11.sketch_text.stroke-318")])]});
            var Q133;
            Q133=makeQuery(id+"F4.opExtrude","SWEPT_BODY",BODY,{"disambiguationData":[OSD([sQuery(id+"F2.wireOp",EDGE,"E11.sketch_text.stroke-319"),sQuery(id+"F2.wireOp",EDGE,"E11.sketch_text.stroke-320"),sQuery(id+"F2.wireOp",EDGE,"E11.sketch_text.stroke-321"),sQuery(id+"F2.wireOp",EDGE,"E11.sketch_text.stroke-322"),sQuery(id+"F2.wireOp",EDGE,"E11.sketch_text.stroke-323"),sQuery(id+"F2.wireOp",EDGE,"E11.sketch_text.stroke-324"),sQuery(id+"F2.wireOp",EDGE,"E11.sketch_text.stroke-325"),sQuery(id+"F2.wireOp",EDGE,"E11.sketch_text.stroke-326"),sQuery(id+"F2.wireOp",EDGE,"E11.sketch_text.stroke-327"),sQuery(id+"F2.wireOp",EDGE,"E11.sketch_text.stroke-328"),sQuery(id+"F2.wireOp",EDGE,"E11.sketch_text.stroke-329"),sQuery(id+"F2.wireOp",EDGE,"E11.sketch_text.stroke-330"),sQuery(id+"F2.wireOp",EDGE,"E11.sketch_text.stroke-331"),sQuery(id+"F2.wireOp",EDGE,"E11.sketch_text.stroke-332"),sQuery(id+"F2.wireOp",EDGE,"E11.sketch_text.stroke-333"),sQuery(id+"F2.wireOp",EDGE,"E11.sketch_text.stroke-334"),sQuery(id+"F2.wireOp",EDGE,"E11.sketch_text.stroke-335"),sQuery(id+"F2.wireOp",EDGE,"E11.sketch_text.stroke-336"),sQuery(id+"F2.wireOp",EDGE,"E11.sketch_text.stroke-337"),sQuery(id+"F2.wireOp",EDGE,"E11.sketch_text.stroke-338"),sQuery(id+"F2.wireOp",EDGE,"E11.sketch_text.stroke-339"),sQuery(id+"F2.wireOp",EDGE,"E11.sketch_text.stroke-340"),sQuery(id+"F2.wireOp",EDGE,"E11.sketch_text.stroke-341"),sQuery(id+"F2.wireOp",EDGE,"E11.sketch_text.stroke-342"),sQuery(id+"F2.wireOp",EDGE,"E11.sketch_text.stroke-343")])]});
            var Q134;
            Q134=makeQuery(id+"F4.opExtrude","SWEPT_BODY",BODY,{"disambiguationData":[OSD([sQuery(id+"F2.wireOp",EDGE,"E11.sketch_text.stroke-344"),sQuery(id+"F2.wireOp",EDGE,"E11.sketch_text.stroke-345"),sQuery(id+"F2.wireOp",EDGE,"E11.sketch_text.stroke-346"),sQuery(id+"F2.wireOp",EDGE,"E11.sketch_text.stroke-347")])]});
            var Q135;
            Q135=makeQuery(id+"F4.opExtrude","SWEPT_BODY",BODY,{"disambiguationData":[OSD([sQuery(id+"F2.wireOp",EDGE,"E11.sketch_text.stroke-348"),sQuery(id+"F2.wireOp",EDGE,"E11.sketch_text.stroke-349"),sQuery(id+"F2.wireOp",EDGE,"E11.sketch_text.stroke-350"),sQuery(id+"F2.wireOp",EDGE,"E11.sketch_text.stroke-351"),sQuery(id+"F2.wireOp",EDGE,"E11.sketch_text.stroke-352"),sQuery(id+"F2.wireOp",EDGE,"E11.sketch_text.stroke-353"),sQuery(id+"F2.wireOp",EDGE,"E11.sketch_text.stroke-354"),sQuery(id+"F2.wireOp",EDGE,"E11.sketch_text.stroke-355")])]});
            var Q136;
            Q136=makeQuery(id+"F4.opExtrude","SWEPT_BODY",BODY,{"disambiguationData":[OSD([sQuery(id+"F2.wireOp",EDGE,"E11.sketch_text.stroke-356"),sQuery(id+"F2.wireOp",EDGE,"E11.sketch_text.stroke-357"),sQuery(id+"F2.wireOp",EDGE,"E11.sketch_text.stroke-358"),sQuery(id+"F2.wireOp",EDGE,"E11.sketch_text.stroke-359"),sQuery(id+"F2.wireOp",EDGE,"E11.sketch_text.stroke-360"),sQuery(id+"F2.wireOp",EDGE,"E11.sketch_text.stroke-361"),sQuery(id+"F2.wireOp",EDGE,"E11.sketch_text.stroke-362"),sQuery(id+"F2.wireOp",EDGE,"E11.sketch_text.stroke-363"),sQuery(id+"F2.wireOp",EDGE,"E11.sketch_text.stroke-364"),sQuery(id+"F2.wireOp",EDGE,"E11.sketch_text.stroke-365"),sQuery(id+"F2.wireOp",EDGE,"E11.sketch_text.stroke-366"),sQuery(id+"F2.wireOp",EDGE,"E11.sketch_text.stroke-367"),sQuery(id+"F2.wireOp",EDGE,"E11.sketch_text.stroke-368"),sQuery(id+"F2.wireOp",EDGE,"E11.sketch_text.stroke-369"),sQuery(id+"F2.wireOp",EDGE,"E11.sketch_text.stroke-370"),sQuery(id+"F2.wireOp",EDGE,"E11.sketch_text.stroke-371"),sQuery(id+"F2.wireOp",EDGE,"E11.sketch_text.stroke-372"),sQuery(id+"F2.wireOp",EDGE,"E11.sketch_text.stroke-373"),sQuery(id+"F2.wireOp",EDGE,"E11.sketch_text.stroke-374"),sQuery(id+"F2.wireOp",EDGE,"E11.sketch_text.stroke-375"),sQuery(id+"F2.wireOp",EDGE,"E11.sketch_text.stroke-376"),sQuery(id+"F2.wireOp",EDGE,"E11.sketch_text.stroke-377"),sQuery(id+"F2.wireOp",EDGE,"E11.sketch_text.stroke-378"),sQuery(id+"F2.wireOp",EDGE,"E11.sketch_text.stroke-379"),sQuery(id+"F2.wireOp",EDGE,"E11.sketch_text.stroke-380"),sQuery(id+"F2.wireOp",EDGE,"E11.sketch_text.stroke-381"),sQuery(id+"F2.wireOp",EDGE,"E11.sketch_text.stroke-382"),sQuery(id+"F2.wireOp",EDGE,"E11.sketch_text.stroke-383"),sQuery(id+"F2.wireOp",EDGE,"E11.sketch_text.stroke-384"),sQuery(id+"F2.wireOp",EDGE,"E11.sketch_text.stroke-385"),sQuery(id+"F2.wireOp",EDGE,"E11.sketch_text.stroke-386"),sQuery(id+"F2.wireOp",EDGE,"E11.sketch_text.stroke-387"),sQuery(id+"F2.wireOp",EDGE,"E11.sketch_text.stroke-388"),sQuery(id+"F2.wireOp",EDGE,"E11.sketch_text.stroke-389"),sQuery(id+"F2.wireOp",EDGE,"E11.sketch_text.stroke-390"),sQuery(id+"F2.wireOp",EDGE,"E11.sketch_text.stroke-391"),sQuery(id+"F2.wireOp",EDGE,"E11.sketch_text.stroke-392"),sQuery(id+"F2.wireOp",EDGE,"E11.sketch_text.stroke-393"),sQuery(id+"F2.wireOp",EDGE,"E11.sketch_text.stroke-394"),sQuery(id+"F2.wireOp",EDGE,"E11.sketch_text.stroke-395"),sQuery(id+"F2.wireOp",EDGE,"E11.sketch_text.stroke-396"),sQuery(id+"F2.wireOp",EDGE,"E11.sketch_text.stroke-397"),sQuery(id+"F2.wireOp",EDGE,"E11.sketch_text.stroke-398"),sQuery(id+"F2.wireOp",EDGE,"E11.sketch_text.stroke-399")])]});
            var Q137;
            Q137=makeQuery(id+"F4.opExtrude","SWEPT_BODY",BODY,{"disambiguationData":[OSD([sQuery(id+"F2.wireOp",EDGE,"E11.sketch_text.stroke-400"),sQuery(id+"F2.wireOp",EDGE,"E11.sketch_text.stroke-401"),sQuery(id+"F2.wireOp",EDGE,"E11.sketch_text.stroke-402"),sQuery(id+"F2.wireOp",EDGE,"E11.sketch_text.stroke-403"),sQuery(id+"F2.wireOp",EDGE,"E11.sketch_text.stroke-404"),sQuery(id+"F2.wireOp",EDGE,"E11.sketch_text.stroke-405"),sQuery(id+"F2.wireOp",EDGE,"E11.sketch_text.stroke-406"),sQuery(id+"F2.wireOp",EDGE,"E11.sketch_text.stroke-407"),sQuery(id+"F2.wireOp",EDGE,"E11.sketch_text.stroke-408"),sQuery(id+"F2.wireOp",EDGE,"E11.sketch_text.stroke-409"),sQuery(id+"F2.wireOp",EDGE,"E11.sketch_text.stroke-410"),sQuery(id+"F2.wireOp",EDGE,"E11.sketch_text.stroke-411"),sQuery(id+"F2.wireOp",EDGE,"E11.sketch_text.stroke-412"),sQuery(id+"F2.wireOp",EDGE,"E11.sketch_text.stroke-413"),sQuery(id+"F2.wireOp",EDGE,"E11.sketch_text.stroke-414"),sQuery(id+"F2.wireOp",EDGE,"E11.sketch_text.stroke-415"),sQuery(id+"F2.wireOp",EDGE,"E11.sketch_text.stroke-416")])]});
            var Q138;
            Q138=makeQuery(id+"F4.opExtrude","SWEPT_BODY",BODY,{"disambiguationData":[OSD([sQuery(id+"F2.wireOp",EDGE,"E11.sketch_text.stroke-417"),sQuery(id+"F2.wireOp",EDGE,"E11.sketch_text.stroke-418"),sQuery(id+"F2.wireOp",EDGE,"E11.sketch_text.stroke-419"),sQuery(id+"F2.wireOp",EDGE,"E11.sketch_text.stroke-420"),sQuery(id+"F2.wireOp",EDGE,"E11.sketch_text.stroke-421"),sQuery(id+"F2.wireOp",EDGE,"E11.sketch_text.stroke-422"),sQuery(id+"F2.wireOp",EDGE,"E11.sketch_text.stroke-423"),sQuery(id+"F2.wireOp",EDGE,"E11.sketch_text.stroke-424"),sQuery(id+"F2.wireOp",EDGE,"E11.sketch_text.stroke-425"),sQuery(id+"F2.wireOp",EDGE,"E11.sketch_text.stroke-426"),sQuery(id+"F2.wireOp",EDGE,"E11.sketch_text.stroke-427"),sQuery(id+"F2.wireOp",EDGE,"E11.sketch_text.stroke-428"),sQuery(id+"F2.wireOp",EDGE,"E11.sketch_text.stroke-429"),sQuery(id+"F2.wireOp",EDGE,"E11.sketch_text.stroke-430"),sQuery(id+"F2.wireOp",EDGE,"E11.sketch_text.stroke-431"),sQuery(id+"F2.wireOp",EDGE,"E11.sketch_text.stroke-432"),sQuery(id+"F2.wireOp",EDGE,"E11.sketch_text.stroke-433"),sQuery(id+"F2.wireOp",EDGE,"E11.sketch_text.stroke-434"),sQuery(id+"F2.wireOp",EDGE,"E11.sketch_text.stroke-435"),sQuery(id+"F2.wireOp",EDGE,"E11.sketch_text.stroke-436"),sQuery(id+"F2.wireOp",EDGE,"E11.sketch_text.stroke-437"),sQuery(id+"F2.wireOp",EDGE,"E11.sketch_text.stroke-438"),sQuery(id+"F2.wireOp",EDGE,"E11.sketch_text.stroke-439"),sQuery(id+"F2.wireOp",EDGE,"E11.sketch_text.stroke-440"),sQuery(id+"F2.wireOp",EDGE,"E11.sketch_text.stroke-441")])]});
            var Q139;
            Q139=makeQuery(id+"F4.opExtrude","SWEPT_BODY",BODY,{"disambiguationData":[OSD([sQuery(id+"F2.wireOp",EDGE,"E11.sketch_text.stroke-442"),sQuery(id+"F2.wireOp",EDGE,"E11.sketch_text.stroke-443"),sQuery(id+"F2.wireOp",EDGE,"E11.sketch_text.stroke-444"),sQuery(id+"F2.wireOp",EDGE,"E11.sketch_text.stroke-445"),sQuery(id+"F2.wireOp",EDGE,"E11.sketch_text.stroke-446"),sQuery(id+"F2.wireOp",EDGE,"E11.sketch_text.stroke-447"),sQuery(id+"F2.wireOp",EDGE,"E11.sketch_text.stroke-448"),sQuery(id+"F2.wireOp",EDGE,"E11.sketch_text.stroke-449"),sQuery(id+"F2.wireOp",EDGE,"E11.sketch_text.stroke-450"),sQuery(id+"F2.wireOp",EDGE,"E11.sketch_text.stroke-451"),sQuery(id+"F2.wireOp",EDGE,"E11.sketch_text.stroke-452"),sQuery(id+"F2.wireOp",EDGE,"E11.sketch_text.stroke-453"),sQuery(id+"F2.wireOp",EDGE,"E11.sketch_text.stroke-454"),sQuery(id+"F2.wireOp",EDGE,"E11.sketch_text.stroke-455"),sQuery(id+"F2.wireOp",EDGE,"E11.sketch_text.stroke-456"),sQuery(id+"F2.wireOp",EDGE,"E11.sketch_text.stroke-457"),sQuery(id+"F2.wireOp",EDGE,"E11.sketch_text.stroke-458"),sQuery(id+"F2.wireOp",EDGE,"E11.sketch_text.stroke-459"),sQuery(id+"F2.wireOp",EDGE,"E11.sketch_text.stroke-460"),sQuery(id+"F2.wireOp",EDGE,"E11.sketch_text.stroke-461"),sQuery(id+"F2.wireOp",EDGE,"E11.sketch_text.stroke-462"),sQuery(id+"F2.wireOp",EDGE,"E11.sketch_text.stroke-463"),sQuery(id+"F2.wireOp",EDGE,"E11.sketch_text.stroke-464")])]});
            var Q140;
            Q140=makeQuery(id+"F4.opExtrude","SWEPT_BODY",BODY,{"disambiguationData":[OSD([sQuery(id+"F2.wireOp",EDGE,"E11.sketch_text.stroke-465"),sQuery(id+"F2.wireOp",EDGE,"E11.sketch_text.stroke-466"),sQuery(id+"F2.wireOp",EDGE,"E11.sketch_text.stroke-467"),sQuery(id+"F2.wireOp",EDGE,"E11.sketch_text.stroke-468"),sQuery(id+"F2.wireOp",EDGE,"E11.sketch_text.stroke-469"),sQuery(id+"F2.wireOp",EDGE,"E11.sketch_text.stroke-470"),sQuery(id+"F2.wireOp",EDGE,"E11.sketch_text.stroke-471"),sQuery(id+"F2.wireOp",EDGE,"E11.sketch_text.stroke-472"),sQuery(id+"F2.wireOp",EDGE,"E11.sketch_text.stroke-473"),sQuery(id+"F2.wireOp",EDGE,"E11.sketch_text.stroke-474"),sQuery(id+"F2.wireOp",EDGE,"E11.sketch_text.stroke-475"),sQuery(id+"F2.wireOp",EDGE,"E11.sketch_text.stroke-476"),sQuery(id+"F2.wireOp",EDGE,"E11.sketch_text.stroke-477"),sQuery(id+"F2.wireOp",EDGE,"E11.sketch_text.stroke-478"),sQuery(id+"F2.wireOp",EDGE,"E11.sketch_text.stroke-479"),sQuery(id+"F2.wireOp",EDGE,"E11.sketch_text.stroke-480")])]});
            var Q141;
            Q141=makeQuery(id+"F4.opExtrude","SWEPT_BODY",BODY,{"disambiguationData":[OSD([sQuery(id+"F2.wireOp",EDGE,"E11.sketch_text.stroke-481"),sQuery(id+"F2.wireOp",EDGE,"E11.sketch_text.stroke-482"),sQuery(id+"F2.wireOp",EDGE,"E11.sketch_text.stroke-483"),sQuery(id+"F2.wireOp",EDGE,"E11.sketch_text.stroke-484"),sQuery(id+"F2.wireOp",EDGE,"E11.sketch_text.stroke-485"),sQuery(id+"F2.wireOp",EDGE,"E11.sketch_text.stroke-486"),sQuery(id+"F2.wireOp",EDGE,"E11.sketch_text.stroke-487"),sQuery(id+"F2.wireOp",EDGE,"E11.sketch_text.stroke-488"),sQuery(id+"F2.wireOp",EDGE,"E11.sketch_text.stroke-489"),sQuery(id+"F2.wireOp",EDGE,"E11.sketch_text.stroke-490"),sQuery(id+"F2.wireOp",EDGE,"E11.sketch_text.stroke-491"),sQuery(id+"F2.wireOp",EDGE,"E11.sketch_text.stroke-492"),sQuery(id+"F2.wireOp",EDGE,"E11.sketch_text.stroke-493"),sQuery(id+"F2.wireOp",EDGE,"E11.sketch_text.stroke-494"),sQuery(id+"F2.wireOp",EDGE,"E11.sketch_text.stroke-495"),sQuery(id+"F2.wireOp",EDGE,"E11.sketch_text.stroke-496"),sQuery(id+"F2.wireOp",EDGE,"E11.sketch_text.stroke-497"),sQuery(id+"F2.wireOp",EDGE,"E11.sketch_text.stroke-498"),sQuery(id+"F2.wireOp",EDGE,"E11.sketch_text.stroke-499"),sQuery(id+"F2.wireOp",EDGE,"E11.sketch_text.stroke-500")])]});
            var Q142;
            Q142=makeQuery(id+"F4.opExtrude","SWEPT_BODY",BODY,{"disambiguationData":[OSD([sQuery(id+"F2.wireOp",EDGE,"E11.sketch_text.stroke-501"),sQuery(id+"F2.wireOp",EDGE,"E11.sketch_text.stroke-502"),sQuery(id+"F2.wireOp",EDGE,"E11.sketch_text.stroke-503"),sQuery(id+"F2.wireOp",EDGE,"E11.sketch_text.stroke-504"),sQuery(id+"F2.wireOp",EDGE,"E11.sketch_text.stroke-505"),sQuery(id+"F2.wireOp",EDGE,"E11.sketch_text.stroke-506"),sQuery(id+"F2.wireOp",EDGE,"E11.sketch_text.stroke-507"),sQuery(id+"F2.wireOp",EDGE,"E11.sketch_text.stroke-508"),sQuery(id+"F2.wireOp",EDGE,"E11.sketch_text.stroke-509"),sQuery(id+"F2.wireOp",EDGE,"E11.sketch_text.stroke-510"),sQuery(id+"F2.wireOp",EDGE,"E11.sketch_text.stroke-511"),sQuery(id+"F2.wireOp",EDGE,"E11.sketch_text.stroke-512"),sQuery(id+"F2.wireOp",EDGE,"E11.sketch_text.stroke-513"),sQuery(id+"F2.wireOp",EDGE,"E11.sketch_text.stroke-514"),sQuery(id+"F2.wireOp",EDGE,"E11.sketch_text.stroke-515"),sQuery(id+"F2.wireOp",EDGE,"E11.sketch_text.stroke-516"),sQuery(id+"F2.wireOp",EDGE,"E11.sketch_text.stroke-517"),sQuery(id+"F2.wireOp",EDGE,"E11.sketch_text.stroke-518"),sQuery(id+"F2.wireOp",EDGE,"E11.sketch_text.stroke-519"),sQuery(id+"F2.wireOp",EDGE,"E11.sketch_text.stroke-520"),sQuery(id+"F2.wireOp",EDGE,"E11.sketch_text.stroke-521"),sQuery(id+"F2.wireOp",EDGE,"E11.sketch_text.stroke-522"),sQuery(id+"F2.wireOp",EDGE,"E11.sketch_text.stroke-523"),sQuery(id+"F2.wireOp",EDGE,"E11.sketch_text.stroke-524"),sQuery(id+"F2.wireOp",EDGE,"E11.sketch_text.stroke-525"),sQuery(id+"F2.wireOp",EDGE,"E11.sketch_text.stroke-526"),sQuery(id+"F2.wireOp",EDGE,"E11.sketch_text.stroke-527")])]});
            var Q143;
            Q143=makeQuery(id+"F4.opExtrude","SWEPT_BODY",BODY,{"disambiguationData":[OSD([sQuery(id+"F2.wireOp",EDGE,"E11.sketch_text.stroke-528"),sQuery(id+"F2.wireOp",EDGE,"E11.sketch_text.stroke-529"),sQuery(id+"F2.wireOp",EDGE,"E11.sketch_text.stroke-530"),sQuery(id+"F2.wireOp",EDGE,"E11.sketch_text.stroke-531")])]});
            var Q144;
            Q144=makeQuery(id+"F4.opExtrude","SWEPT_BODY",BODY,{"disambiguationData":[OSD([sQuery(id+"F2.wireOp",EDGE,"E11.sketch_text.stroke-532"),sQuery(id+"F2.wireOp",EDGE,"E11.sketch_text.stroke-533"),sQuery(id+"F2.wireOp",EDGE,"E11.sketch_text.stroke-534"),sQuery(id+"F2.wireOp",EDGE,"E11.sketch_text.stroke-535"),sQuery(id+"F2.wireOp",EDGE,"E11.sketch_text.stroke-536"),sQuery(id+"F2.wireOp",EDGE,"E11.sketch_text.stroke-537"),sQuery(id+"F2.wireOp",EDGE,"E11.sketch_text.stroke-538"),sQuery(id+"F2.wireOp",EDGE,"E11.sketch_text.stroke-539"),sQuery(id+"F2.wireOp",EDGE,"E11.sketch_text.stroke-540"),sQuery(id+"F2.wireOp",EDGE,"E11.sketch_text.stroke-541"),sQuery(id+"F2.wireOp",EDGE,"E11.sketch_text.stroke-542"),sQuery(id+"F2.wireOp",EDGE,"E11.sketch_text.stroke-543"),sQuery(id+"F2.wireOp",EDGE,"E11.sketch_text.stroke-544"),sQuery(id+"F2.wireOp",EDGE,"E11.sketch_text.stroke-545"),sQuery(id+"F2.wireOp",EDGE,"E11.sketch_text.stroke-546"),sQuery(id+"F2.wireOp",EDGE,"E11.sketch_text.stroke-547"),sQuery(id+"F2.wireOp",EDGE,"E11.sketch_text.stroke-548"),sQuery(id+"F2.wireOp",EDGE,"E11.sketch_text.stroke-549"),sQuery(id+"F2.wireOp",EDGE,"E11.sketch_text.stroke-550")])]});
            var Q145;
            Q145=makeQuery(id+"F4.opExtrude","SWEPT_BODY",BODY,{"disambiguationData":[OSD([sQuery(id+"F2.wireOp",EDGE,"E11.sketch_text.stroke-551"),sQuery(id+"F2.wireOp",EDGE,"E11.sketch_text.stroke-552"),sQuery(id+"F2.wireOp",EDGE,"E11.sketch_text.stroke-553"),sQuery(id+"F2.wireOp",EDGE,"E11.sketch_text.stroke-554"),sQuery(id+"F2.wireOp",EDGE,"E11.sketch_text.stroke-555"),sQuery(id+"F2.wireOp",EDGE,"E11.sketch_text.stroke-556"),sQuery(id+"F2.wireOp",EDGE,"E11.sketch_text.stroke-557"),sQuery(id+"F2.wireOp",EDGE,"E11.sketch_text.stroke-558"),sQuery(id+"F2.wireOp",EDGE,"E11.sketch_text.stroke-559"),sQuery(id+"F2.wireOp",EDGE,"E11.sketch_text.stroke-560"),sQuery(id+"F2.wireOp",EDGE,"E11.sketch_text.stroke-561"),sQuery(id+"F2.wireOp",EDGE,"E11.sketch_text.stroke-562"),sQuery(id+"F2.wireOp",EDGE,"E11.sketch_text.stroke-563"),sQuery(id+"F2.wireOp",EDGE,"E11.sketch_text.stroke-564"),sQuery(id+"F2.wireOp",EDGE,"E11.sketch_text.stroke-565"),sQuery(id+"F2.wireOp",EDGE,"E11.sketch_text.stroke-566"),sQuery(id+"F2.wireOp",EDGE,"E11.sketch_text.stroke-567"),sQuery(id+"F2.wireOp",EDGE,"E11.sketch_text.stroke-568"),sQuery(id+"F2.wireOp",EDGE,"E11.sketch_text.stroke-569")])]});
            var Q146;
            Q146=makeQuery(id+"F4.opExtrude","SWEPT_BODY",BODY,{"disambiguationData":[OSD([sQuery(id+"F2.wireOp",EDGE,"E11.sketch_text.stroke-570"),sQuery(id+"F2.wireOp",EDGE,"E11.sketch_text.stroke-571"),sQuery(id+"F2.wireOp",EDGE,"E11.sketch_text.stroke-572"),sQuery(id+"F2.wireOp",EDGE,"E11.sketch_text.stroke-573"),sQuery(id+"F2.wireOp",EDGE,"E11.sketch_text.stroke-574"),sQuery(id+"F2.wireOp",EDGE,"E11.sketch_text.stroke-575"),sQuery(id+"F2.wireOp",EDGE,"E11.sketch_text.stroke-576"),sQuery(id+"F2.wireOp",EDGE,"E11.sketch_text.stroke-577"),sQuery(id+"F2.wireOp",EDGE,"E11.sketch_text.stroke-578"),sQuery(id+"F2.wireOp",EDGE,"E11.sketch_text.stroke-579"),sQuery(id+"F2.wireOp",EDGE,"E11.sketch_text.stroke-580"),sQuery(id+"F2.wireOp",EDGE,"E11.sketch_text.stroke-581"),sQuery(id+"F2.wireOp",EDGE,"E11.sketch_text.stroke-582")])]});
            var Q147;
            Q147=makeQuery(id+"F4.opExtrude","SWEPT_BODY",BODY,{"disambiguationData":[OSD([sQuery(id+"F2.wireOp",EDGE,"E11.sketch_text.stroke-583"),sQuery(id+"F2.wireOp",EDGE,"E11.sketch_text.stroke-584"),sQuery(id+"F2.wireOp",EDGE,"E11.sketch_text.stroke-585"),sQuery(id+"F2.wireOp",EDGE,"E11.sketch_text.stroke-586"),sQuery(id+"F2.wireOp",EDGE,"E11.sketch_text.stroke-587"),sQuery(id+"F2.wireOp",EDGE,"E11.sketch_text.stroke-588"),sQuery(id+"F2.wireOp",EDGE,"E11.sketch_text.stroke-589"),sQuery(id+"F2.wireOp",EDGE,"E11.sketch_text.stroke-590"),sQuery(id+"F2.wireOp",EDGE,"E11.sketch_text.stroke-591"),sQuery(id+"F2.wireOp",EDGE,"E11.sketch_text.stroke-592"),sQuery(id+"F2.wireOp",EDGE,"E11.sketch_text.stroke-593"),sQuery(id+"F2.wireOp",EDGE,"E11.sketch_text.stroke-594"),sQuery(id+"F2.wireOp",EDGE,"E11.sketch_text.stroke-595"),sQuery(id+"F2.wireOp",EDGE,"E11.sketch_text.stroke-596"),sQuery(id+"F2.wireOp",EDGE,"E11.sketch_text.stroke-597"),sQuery(id+"F2.wireOp",EDGE,"E11.sketch_text.stroke-598"),sQuery(id+"F2.wireOp",EDGE,"E11.sketch_text.stroke-599"),sQuery(id+"F2.wireOp",EDGE,"E11.sketch_text.stroke-600")])]});
            var Q148;
            Q148=makeQuery(id+"F4.opExtrude","SWEPT_BODY",BODY,{"disambiguationData":[OSD([sQuery(id+"F2.wireOp",EDGE,"E11.sketch_text.stroke-601"),sQuery(id+"F2.wireOp",EDGE,"E11.sketch_text.stroke-602"),sQuery(id+"F2.wireOp",EDGE,"E11.sketch_text.stroke-603"),sQuery(id+"F2.wireOp",EDGE,"E11.sketch_text.stroke-604"),sQuery(id+"F2.wireOp",EDGE,"E11.sketch_text.stroke-605"),sQuery(id+"F2.wireOp",EDGE,"E11.sketch_text.stroke-606"),sQuery(id+"F2.wireOp",EDGE,"E11.sketch_text.stroke-607"),sQuery(id+"F2.wireOp",EDGE,"E11.sketch_text.stroke-608"),sQuery(id+"F2.wireOp",EDGE,"E11.sketch_text.stroke-609"),sQuery(id+"F2.wireOp",EDGE,"E11.sketch_text.stroke-610"),sQuery(id+"F2.wireOp",EDGE,"E11.sketch_text.stroke-611"),sQuery(id+"F2.wireOp",EDGE,"E11.sketch_text.stroke-612"),sQuery(id+"F2.wireOp",EDGE,"E11.sketch_text.stroke-613"),sQuery(id+"F2.wireOp",EDGE,"E11.sketch_text.stroke-614"),sQuery(id+"F2.wireOp",EDGE,"E11.sketch_text.stroke-615"),sQuery(id+"F2.wireOp",EDGE,"E11.sketch_text.stroke-616"),sQuery(id+"F2.wireOp",EDGE,"E11.sketch_text.stroke-617"),sQuery(id+"F2.wireOp",EDGE,"E11.sketch_text.stroke-618"),sQuery(id+"F2.wireOp",EDGE,"E11.sketch_text.stroke-619"),sQuery(id+"F2.wireOp",EDGE,"E11.sketch_text.stroke-620"),sQuery(id+"F2.wireOp",EDGE,"E11.sketch_text.stroke-621"),sQuery(id+"F2.wireOp",EDGE,"E11.sketch_text.stroke-622"),sQuery(id+"F2.wireOp",EDGE,"E11.sketch_text.stroke-623"),sQuery(id+"F2.wireOp",EDGE,"E11.sketch_text.stroke-624"),sQuery(id+"F2.wireOp",EDGE,"E11.sketch_text.stroke-625"),sQuery(id+"F2.wireOp",EDGE,"E11.sketch_text.stroke-626"),sQuery(id+"F2.wireOp",EDGE,"E11.sketch_text.stroke-627")])]});
            var Q149;
            Q149=makeQuery(id+"F4.opExtrude","SWEPT_BODY",BODY,{"disambiguationData":[OSD([sQuery(id+"F2.wireOp",EDGE,"E11.sketch_text.stroke-628"),sQuery(id+"F2.wireOp",EDGE,"E11.sketch_text.stroke-629"),sQuery(id+"F2.wireOp",EDGE,"E11.sketch_text.stroke-630"),sQuery(id+"F2.wireOp",EDGE,"E11.sketch_text.stroke-631"),sQuery(id+"F2.wireOp",EDGE,"E11.sketch_text.stroke-632"),sQuery(id+"F2.wireOp",EDGE,"E11.sketch_text.stroke-633"),sQuery(id+"F2.wireOp",EDGE,"E11.sketch_text.stroke-634"),sQuery(id+"F2.wireOp",EDGE,"E11.sketch_text.stroke-635"),sQuery(id+"F2.wireOp",EDGE,"E11.sketch_text.stroke-636"),sQuery(id+"F2.wireOp",EDGE,"E11.sketch_text.stroke-637"),sQuery(id+"F2.wireOp",EDGE,"E11.sketch_text.stroke-638"),sQuery(id+"F2.wireOp",EDGE,"E11.sketch_text.stroke-639"),sQuery(id+"F2.wireOp",EDGE,"E11.sketch_text.stroke-640"),sQuery(id+"F2.wireOp",EDGE,"E11.sketch_text.stroke-641"),sQuery(id+"F2.wireOp",EDGE,"E11.sketch_text.stroke-642"),sQuery(id+"F2.wireOp",EDGE,"E11.sketch_text.stroke-643"),sQuery(id+"F2.wireOp",EDGE,"E11.sketch_text.stroke-644")])]});
            var Q150;
            Q150=makeQuery(id+"F4.opExtrude","SWEPT_BODY",BODY,{"disambiguationData":[OSD([sQuery(id+"F2.wireOp",EDGE,"E11.sketch_text.stroke-645"),sQuery(id+"F2.wireOp",EDGE,"E11.sketch_text.stroke-646"),sQuery(id+"F2.wireOp",EDGE,"E11.sketch_text.stroke-647"),sQuery(id+"F2.wireOp",EDGE,"E11.sketch_text.stroke-648"),sQuery(id+"F2.wireOp",EDGE,"E11.sketch_text.stroke-649"),sQuery(id+"F2.wireOp",EDGE,"E11.sketch_text.stroke-650"),sQuery(id+"F2.wireOp",EDGE,"E11.sketch_text.stroke-651"),sQuery(id+"F2.wireOp",EDGE,"E11.sketch_text.stroke-652"),sQuery(id+"F2.wireOp",EDGE,"E11.sketch_text.stroke-653"),sQuery(id+"F2.wireOp",EDGE,"E11.sketch_text.stroke-654"),sQuery(id+"F2.wireOp",EDGE,"E11.sketch_text.stroke-655"),sQuery(id+"F2.wireOp",EDGE,"E11.sketch_text.stroke-656"),sQuery(id+"F2.wireOp",EDGE,"E11.sketch_text.stroke-657"),sQuery(id+"F2.wireOp",EDGE,"E11.sketch_text.stroke-658"),sQuery(id+"F2.wireOp",EDGE,"E11.sketch_text.stroke-659"),sQuery(id+"F2.wireOp",EDGE,"E11.sketch_text.stroke-660"),sQuery(id+"F2.wireOp",EDGE,"E11.sketch_text.stroke-661"),sQuery(id+"F2.wireOp",EDGE,"E11.sketch_text.stroke-662"),sQuery(id+"F2.wireOp",EDGE,"E11.sketch_text.stroke-663"),sQuery(id+"F2.wireOp",EDGE,"E11.sketch_text.stroke-664"),sQuery(id+"F2.wireOp",EDGE,"E11.sketch_text.stroke-665"),sQuery(id+"F2.wireOp",EDGE,"E11.sketch_text.stroke-666"),sQuery(id+"F2.wireOp",EDGE,"E11.sketch_text.stroke-667"),sQuery(id+"F2.wireOp",EDGE,"E11.sketch_text.stroke-668")])]});
            var Q151;
            Q151=makeQuery(id+"F4.opExtrude","SWEPT_BODY",BODY,{"disambiguationData":[OSD([sQuery(id+"F2.wireOp",EDGE,"E11.sketch_text.stroke-669"),sQuery(id+"F2.wireOp",EDGE,"E11.sketch_text.stroke-670"),sQuery(id+"F2.wireOp",EDGE,"E11.sketch_text.stroke-671"),sQuery(id+"F2.wireOp",EDGE,"E11.sketch_text.stroke-672"),sQuery(id+"F2.wireOp",EDGE,"E11.sketch_text.stroke-673"),sQuery(id+"F2.wireOp",EDGE,"E11.sketch_text.stroke-674"),sQuery(id+"F2.wireOp",EDGE,"E11.sketch_text.stroke-675"),sQuery(id+"F2.wireOp",EDGE,"E11.sketch_text.stroke-676"),sQuery(id+"F2.wireOp",EDGE,"E11.sketch_text.stroke-677"),sQuery(id+"F2.wireOp",EDGE,"E11.sketch_text.stroke-678"),sQuery(id+"F2.wireOp",EDGE,"E11.sketch_text.stroke-679"),sQuery(id+"F2.wireOp",EDGE,"E11.sketch_text.stroke-680"),sQuery(id+"F2.wireOp",EDGE,"E11.sketch_text.stroke-681"),sQuery(id+"F2.wireOp",EDGE,"E11.sketch_text.stroke-682"),sQuery(id+"F2.wireOp",EDGE,"E11.sketch_text.stroke-683"),sQuery(id+"F2.wireOp",EDGE,"E11.sketch_text.stroke-684"),sQuery(id+"F2.wireOp",EDGE,"E11.sketch_text.stroke-685")])]});
            var Q152;
            Q152=makeQuery(id+"F4.opExtrude","SWEPT_BODY",BODY,{"disambiguationData":[OSD([sQuery(id+"F2.wireOp",EDGE,"E11.sketch_text.stroke-686"),sQuery(id+"F2.wireOp",EDGE,"E11.sketch_text.stroke-687"),sQuery(id+"F2.wireOp",EDGE,"E11.sketch_text.stroke-688"),sQuery(id+"F2.wireOp",EDGE,"E11.sketch_text.stroke-689")])]});
            var Q153;
            Q153=makeQuery(id+"F4.opExtrude","SWEPT_BODY",BODY,{"disambiguationData":[OSD([sQuery(id+"F2.wireOp",EDGE,"E11.sketch_text.stroke-690"),sQuery(id+"F2.wireOp",EDGE,"E11.sketch_text.stroke-691"),sQuery(id+"F2.wireOp",EDGE,"E11.sketch_text.stroke-692"),sQuery(id+"F2.wireOp",EDGE,"E11.sketch_text.stroke-693"),sQuery(id+"F2.wireOp",EDGE,"E11.sketch_text.stroke-694"),sQuery(id+"F2.wireOp",EDGE,"E11.sketch_text.stroke-695"),sQuery(id+"F2.wireOp",EDGE,"E11.sketch_text.stroke-696"),sQuery(id+"F2.wireOp",EDGE,"E11.sketch_text.stroke-697"),sQuery(id+"F2.wireOp",EDGE,"E11.sketch_text.stroke-698"),sQuery(id+"F2.wireOp",EDGE,"E11.sketch_text.stroke-699"),sQuery(id+"F2.wireOp",EDGE,"E11.sketch_text.stroke-700"),sQuery(id+"F2.wireOp",EDGE,"E11.sketch_text.stroke-701"),sQuery(id+"F2.wireOp",EDGE,"E11.sketch_text.stroke-702"),sQuery(id+"F2.wireOp",EDGE,"E11.sketch_text.stroke-703"),sQuery(id+"F2.wireOp",EDGE,"E11.sketch_text.stroke-704"),sQuery(id+"F2.wireOp",EDGE,"E11.sketch_text.stroke-705"),sQuery(id+"F2.wireOp",EDGE,"E11.sketch_text.stroke-706"),sQuery(id+"F2.wireOp",EDGE,"E11.sketch_text.stroke-707"),sQuery(id+"F2.wireOp",EDGE,"E11.sketch_text.stroke-708"),sQuery(id+"F2.wireOp",EDGE,"E11.sketch_text.stroke-709"),sQuery(id+"F2.wireOp",EDGE,"E11.sketch_text.stroke-710"),sQuery(id+"F2.wireOp",EDGE,"E11.sketch_text.stroke-711"),sQuery(id+"F2.wireOp",EDGE,"E11.sketch_text.stroke-712"),sQuery(id+"F2.wireOp",EDGE,"E11.sketch_text.stroke-713"),sQuery(id+"F2.wireOp",EDGE,"E11.sketch_text.stroke-714")])]});
            var Q154;
            Q154=makeQuery(id+"F4.opExtrude","SWEPT_BODY",BODY,{"disambiguationData":[OSD([sQuery(id+"F2.wireOp",EDGE,"E11.sketch_text.stroke-715"),sQuery(id+"F2.wireOp",EDGE,"E11.sketch_text.stroke-716"),sQuery(id+"F2.wireOp",EDGE,"E11.sketch_text.stroke-717"),sQuery(id+"F2.wireOp",EDGE,"E11.sketch_text.stroke-718"),sQuery(id+"F2.wireOp",EDGE,"E11.sketch_text.stroke-719"),sQuery(id+"F2.wireOp",EDGE,"E11.sketch_text.stroke-720"),sQuery(id+"F2.wireOp",EDGE,"E11.sketch_text.stroke-721"),sQuery(id+"F2.wireOp",EDGE,"E11.sketch_text.stroke-722"),sQuery(id+"F2.wireOp",EDGE,"E11.sketch_text.stroke-723"),sQuery(id+"F2.wireOp",EDGE,"E11.sketch_text.stroke-724"),sQuery(id+"F2.wireOp",EDGE,"E11.sketch_text.stroke-725"),sQuery(id+"F2.wireOp",EDGE,"E11.sketch_text.stroke-726"),sQuery(id+"F2.wireOp",EDGE,"E11.sketch_text.stroke-727"),sQuery(id+"F2.wireOp",EDGE,"E11.sketch_text.stroke-728"),sQuery(id+"F2.wireOp",EDGE,"E11.sketch_text.stroke-729"),sQuery(id+"F2.wireOp",EDGE,"E11.sketch_text.stroke-730"),sQuery(id+"F2.wireOp",EDGE,"E11.sketch_text.stroke-731"),sQuery(id+"F2.wireOp",EDGE,"E11.sketch_text.stroke-732")])]});
            var Q155;
            Q155=makeQuery(id+"F4.opExtrude","SWEPT_BODY",BODY,{"disambiguationData":[OSD([sQuery(id+"F2.wireOp",EDGE,"E12.sketch_text.stroke-0"),sQuery(id+"F2.wireOp",EDGE,"E12.sketch_text.stroke-1"),sQuery(id+"F2.wireOp",EDGE,"E12.sketch_text.stroke-2"),sQuery(id+"F2.wireOp",EDGE,"E12.sketch_text.stroke-3"),sQuery(id+"F2.wireOp",EDGE,"E12.sketch_text.stroke-4"),sQuery(id+"F2.wireOp",EDGE,"E12.sketch_text.stroke-5")])]});
            var Q156;
            Q156=makeQuery(id+"F4.opExtrude","SWEPT_BODY",BODY,{"disambiguationData":[OSD([sQuery(id+"F2.wireOp",EDGE,"E12.sketch_text.stroke-6"),sQuery(id+"F2.wireOp",EDGE,"E12.sketch_text.stroke-7"),sQuery(id+"F2.wireOp",EDGE,"E12.sketch_text.stroke-8"),sQuery(id+"F2.wireOp",EDGE,"E12.sketch_text.stroke-9"),sQuery(id+"F2.wireOp",EDGE,"E12.sketch_text.stroke-10"),sQuery(id+"F2.wireOp",EDGE,"E12.sketch_text.stroke-11"),sQuery(id+"F2.wireOp",EDGE,"E12.sketch_text.stroke-12"),sQuery(id+"F2.wireOp",EDGE,"E12.sketch_text.stroke-13"),sQuery(id+"F2.wireOp",EDGE,"E12.sketch_text.stroke-14"),sQuery(id+"F2.wireOp",EDGE,"E12.sketch_text.stroke-15"),sQuery(id+"F2.wireOp",EDGE,"E12.sketch_text.stroke-16"),sQuery(id+"F2.wireOp",EDGE,"E12.sketch_text.stroke-17"),sQuery(id+"F2.wireOp",EDGE,"E12.sketch_text.stroke-18"),sQuery(id+"F2.wireOp",EDGE,"E12.sketch_text.stroke-19"),sQuery(id+"F2.wireOp",EDGE,"E12.sketch_text.stroke-20"),sQuery(id+"F2.wireOp",EDGE,"E12.sketch_text.stroke-21"),sQuery(id+"F2.wireOp",EDGE,"E12.sketch_text.stroke-22"),sQuery(id+"F2.wireOp",EDGE,"E12.sketch_text.stroke-23"),sQuery(id+"F2.wireOp",EDGE,"E12.sketch_text.stroke-24"),sQuery(id+"F2.wireOp",EDGE,"E12.sketch_text.stroke-25"),sQuery(id+"F2.wireOp",EDGE,"E12.sketch_text.stroke-26"),sQuery(id+"F2.wireOp",EDGE,"E12.sketch_text.stroke-27"),sQuery(id+"F2.wireOp",EDGE,"E12.sketch_text.stroke-28"),sQuery(id+"F2.wireOp",EDGE,"E12.sketch_text.stroke-29"),sQuery(id+"F2.wireOp",EDGE,"E12.sketch_text.stroke-30"),sQuery(id+"F2.wireOp",EDGE,"E12.sketch_text.stroke-31"),sQuery(id+"F2.wireOp",EDGE,"E12.sketch_text.stroke-32")])]});
            var Q157;
            Q157=makeQuery(id+"F4.opExtrude","SWEPT_BODY",BODY,{"disambiguationData":[OSD([sQuery(id+"F2.wireOp",EDGE,"E12.sketch_text.stroke-33"),sQuery(id+"F2.wireOp",EDGE,"E12.sketch_text.stroke-34"),sQuery(id+"F2.wireOp",EDGE,"E12.sketch_text.stroke-35"),sQuery(id+"F2.wireOp",EDGE,"E12.sketch_text.stroke-36"),sQuery(id+"F2.wireOp",EDGE,"E12.sketch_text.stroke-37"),sQuery(id+"F2.wireOp",EDGE,"E12.sketch_text.stroke-38"),sQuery(id+"F2.wireOp",EDGE,"E12.sketch_text.stroke-39"),sQuery(id+"F2.wireOp",EDGE,"E12.sketch_text.stroke-40"),sQuery(id+"F2.wireOp",EDGE,"E12.sketch_text.stroke-41"),sQuery(id+"F2.wireOp",EDGE,"E12.sketch_text.stroke-42"),sQuery(id+"F2.wireOp",EDGE,"E12.sketch_text.stroke-43"),sQuery(id+"F2.wireOp",EDGE,"E12.sketch_text.stroke-44"),sQuery(id+"F2.wireOp",EDGE,"E12.sketch_text.stroke-45"),sQuery(id+"F2.wireOp",EDGE,"E12.sketch_text.stroke-46"),sQuery(id+"F2.wireOp",EDGE,"E12.sketch_text.stroke-47"),sQuery(id+"F2.wireOp",EDGE,"E12.sketch_text.stroke-48"),sQuery(id+"F2.wireOp",EDGE,"E12.sketch_text.stroke-49")])]});
            var Q158;
            Q158=makeQuery(id+"F4.opExtrude","SWEPT_BODY",BODY,{"disambiguationData":[OSD([sQuery(id+"F2.wireOp",EDGE,"E12.sketch_text.stroke-50"),sQuery(id+"F2.wireOp",EDGE,"E12.sketch_text.stroke-51"),sQuery(id+"F2.wireOp",EDGE,"E12.sketch_text.stroke-52"),sQuery(id+"F2.wireOp",EDGE,"E12.sketch_text.stroke-53"),sQuery(id+"F2.wireOp",EDGE,"E12.sketch_text.stroke-54"),sQuery(id+"F2.wireOp",EDGE,"E12.sketch_text.stroke-55"),sQuery(id+"F2.wireOp",EDGE,"E12.sketch_text.stroke-56"),sQuery(id+"F2.wireOp",EDGE,"E12.sketch_text.stroke-57"),sQuery(id+"F2.wireOp",EDGE,"E12.sketch_text.stroke-58"),sQuery(id+"F2.wireOp",EDGE,"E12.sketch_text.stroke-59"),sQuery(id+"F2.wireOp",EDGE,"E12.sketch_text.stroke-60"),sQuery(id+"F2.wireOp",EDGE,"E12.sketch_text.stroke-61"),sQuery(id+"F2.wireOp",EDGE,"E12.sketch_text.stroke-62"),sQuery(id+"F2.wireOp",EDGE,"E12.sketch_text.stroke-63"),sQuery(id+"F2.wireOp",EDGE,"E12.sketch_text.stroke-64"),sQuery(id+"F2.wireOp",EDGE,"E12.sketch_text.stroke-65"),sQuery(id+"F2.wireOp",EDGE,"E12.sketch_text.stroke-66")])]});
            var Q159;
            Q159=makeQuery(id+"F4.opExtrude","SWEPT_BODY",BODY,{"disambiguationData":[OSD([sQuery(id+"F2.wireOp",EDGE,"E12.sketch_text.stroke-67"),sQuery(id+"F2.wireOp",EDGE,"E12.sketch_text.stroke-68"),sQuery(id+"F2.wireOp",EDGE,"E12.sketch_text.stroke-69"),sQuery(id+"F2.wireOp",EDGE,"E12.sketch_text.stroke-70"),sQuery(id+"F2.wireOp",EDGE,"E12.sketch_text.stroke-71"),sQuery(id+"F2.wireOp",EDGE,"E12.sketch_text.stroke-72"),sQuery(id+"F2.wireOp",EDGE,"E12.sketch_text.stroke-73"),sQuery(id+"F2.wireOp",EDGE,"E12.sketch_text.stroke-74"),sQuery(id+"F2.wireOp",EDGE,"E12.sketch_text.stroke-75"),sQuery(id+"F2.wireOp",EDGE,"E12.sketch_text.stroke-76"),sQuery(id+"F2.wireOp",EDGE,"E12.sketch_text.stroke-77"),sQuery(id+"F2.wireOp",EDGE,"E12.sketch_text.stroke-78"),sQuery(id+"F2.wireOp",EDGE,"E12.sketch_text.stroke-79"),sQuery(id+"F2.wireOp",EDGE,"E12.sketch_text.stroke-80"),sQuery(id+"F2.wireOp",EDGE,"E12.sketch_text.stroke-81")])]});
            var Q160;
            Q160=makeQuery(id+"F4.opExtrude","SWEPT_BODY",BODY,{"disambiguationData":[OSD([sQuery(id+"F2.wireOp",EDGE,"E12.sketch_text.stroke-82"),sQuery(id+"F2.wireOp",EDGE,"E12.sketch_text.stroke-83"),sQuery(id+"F2.wireOp",EDGE,"E12.sketch_text.stroke-84"),sQuery(id+"F2.wireOp",EDGE,"E12.sketch_text.stroke-85"),sQuery(id+"F2.wireOp",EDGE,"E12.sketch_text.stroke-86"),sQuery(id+"F2.wireOp",EDGE,"E12.sketch_text.stroke-87"),sQuery(id+"F2.wireOp",EDGE,"E12.sketch_text.stroke-88"),sQuery(id+"F2.wireOp",EDGE,"E12.sketch_text.stroke-89"),sQuery(id+"F2.wireOp",EDGE,"E12.sketch_text.stroke-90"),sQuery(id+"F2.wireOp",EDGE,"E12.sketch_text.stroke-91"),sQuery(id+"F2.wireOp",EDGE,"E12.sketch_text.stroke-92"),sQuery(id+"F2.wireOp",EDGE,"E12.sketch_text.stroke-93"),sQuery(id+"F2.wireOp",EDGE,"E12.sketch_text.stroke-94"),sQuery(id+"F2.wireOp",EDGE,"E12.sketch_text.stroke-95"),sQuery(id+"F2.wireOp",EDGE,"E12.sketch_text.stroke-96"),sQuery(id+"F2.wireOp",EDGE,"E12.sketch_text.stroke-97"),sQuery(id+"F2.wireOp",EDGE,"E12.sketch_text.stroke-98"),sQuery(id+"F2.wireOp",EDGE,"E12.sketch_text.stroke-99")])]});
            var Q161;
            Q161=makeQuery(id+"F4.opExtrude","SWEPT_BODY",BODY,{"disambiguationData":[OSD([sQuery(id+"F2.wireOp",EDGE,"E12.sketch_text.stroke-100"),sQuery(id+"F2.wireOp",EDGE,"E12.sketch_text.stroke-101"),sQuery(id+"F2.wireOp",EDGE,"E12.sketch_text.stroke-102"),sQuery(id+"F2.wireOp",EDGE,"E12.sketch_text.stroke-103"),sQuery(id+"F2.wireOp",EDGE,"E12.sketch_text.stroke-104"),sQuery(id+"F2.wireOp",EDGE,"E12.sketch_text.stroke-105"),sQuery(id+"F2.wireOp",EDGE,"E12.sketch_text.stroke-106"),sQuery(id+"F2.wireOp",EDGE,"E12.sketch_text.stroke-107"),sQuery(id+"F2.wireOp",EDGE,"E12.sketch_text.stroke-108"),sQuery(id+"F2.wireOp",EDGE,"E12.sketch_text.stroke-109"),sQuery(id+"F2.wireOp",EDGE,"E12.sketch_text.stroke-110"),sQuery(id+"F2.wireOp",EDGE,"E12.sketch_text.stroke-111"),sQuery(id+"F2.wireOp",EDGE,"E12.sketch_text.stroke-112"),sQuery(id+"F2.wireOp",EDGE,"E12.sketch_text.stroke-113"),sQuery(id+"F2.wireOp",EDGE,"E12.sketch_text.stroke-114"),sQuery(id+"F2.wireOp",EDGE,"E12.sketch_text.stroke-115"),sQuery(id+"F2.wireOp",EDGE,"E12.sketch_text.stroke-116"),sQuery(id+"F2.wireOp",EDGE,"E12.sketch_text.stroke-117"),sQuery(id+"F2.wireOp",EDGE,"E12.sketch_text.stroke-118")])]});
            var Q162;
            Q162=makeQuery(id+"F4.opExtrude","SWEPT_BODY",BODY,{"disambiguationData":[OSD([sQuery(id+"F2.wireOp",EDGE,"E12.sketch_text.stroke-119"),sQuery(id+"F2.wireOp",EDGE,"E12.sketch_text.stroke-120"),sQuery(id+"F2.wireOp",EDGE,"E12.sketch_text.stroke-121"),sQuery(id+"F2.wireOp",EDGE,"E12.sketch_text.stroke-122"),sQuery(id+"F2.wireOp",EDGE,"E12.sketch_text.stroke-123"),sQuery(id+"F2.wireOp",EDGE,"E12.sketch_text.stroke-124"),sQuery(id+"F2.wireOp",EDGE,"E12.sketch_text.stroke-125"),sQuery(id+"F2.wireOp",EDGE,"E12.sketch_text.stroke-126"),sQuery(id+"F2.wireOp",EDGE,"E12.sketch_text.stroke-127"),sQuery(id+"F2.wireOp",EDGE,"E12.sketch_text.stroke-128"),sQuery(id+"F2.wireOp",EDGE,"E12.sketch_text.stroke-129"),sQuery(id+"F2.wireOp",EDGE,"E12.sketch_text.stroke-130"),sQuery(id+"F2.wireOp",EDGE,"E12.sketch_text.stroke-131"),sQuery(id+"F2.wireOp",EDGE,"E12.sketch_text.stroke-132"),sQuery(id+"F2.wireOp",EDGE,"E12.sketch_text.stroke-133"),sQuery(id+"F2.wireOp",EDGE,"E12.sketch_text.stroke-134"),sQuery(id+"F2.wireOp",EDGE,"E12.sketch_text.stroke-135"),sQuery(id+"F2.wireOp",EDGE,"E12.sketch_text.stroke-136"),sQuery(id+"F2.wireOp",EDGE,"E12.sketch_text.stroke-137"),sQuery(id+"F2.wireOp",EDGE,"E12.sketch_text.stroke-138"),sQuery(id+"F2.wireOp",EDGE,"E12.sketch_text.stroke-139"),sQuery(id+"F2.wireOp",EDGE,"E12.sketch_text.stroke-140"),sQuery(id+"F2.wireOp",EDGE,"E12.sketch_text.stroke-141"),sQuery(id+"F2.wireOp",EDGE,"E12.sketch_text.stroke-142")])]});
            var Q163;
            Q163=makeQuery(id+"F4.opExtrude","SWEPT_BODY",BODY,{"disambiguationData":[OSD([sQuery(id+"F2.wireOp",EDGE,"E12.sketch_text.stroke-143"),sQuery(id+"F2.wireOp",EDGE,"E12.sketch_text.stroke-144"),sQuery(id+"F2.wireOp",EDGE,"E12.sketch_text.stroke-145"),sQuery(id+"F2.wireOp",EDGE,"E12.sketch_text.stroke-146"),sQuery(id+"F2.wireOp",EDGE,"E12.sketch_text.stroke-147"),sQuery(id+"F2.wireOp",EDGE,"E12.sketch_text.stroke-148"),sQuery(id+"F2.wireOp",EDGE,"E12.sketch_text.stroke-149"),sQuery(id+"F2.wireOp",EDGE,"E12.sketch_text.stroke-150"),sQuery(id+"F2.wireOp",EDGE,"E12.sketch_text.stroke-151"),sQuery(id+"F2.wireOp",EDGE,"E12.sketch_text.stroke-152"),sQuery(id+"F2.wireOp",EDGE,"E12.sketch_text.stroke-153"),sQuery(id+"F2.wireOp",EDGE,"E12.sketch_text.stroke-154"),sQuery(id+"F2.wireOp",EDGE,"E12.sketch_text.stroke-155")])]});
            var Q164;
            Q164=makeQuery(id+"F4.opExtrude","SWEPT_BODY",BODY,{"disambiguationData":[OSD([sQuery(id+"F2.wireOp",EDGE,"E12.sketch_text.stroke-156"),sQuery(id+"F2.wireOp",EDGE,"E12.sketch_text.stroke-157"),sQuery(id+"F2.wireOp",EDGE,"E12.sketch_text.stroke-158"),sQuery(id+"F2.wireOp",EDGE,"E12.sketch_text.stroke-159"),sQuery(id+"F2.wireOp",EDGE,"E12.sketch_text.stroke-160"),sQuery(id+"F2.wireOp",EDGE,"E12.sketch_text.stroke-161"),sQuery(id+"F2.wireOp",EDGE,"E12.sketch_text.stroke-162"),sQuery(id+"F2.wireOp",EDGE,"E12.sketch_text.stroke-163"),sQuery(id+"F2.wireOp",EDGE,"E12.sketch_text.stroke-164"),sQuery(id+"F2.wireOp",EDGE,"E12.sketch_text.stroke-165"),sQuery(id+"F2.wireOp",EDGE,"E12.sketch_text.stroke-166"),sQuery(id+"F2.wireOp",EDGE,"E12.sketch_text.stroke-167"),sQuery(id+"F2.wireOp",EDGE,"E12.sketch_text.stroke-168"),sQuery(id+"F2.wireOp",EDGE,"E12.sketch_text.stroke-169"),sQuery(id+"F2.wireOp",EDGE,"E12.sketch_text.stroke-170"),sQuery(id+"F2.wireOp",EDGE,"E12.sketch_text.stroke-171"),sQuery(id+"F2.wireOp",EDGE,"E12.sketch_text.stroke-172")])]});
            var Q165;
            Q165=makeQuery(id+"F4.opExtrude","SWEPT_BODY",BODY,{"disambiguationData":[OSD([sQuery(id+"F2.wireOp",EDGE,"E12.sketch_text.stroke-173"),sQuery(id+"F2.wireOp",EDGE,"E12.sketch_text.stroke-174"),sQuery(id+"F2.wireOp",EDGE,"E12.sketch_text.stroke-175"),sQuery(id+"F2.wireOp",EDGE,"E12.sketch_text.stroke-176"),sQuery(id+"F2.wireOp",EDGE,"E12.sketch_text.stroke-177"),sQuery(id+"F2.wireOp",EDGE,"E12.sketch_text.stroke-178"),sQuery(id+"F2.wireOp",EDGE,"E12.sketch_text.stroke-179"),sQuery(id+"F2.wireOp",EDGE,"E12.sketch_text.stroke-180"),sQuery(id+"F2.wireOp",EDGE,"E12.sketch_text.stroke-181"),sQuery(id+"F2.wireOp",EDGE,"E12.sketch_text.stroke-182"),sQuery(id+"F2.wireOp",EDGE,"E12.sketch_text.stroke-183"),sQuery(id+"F2.wireOp",EDGE,"E12.sketch_text.stroke-184"),sQuery(id+"F2.wireOp",EDGE,"E12.sketch_text.stroke-185"),sQuery(id+"F2.wireOp",EDGE,"E12.sketch_text.stroke-186"),sQuery(id+"F2.wireOp",EDGE,"E12.sketch_text.stroke-187"),sQuery(id+"F2.wireOp",EDGE,"E12.sketch_text.stroke-188"),sQuery(id+"F2.wireOp",EDGE,"E12.sketch_text.stroke-189"),sQuery(id+"F2.wireOp",EDGE,"E12.sketch_text.stroke-190"),sQuery(id+"F2.wireOp",EDGE,"E12.sketch_text.stroke-191"),sQuery(id+"F2.wireOp",EDGE,"E12.sketch_text.stroke-192"),sQuery(id+"F2.wireOp",EDGE,"E12.sketch_text.stroke-193"),sQuery(id+"F2.wireOp",EDGE,"E12.sketch_text.stroke-194"),sQuery(id+"F2.wireOp",EDGE,"E12.sketch_text.stroke-195"),sQuery(id+"F2.wireOp",EDGE,"E12.sketch_text.stroke-196"),sQuery(id+"F2.wireOp",EDGE,"E12.sketch_text.stroke-197"),sQuery(id+"F2.wireOp",EDGE,"E12.sketch_text.stroke-198"),sQuery(id+"F2.wireOp",EDGE,"E12.sketch_text.stroke-199"),sQuery(id+"F2.wireOp",EDGE,"E12.sketch_text.stroke-200"),sQuery(id+"F2.wireOp",EDGE,"E12.sketch_text.stroke-201"),sQuery(id+"F2.wireOp",EDGE,"E12.sketch_text.stroke-202"),sQuery(id+"F2.wireOp",EDGE,"E12.sketch_text.stroke-203"),sQuery(id+"F2.wireOp",EDGE,"E12.sketch_text.stroke-204"),sQuery(id+"F2.wireOp",EDGE,"E12.sketch_text.stroke-205"),sQuery(id+"F2.wireOp",EDGE,"E12.sketch_text.stroke-206"),sQuery(id+"F2.wireOp",EDGE,"E12.sketch_text.stroke-207"),sQuery(id+"F2.wireOp",EDGE,"E12.sketch_text.stroke-208"),sQuery(id+"F2.wireOp",EDGE,"E12.sketch_text.stroke-209"),sQuery(id+"F2.wireOp",EDGE,"E12.sketch_text.stroke-210"),sQuery(id+"F2.wireOp",EDGE,"E12.sketch_text.stroke-211"),sQuery(id+"F2.wireOp",EDGE,"E12.sketch_text.stroke-212"),sQuery(id+"F2.wireOp",EDGE,"E12.sketch_text.stroke-213"),sQuery(id+"F2.wireOp",EDGE,"E12.sketch_text.stroke-214"),sQuery(id+"F2.wireOp",EDGE,"E12.sketch_text.stroke-215"),sQuery(id+"F2.wireOp",EDGE,"E12.sketch_text.stroke-216")])]});
            var Q166;
            Q166=makeQuery(id+"F4.opExtrude","SWEPT_BODY",BODY,{"disambiguationData":[OSD([sQuery(id+"F2.wireOp",EDGE,"E12.sketch_text.stroke-217"),sQuery(id+"F2.wireOp",EDGE,"E12.sketch_text.stroke-218"),sQuery(id+"F2.wireOp",EDGE,"E12.sketch_text.stroke-219"),sQuery(id+"F2.wireOp",EDGE,"E12.sketch_text.stroke-220"),sQuery(id+"F2.wireOp",EDGE,"E12.sketch_text.stroke-221"),sQuery(id+"F2.wireOp",EDGE,"E12.sketch_text.stroke-222"),sQuery(id+"F2.wireOp",EDGE,"E12.sketch_text.stroke-223"),sQuery(id+"F2.wireOp",EDGE,"E12.sketch_text.stroke-224"),sQuery(id+"F2.wireOp",EDGE,"E12.sketch_text.stroke-225"),sQuery(id+"F2.wireOp",EDGE,"E12.sketch_text.stroke-226"),sQuery(id+"F2.wireOp",EDGE,"E12.sketch_text.stroke-227"),sQuery(id+"F2.wireOp",EDGE,"E12.sketch_text.stroke-228"),sQuery(id+"F2.wireOp",EDGE,"E12.sketch_text.stroke-229"),sQuery(id+"F2.wireOp",EDGE,"E12.sketch_text.stroke-230"),sQuery(id+"F2.wireOp",EDGE,"E12.sketch_text.stroke-231"),sQuery(id+"F2.wireOp",EDGE,"E12.sketch_text.stroke-232"),sQuery(id+"F2.wireOp",EDGE,"E12.sketch_text.stroke-233")])]});
            var Q167;
            Q167=makeQuery(id+"F4.opExtrude","SWEPT_BODY",BODY,{"disambiguationData":[OSD([sQuery(id+"F2.wireOp",EDGE,"E12.sketch_text.stroke-234"),sQuery(id+"F2.wireOp",EDGE,"E12.sketch_text.stroke-235"),sQuery(id+"F2.wireOp",EDGE,"E12.sketch_text.stroke-236"),sQuery(id+"F2.wireOp",EDGE,"E12.sketch_text.stroke-237"),sQuery(id+"F2.wireOp",EDGE,"E12.sketch_text.stroke-238"),sQuery(id+"F2.wireOp",EDGE,"E12.sketch_text.stroke-239"),sQuery(id+"F2.wireOp",EDGE,"E12.sketch_text.stroke-240"),sQuery(id+"F2.wireOp",EDGE,"E12.sketch_text.stroke-241"),sQuery(id+"F2.wireOp",EDGE,"E12.sketch_text.stroke-242"),sQuery(id+"F2.wireOp",EDGE,"E12.sketch_text.stroke-243"),sQuery(id+"F2.wireOp",EDGE,"E12.sketch_text.stroke-244"),sQuery(id+"F2.wireOp",EDGE,"E12.sketch_text.stroke-245"),sQuery(id+"F2.wireOp",EDGE,"E12.sketch_text.stroke-246"),sQuery(id+"F2.wireOp",EDGE,"E12.sketch_text.stroke-247"),sQuery(id+"F2.wireOp",EDGE,"E12.sketch_text.stroke-248"),sQuery(id+"F2.wireOp",EDGE,"E12.sketch_text.stroke-249"),sQuery(id+"F2.wireOp",EDGE,"E12.sketch_text.stroke-250"),sQuery(id+"F2.wireOp",EDGE,"E12.sketch_text.stroke-251"),sQuery(id+"F2.wireOp",EDGE,"E12.sketch_text.stroke-252"),sQuery(id+"F2.wireOp",EDGE,"E12.sketch_text.stroke-253"),sQuery(id+"F2.wireOp",EDGE,"E12.sketch_text.stroke-254"),sQuery(id+"F2.wireOp",EDGE,"E12.sketch_text.stroke-255"),sQuery(id+"F2.wireOp",EDGE,"E12.sketch_text.stroke-256"),sQuery(id+"F2.wireOp",EDGE,"E12.sketch_text.stroke-257"),sQuery(id+"F2.wireOp",EDGE,"E12.sketch_text.stroke-258")])]});
            var Q168;
            Q168=makeQuery(id+"F4.opExtrude","SWEPT_BODY",BODY,{"disambiguationData":[OSD([sQuery(id+"F2.wireOp",EDGE,"E12.sketch_text.stroke-259"),sQuery(id+"F2.wireOp",EDGE,"E12.sketch_text.stroke-260"),sQuery(id+"F2.wireOp",EDGE,"E12.sketch_text.stroke-261"),sQuery(id+"F2.wireOp",EDGE,"E12.sketch_text.stroke-262"),sQuery(id+"F2.wireOp",EDGE,"E12.sketch_text.stroke-263"),sQuery(id+"F2.wireOp",EDGE,"E12.sketch_text.stroke-264"),sQuery(id+"F2.wireOp",EDGE,"E12.sketch_text.stroke-265"),sQuery(id+"F2.wireOp",EDGE,"E12.sketch_text.stroke-266"),sQuery(id+"F2.wireOp",EDGE,"E12.sketch_text.stroke-267"),sQuery(id+"F2.wireOp",EDGE,"E12.sketch_text.stroke-268"),sQuery(id+"F2.wireOp",EDGE,"E12.sketch_text.stroke-269"),sQuery(id+"F2.wireOp",EDGE,"E12.sketch_text.stroke-270"),sQuery(id+"F2.wireOp",EDGE,"E12.sketch_text.stroke-271"),sQuery(id+"F2.wireOp",EDGE,"E12.sketch_text.stroke-272"),sQuery(id+"F2.wireOp",EDGE,"E12.sketch_text.stroke-273"),sQuery(id+"F2.wireOp",EDGE,"E12.sketch_text.stroke-274"),sQuery(id+"F2.wireOp",EDGE,"E12.sketch_text.stroke-275"),sQuery(id+"F2.wireOp",EDGE,"E12.sketch_text.stroke-276"),sQuery(id+"F2.wireOp",EDGE,"E12.sketch_text.stroke-277")])]});
            var Q169;
            Q169=makeQuery(id+"F4.opExtrude","SWEPT_BODY",BODY,{"disambiguationData":[OSD([sQuery(id+"F2.wireOp",EDGE,"E12.sketch_text.stroke-278"),sQuery(id+"F2.wireOp",EDGE,"E12.sketch_text.stroke-279"),sQuery(id+"F2.wireOp",EDGE,"E12.sketch_text.stroke-280"),sQuery(id+"F2.wireOp",EDGE,"E12.sketch_text.stroke-281"),sQuery(id+"F2.wireOp",EDGE,"E12.sketch_text.stroke-282"),sQuery(id+"F2.wireOp",EDGE,"E12.sketch_text.stroke-283"),sQuery(id+"F2.wireOp",EDGE,"E12.sketch_text.stroke-284"),sQuery(id+"F2.wireOp",EDGE,"E12.sketch_text.stroke-285"),sQuery(id+"F2.wireOp",EDGE,"E12.sketch_text.stroke-286")])]});
            var Q170;
            Q170=makeQuery(id+"F4.opExtrude","SWEPT_BODY",BODY,{"disambiguationData":[OSD([sQuery(id+"F2.wireOp",EDGE,"E12.sketch_text.stroke-287"),sQuery(id+"F2.wireOp",EDGE,"E12.sketch_text.stroke-288"),sQuery(id+"F2.wireOp",EDGE,"E12.sketch_text.stroke-289"),sQuery(id+"F2.wireOp",EDGE,"E12.sketch_text.stroke-290"),sQuery(id+"F2.wireOp",EDGE,"E12.sketch_text.stroke-291"),sQuery(id+"F2.wireOp",EDGE,"E12.sketch_text.stroke-292"),sQuery(id+"F2.wireOp",EDGE,"E12.sketch_text.stroke-293"),sQuery(id+"F2.wireOp",EDGE,"E12.sketch_text.stroke-294"),sQuery(id+"F2.wireOp",EDGE,"E12.sketch_text.stroke-295"),sQuery(id+"F2.wireOp",EDGE,"E12.sketch_text.stroke-296"),sQuery(id+"F2.wireOp",EDGE,"E12.sketch_text.stroke-297"),sQuery(id+"F2.wireOp",EDGE,"E12.sketch_text.stroke-298"),sQuery(id+"F2.wireOp",EDGE,"E12.sketch_text.stroke-299"),sQuery(id+"F2.wireOp",EDGE,"E12.sketch_text.stroke-300"),sQuery(id+"F2.wireOp",EDGE,"E12.sketch_text.stroke-301"),sQuery(id+"F2.wireOp",EDGE,"E12.sketch_text.stroke-302"),sQuery(id+"F2.wireOp",EDGE,"E12.sketch_text.stroke-303"),sQuery(id+"F2.wireOp",EDGE,"E12.sketch_text.stroke-304"),sQuery(id+"F2.wireOp",EDGE,"E12.sketch_text.stroke-305"),sQuery(id+"F2.wireOp",EDGE,"E12.sketch_text.stroke-306"),sQuery(id+"F2.wireOp",EDGE,"E12.sketch_text.stroke-307"),sQuery(id+"F2.wireOp",EDGE,"E12.sketch_text.stroke-308"),sQuery(id+"F2.wireOp",EDGE,"E12.sketch_text.stroke-309"),sQuery(id+"F2.wireOp",EDGE,"E12.sketch_text.stroke-310"),sQuery(id+"F2.wireOp",EDGE,"E12.sketch_text.stroke-311"),sQuery(id+"F2.wireOp",EDGE,"E12.sketch_text.stroke-312")])]});
            var Q171;
            Q171=makeQuery(id+"F4.opExtrude","SWEPT_BODY",BODY,{"disambiguationData":[OSD([sQuery(id+"F2.wireOp",EDGE,"E12.sketch_text.stroke-313"),sQuery(id+"F2.wireOp",EDGE,"E12.sketch_text.stroke-314"),sQuery(id+"F2.wireOp",EDGE,"E12.sketch_text.stroke-315"),sQuery(id+"F2.wireOp",EDGE,"E12.sketch_text.stroke-316"),sQuery(id+"F2.wireOp",EDGE,"E12.sketch_text.stroke-317"),sQuery(id+"F2.wireOp",EDGE,"E12.sketch_text.stroke-318"),sQuery(id+"F2.wireOp",EDGE,"E12.sketch_text.stroke-319"),sQuery(id+"F2.wireOp",EDGE,"E12.sketch_text.stroke-320"),sQuery(id+"F2.wireOp",EDGE,"E12.sketch_text.stroke-321"),sQuery(id+"F2.wireOp",EDGE,"E12.sketch_text.stroke-322"),sQuery(id+"F2.wireOp",EDGE,"E12.sketch_text.stroke-323"),sQuery(id+"F2.wireOp",EDGE,"E12.sketch_text.stroke-324"),sQuery(id+"F2.wireOp",EDGE,"E12.sketch_text.stroke-325"),sQuery(id+"F2.wireOp",EDGE,"E12.sketch_text.stroke-326"),sQuery(id+"F2.wireOp",EDGE,"E12.sketch_text.stroke-327"),sQuery(id+"F2.wireOp",EDGE,"E12.sketch_text.stroke-328"),sQuery(id+"F2.wireOp",EDGE,"E12.sketch_text.stroke-329"),sQuery(id+"F2.wireOp",EDGE,"E12.sketch_text.stroke-330"),sQuery(id+"F2.wireOp",EDGE,"E12.sketch_text.stroke-331"),sQuery(id+"F2.wireOp",EDGE,"E12.sketch_text.stroke-332"),sQuery(id+"F2.wireOp",EDGE,"E12.sketch_text.stroke-333"),sQuery(id+"F2.wireOp",EDGE,"E12.sketch_text.stroke-334"),sQuery(id+"F2.wireOp",EDGE,"E12.sketch_text.stroke-335"),sQuery(id+"F2.wireOp",EDGE,"E12.sketch_text.stroke-336"),sQuery(id+"F2.wireOp",EDGE,"E12.sketch_text.stroke-337"),sQuery(id+"F2.wireOp",EDGE,"E12.sketch_text.stroke-338")])]});
            var Q172;
            Q172=makeQuery(id+"F4.opExtrude","SWEPT_BODY",BODY,{"disambiguationData":[OSD([sQuery(id+"F2.wireOp",EDGE,"E12.sketch_text.stroke-339"),sQuery(id+"F2.wireOp",EDGE,"E12.sketch_text.stroke-340"),sQuery(id+"F2.wireOp",EDGE,"E12.sketch_text.stroke-341"),sQuery(id+"F2.wireOp",EDGE,"E12.sketch_text.stroke-342"),sQuery(id+"F2.wireOp",EDGE,"E12.sketch_text.stroke-343"),sQuery(id+"F2.wireOp",EDGE,"E12.sketch_text.stroke-344"),sQuery(id+"F2.wireOp",EDGE,"E12.sketch_text.stroke-345"),sQuery(id+"F2.wireOp",EDGE,"E12.sketch_text.stroke-346"),sQuery(id+"F2.wireOp",EDGE,"E12.sketch_text.stroke-347")])]});
            var Q173;
            Q173=makeQuery(id+"F4.opExtrude","SWEPT_BODY",BODY,{"disambiguationData":[OSD([sQuery(id+"F2.wireOp",EDGE,"E13.sketch_text.stroke-0"),sQuery(id+"F2.wireOp",EDGE,"E13.sketch_text.stroke-1"),sQuery(id+"F2.wireOp",EDGE,"E13.sketch_text.stroke-2"),sQuery(id+"F2.wireOp",EDGE,"E13.sketch_text.stroke-3"),sQuery(id+"F2.wireOp",EDGE,"E13.sketch_text.stroke-4"),sQuery(id+"F2.wireOp",EDGE,"E13.sketch_text.stroke-5"),sQuery(id+"F2.wireOp",EDGE,"E13.sketch_text.stroke-6"),sQuery(id+"F2.wireOp",EDGE,"E13.sketch_text.stroke-7"),sQuery(id+"F2.wireOp",EDGE,"E13.sketch_text.stroke-8"),sQuery(id+"F2.wireOp",EDGE,"E13.sketch_text.stroke-9"),sQuery(id+"F2.wireOp",EDGE,"E13.sketch_text.stroke-10"),sQuery(id+"F2.wireOp",EDGE,"E13.sketch_text.stroke-11")])]});
            var Q174;
            Q174=makeQuery(id+"F4.opExtrude","SWEPT_BODY",BODY,{"disambiguationData":[OSD([sQuery(id+"F2.wireOp",EDGE,"E13.sketch_text.stroke-12"),sQuery(id+"F2.wireOp",EDGE,"E13.sketch_text.stroke-13"),sQuery(id+"F2.wireOp",EDGE,"E13.sketch_text.stroke-14"),sQuery(id+"F2.wireOp",EDGE,"E13.sketch_text.stroke-15"),sQuery(id+"F2.wireOp",EDGE,"E13.sketch_text.stroke-16"),sQuery(id+"F2.wireOp",EDGE,"E13.sketch_text.stroke-17"),sQuery(id+"F2.wireOp",EDGE,"E13.sketch_text.stroke-18"),sQuery(id+"F2.wireOp",EDGE,"E13.sketch_text.stroke-19"),sQuery(id+"F2.wireOp",EDGE,"E13.sketch_text.stroke-20"),sQuery(id+"F2.wireOp",EDGE,"E13.sketch_text.stroke-21"),sQuery(id+"F2.wireOp",EDGE,"E13.sketch_text.stroke-22"),sQuery(id+"F2.wireOp",EDGE,"E13.sketch_text.stroke-23"),sQuery(id+"F2.wireOp",EDGE,"E13.sketch_text.stroke-24"),sQuery(id+"F2.wireOp",EDGE,"E13.sketch_text.stroke-25"),sQuery(id+"F2.wireOp",EDGE,"E13.sketch_text.stroke-26"),sQuery(id+"F2.wireOp",EDGE,"E13.sketch_text.stroke-27"),sQuery(id+"F2.wireOp",EDGE,"E13.sketch_text.stroke-28")])]});
            var Q175;
            Q175=makeQuery(id+"F4.opExtrude","SWEPT_BODY",BODY,{"disambiguationData":[OSD([sQuery(id+"F2.wireOp",EDGE,"E13.sketch_text.stroke-29"),sQuery(id+"F2.wireOp",EDGE,"E13.sketch_text.stroke-30"),sQuery(id+"F2.wireOp",EDGE,"E13.sketch_text.stroke-31"),sQuery(id+"F2.wireOp",EDGE,"E13.sketch_text.stroke-32")])]});
            var Q176;
            Q176=makeQuery(id+"F4.opExtrude","SWEPT_BODY",BODY,{"disambiguationData":[OSD([sQuery(id+"F2.wireOp",EDGE,"E13.sketch_text.stroke-33"),sQuery(id+"F2.wireOp",EDGE,"E13.sketch_text.stroke-34"),sQuery(id+"F2.wireOp",EDGE,"E13.sketch_text.stroke-35"),sQuery(id+"F2.wireOp",EDGE,"E13.sketch_text.stroke-36")])]});
            var Q177;
            Q177=makeQuery(id+"F4.opExtrude","SWEPT_BODY",BODY,{"disambiguationData":[OSD([sQuery(id+"F2.wireOp",EDGE,"E13.sketch_text.stroke-37"),sQuery(id+"F2.wireOp",EDGE,"E13.sketch_text.stroke-38"),sQuery(id+"F2.wireOp",EDGE,"E13.sketch_text.stroke-39"),sQuery(id+"F2.wireOp",EDGE,"E13.sketch_text.stroke-40"),sQuery(id+"F2.wireOp",EDGE,"E13.sketch_text.stroke-41"),sQuery(id+"F2.wireOp",EDGE,"E13.sketch_text.stroke-42"),sQuery(id+"F2.wireOp",EDGE,"E13.sketch_text.stroke-43"),sQuery(id+"F2.wireOp",EDGE,"E13.sketch_text.stroke-44"),sQuery(id+"F2.wireOp",EDGE,"E13.sketch_text.stroke-45"),sQuery(id+"F2.wireOp",EDGE,"E13.sketch_text.stroke-46"),sQuery(id+"F2.wireOp",EDGE,"E13.sketch_text.stroke-47"),sQuery(id+"F2.wireOp",EDGE,"E13.sketch_text.stroke-48"),sQuery(id+"F2.wireOp",EDGE,"E13.sketch_text.stroke-49"),sQuery(id+"F2.wireOp",EDGE,"E13.sketch_text.stroke-50"),sQuery(id+"F2.wireOp",EDGE,"E13.sketch_text.stroke-51")])]});
            var Q178;
            Q178=makeQuery(id+"F4.opExtrude","SWEPT_BODY",BODY,{"disambiguationData":[OSD([sQuery(id+"F2.wireOp",EDGE,"E13.sketch_text.stroke-52"),sQuery(id+"F2.wireOp",EDGE,"E13.sketch_text.stroke-53"),sQuery(id+"F2.wireOp",EDGE,"E13.sketch_text.stroke-54"),sQuery(id+"F2.wireOp",EDGE,"E13.sketch_text.stroke-55"),sQuery(id+"F2.wireOp",EDGE,"E13.sketch_text.stroke-56"),sQuery(id+"F2.wireOp",EDGE,"E13.sketch_text.stroke-57"),sQuery(id+"F2.wireOp",EDGE,"E13.sketch_text.stroke-58"),sQuery(id+"F2.wireOp",EDGE,"E13.sketch_text.stroke-59"),sQuery(id+"F2.wireOp",EDGE,"E13.sketch_text.stroke-60"),sQuery(id+"F2.wireOp",EDGE,"E13.sketch_text.stroke-61"),sQuery(id+"F2.wireOp",EDGE,"E13.sketch_text.stroke-62"),sQuery(id+"F2.wireOp",EDGE,"E13.sketch_text.stroke-63"),sQuery(id+"F2.wireOp",EDGE,"E13.sketch_text.stroke-64"),sQuery(id+"F2.wireOp",EDGE,"E13.sketch_text.stroke-65"),sQuery(id+"F2.wireOp",EDGE,"E13.sketch_text.stroke-66"),sQuery(id+"F2.wireOp",EDGE,"E13.sketch_text.stroke-67"),sQuery(id+"F2.wireOp",EDGE,"E13.sketch_text.stroke-68")])]});
            var Q179;
            Q179=makeQuery(id+"F4.opExtrude","SWEPT_BODY",BODY,{"disambiguationData":[OSD([sQuery(id+"F2.wireOp",EDGE,"E13.sketch_text.stroke-69"),sQuery(id+"F2.wireOp",EDGE,"E13.sketch_text.stroke-70"),sQuery(id+"F2.wireOp",EDGE,"E13.sketch_text.stroke-71"),sQuery(id+"F2.wireOp",EDGE,"E13.sketch_text.stroke-72"),sQuery(id+"F2.wireOp",EDGE,"E13.sketch_text.stroke-73"),sQuery(id+"F2.wireOp",EDGE,"E13.sketch_text.stroke-74"),sQuery(id+"F2.wireOp",EDGE,"E13.sketch_text.stroke-75"),sQuery(id+"F2.wireOp",EDGE,"E13.sketch_text.stroke-76")])]});
            var Q180;
            Q180=makeQuery(id+"F4.opExtrude","SWEPT_BODY",BODY,{"disambiguationData":[OSD([sQuery(id+"F2.wireOp",EDGE,"E13.sketch_text.stroke-77"),sQuery(id+"F2.wireOp",EDGE,"E13.sketch_text.stroke-78"),sQuery(id+"F2.wireOp",EDGE,"E13.sketch_text.stroke-79"),sQuery(id+"F2.wireOp",EDGE,"E13.sketch_text.stroke-80"),sQuery(id+"F2.wireOp",EDGE,"E13.sketch_text.stroke-81"),sQuery(id+"F2.wireOp",EDGE,"E13.sketch_text.stroke-82"),sQuery(id+"F2.wireOp",EDGE,"E13.sketch_text.stroke-83"),sQuery(id+"F2.wireOp",EDGE,"E13.sketch_text.stroke-84"),sQuery(id+"F2.wireOp",EDGE,"E13.sketch_text.stroke-85"),sQuery(id+"F2.wireOp",EDGE,"E13.sketch_text.stroke-86"),sQuery(id+"F2.wireOp",EDGE,"E13.sketch_text.stroke-87"),sQuery(id+"F2.wireOp",EDGE,"E13.sketch_text.stroke-88"),sQuery(id+"F2.wireOp",EDGE,"E13.sketch_text.stroke-89"),sQuery(id+"F2.wireOp",EDGE,"E13.sketch_text.stroke-90"),sQuery(id+"F2.wireOp",EDGE,"E13.sketch_text.stroke-91"),sQuery(id+"F2.wireOp",EDGE,"E13.sketch_text.stroke-92"),sQuery(id+"F2.wireOp",EDGE,"E13.sketch_text.stroke-93")])]});
            var Q181;
            Q181=makeQuery(id+"F4.opExtrude","SWEPT_BODY",BODY,{"disambiguationData":[OSD([sQuery(id+"F2.wireOp",EDGE,"E13.sketch_text.stroke-94"),sQuery(id+"F2.wireOp",EDGE,"E13.sketch_text.stroke-95"),sQuery(id+"F2.wireOp",EDGE,"E13.sketch_text.stroke-96"),sQuery(id+"F2.wireOp",EDGE,"E13.sketch_text.stroke-97"),sQuery(id+"F2.wireOp",EDGE,"E13.sketch_text.stroke-98"),sQuery(id+"F2.wireOp",EDGE,"E13.sketch_text.stroke-99"),sQuery(id+"F2.wireOp",EDGE,"E13.sketch_text.stroke-100"),sQuery(id+"F2.wireOp",EDGE,"E13.sketch_text.stroke-101"),sQuery(id+"F2.wireOp",EDGE,"E13.sketch_text.stroke-102"),sQuery(id+"F2.wireOp",EDGE,"E13.sketch_text.stroke-103"),sQuery(id+"F2.wireOp",EDGE,"E13.sketch_text.stroke-104"),sQuery(id+"F2.wireOp",EDGE,"E13.sketch_text.stroke-105"),sQuery(id+"F2.wireOp",EDGE,"E13.sketch_text.stroke-106"),sQuery(id+"F2.wireOp",EDGE,"E13.sketch_text.stroke-107"),sQuery(id+"F2.wireOp",EDGE,"E13.sketch_text.stroke-108"),sQuery(id+"F2.wireOp",EDGE,"E13.sketch_text.stroke-109")])]});
            var Q182;
            Q182=makeQuery(id+"F4.opExtrude","SWEPT_BODY",BODY,{"disambiguationData":[OSD([sQuery(id+"F2.wireOp",EDGE,"E13.sketch_text.stroke-110"),sQuery(id+"F2.wireOp",EDGE,"E13.sketch_text.stroke-111"),sQuery(id+"F2.wireOp",EDGE,"E13.sketch_text.stroke-112"),sQuery(id+"F2.wireOp",EDGE,"E13.sketch_text.stroke-113")])]});
            var Q183;
            Q183=makeQuery(id+"F4.opExtrude","SWEPT_BODY",BODY,{"disambiguationData":[OSD([sQuery(id+"F2.wireOp",EDGE,"E13.sketch_text.stroke-114"),sQuery(id+"F2.wireOp",EDGE,"E13.sketch_text.stroke-115"),sQuery(id+"F2.wireOp",EDGE,"E13.sketch_text.stroke-116"),sQuery(id+"F2.wireOp",EDGE,"E13.sketch_text.stroke-117"),sQuery(id+"F2.wireOp",EDGE,"E13.sketch_text.stroke-118"),sQuery(id+"F2.wireOp",EDGE,"E13.sketch_text.stroke-119"),sQuery(id+"F2.wireOp",EDGE,"E13.sketch_text.stroke-120"),sQuery(id+"F2.wireOp",EDGE,"E13.sketch_text.stroke-121"),sQuery(id+"F2.wireOp",EDGE,"E13.sketch_text.stroke-122"),sQuery(id+"F2.wireOp",EDGE,"E13.sketch_text.stroke-123"),sQuery(id+"F2.wireOp",EDGE,"E13.sketch_text.stroke-124"),sQuery(id+"F2.wireOp",EDGE,"E13.sketch_text.stroke-125"),sQuery(id+"F2.wireOp",EDGE,"E13.sketch_text.stroke-126"),sQuery(id+"F2.wireOp",EDGE,"E13.sketch_text.stroke-127"),sQuery(id+"F2.wireOp",EDGE,"E13.sketch_text.stroke-128"),sQuery(id+"F2.wireOp",EDGE,"E13.sketch_text.stroke-129"),sQuery(id+"F2.wireOp",EDGE,"E13.sketch_text.stroke-130"),sQuery(id+"F2.wireOp",EDGE,"E13.sketch_text.stroke-131"),sQuery(id+"F2.wireOp",EDGE,"E13.sketch_text.stroke-132"),sQuery(id+"F2.wireOp",EDGE,"E13.sketch_text.stroke-133"),sQuery(id+"F2.wireOp",EDGE,"E13.sketch_text.stroke-134"),sQuery(id+"F2.wireOp",EDGE,"E13.sketch_text.stroke-135"),sQuery(id+"F2.wireOp",EDGE,"E13.sketch_text.stroke-136"),sQuery(id+"F2.wireOp",EDGE,"E13.sketch_text.stroke-137"),sQuery(id+"F2.wireOp",EDGE,"E13.sketch_text.stroke-138")])]});
            var Q184;
            Q184=makeQuery(id+"F4.opExtrude","SWEPT_BODY",BODY,{"disambiguationData":[OSD([sQuery(id+"F2.wireOp",EDGE,"E13.sketch_text.stroke-139"),sQuery(id+"F2.wireOp",EDGE,"E13.sketch_text.stroke-140"),sQuery(id+"F2.wireOp",EDGE,"E13.sketch_text.stroke-141"),sQuery(id+"F2.wireOp",EDGE,"E13.sketch_text.stroke-142"),sQuery(id+"F2.wireOp",EDGE,"E13.sketch_text.stroke-143"),sQuery(id+"F2.wireOp",EDGE,"E13.sketch_text.stroke-144"),sQuery(id+"F2.wireOp",EDGE,"E13.sketch_text.stroke-145"),sQuery(id+"F2.wireOp",EDGE,"E13.sketch_text.stroke-146"),sQuery(id+"F2.wireOp",EDGE,"E13.sketch_text.stroke-147"),sQuery(id+"F2.wireOp",EDGE,"E13.sketch_text.stroke-148"),sQuery(id+"F2.wireOp",EDGE,"E13.sketch_text.stroke-149"),sQuery(id+"F2.wireOp",EDGE,"E13.sketch_text.stroke-150"),sQuery(id+"F2.wireOp",EDGE,"E13.sketch_text.stroke-151"),sQuery(id+"F2.wireOp",EDGE,"E13.sketch_text.stroke-152"),sQuery(id+"F2.wireOp",EDGE,"E13.sketch_text.stroke-153"),sQuery(id+"F2.wireOp",EDGE,"E13.sketch_text.stroke-154"),sQuery(id+"F2.wireOp",EDGE,"E13.sketch_text.stroke-155"),sQuery(id+"F2.wireOp",EDGE,"E13.sketch_text.stroke-156"),sQuery(id+"F2.wireOp",EDGE,"E13.sketch_text.stroke-157"),sQuery(id+"F2.wireOp",EDGE,"E13.sketch_text.stroke-158"),sQuery(id+"F2.wireOp",EDGE,"E13.sketch_text.stroke-159"),sQuery(id+"F2.wireOp",EDGE,"E13.sketch_text.stroke-160"),sQuery(id+"F2.wireOp",EDGE,"E13.sketch_text.stroke-161"),sQuery(id+"F2.wireOp",EDGE,"E13.sketch_text.stroke-162"),sQuery(id+"F2.wireOp",EDGE,"E13.sketch_text.stroke-163")])]});
            var Q185;
            Q185=makeQuery(id+"F4.opExtrude","SWEPT_BODY",BODY,{"disambiguationData":[OSD([sQuery(id+"F2.wireOp",EDGE,"E13.sketch_text.stroke-164"),sQuery(id+"F2.wireOp",EDGE,"E13.sketch_text.stroke-165"),sQuery(id+"F2.wireOp",EDGE,"E13.sketch_text.stroke-166"),sQuery(id+"F2.wireOp",EDGE,"E13.sketch_text.stroke-167"),sQuery(id+"F2.wireOp",EDGE,"E13.sketch_text.stroke-168"),sQuery(id+"F2.wireOp",EDGE,"E13.sketch_text.stroke-169"),sQuery(id+"F2.wireOp",EDGE,"E13.sketch_text.stroke-170"),sQuery(id+"F2.wireOp",EDGE,"E13.sketch_text.stroke-171"),sQuery(id+"F2.wireOp",EDGE,"E13.sketch_text.stroke-172"),sQuery(id+"F2.wireOp",EDGE,"E13.sketch_text.stroke-173"),sQuery(id+"F2.wireOp",EDGE,"E13.sketch_text.stroke-174"),sQuery(id+"F2.wireOp",EDGE,"E13.sketch_text.stroke-175"),sQuery(id+"F2.wireOp",EDGE,"E13.sketch_text.stroke-176"),sQuery(id+"F2.wireOp",EDGE,"E13.sketch_text.stroke-177"),sQuery(id+"F2.wireOp",EDGE,"E13.sketch_text.stroke-178"),sQuery(id+"F2.wireOp",EDGE,"E13.sketch_text.stroke-179"),sQuery(id+"F2.wireOp",EDGE,"E13.sketch_text.stroke-180"),sQuery(id+"F2.wireOp",EDGE,"E13.sketch_text.stroke-181")])]});
            var Q186;
            Q186=makeQuery(id+"F4.opExtrude","SWEPT_BODY",BODY,{"disambiguationData":[OSD([sQuery(id+"F2.wireOp",EDGE,"E13.sketch_text.stroke-182"),sQuery(id+"F2.wireOp",EDGE,"E13.sketch_text.stroke-183"),sQuery(id+"F2.wireOp",EDGE,"E13.sketch_text.stroke-184"),sQuery(id+"F2.wireOp",EDGE,"E13.sketch_text.stroke-185"),sQuery(id+"F2.wireOp",EDGE,"E13.sketch_text.stroke-186"),sQuery(id+"F2.wireOp",EDGE,"E13.sketch_text.stroke-187"),sQuery(id+"F2.wireOp",EDGE,"E13.sketch_text.stroke-188"),sQuery(id+"F2.wireOp",EDGE,"E13.sketch_text.stroke-189"),sQuery(id+"F2.wireOp",EDGE,"E13.sketch_text.stroke-190"),sQuery(id+"F2.wireOp",EDGE,"E13.sketch_text.stroke-191"),sQuery(id+"F2.wireOp",EDGE,"E13.sketch_text.stroke-192"),sQuery(id+"F2.wireOp",EDGE,"E13.sketch_text.stroke-193"),sQuery(id+"F2.wireOp",EDGE,"E13.sketch_text.stroke-194"),sQuery(id+"F2.wireOp",EDGE,"E13.sketch_text.stroke-195"),sQuery(id+"F2.wireOp",EDGE,"E13.sketch_text.stroke-196"),sQuery(id+"F2.wireOp",EDGE,"E13.sketch_text.stroke-197"),sQuery(id+"F2.wireOp",EDGE,"E13.sketch_text.stroke-198"),sQuery(id+"F2.wireOp",EDGE,"E13.sketch_text.stroke-199"),sQuery(id+"F2.wireOp",EDGE,"E13.sketch_text.stroke-200"),sQuery(id+"F2.wireOp",EDGE,"E13.sketch_text.stroke-201"),sQuery(id+"F2.wireOp",EDGE,"E13.sketch_text.stroke-202"),sQuery(id+"F2.wireOp",EDGE,"E13.sketch_text.stroke-203"),sQuery(id+"F2.wireOp",EDGE,"E13.sketch_text.stroke-204"),sQuery(id+"F2.wireOp",EDGE,"E13.sketch_text.stroke-205"),sQuery(id+"F2.wireOp",EDGE,"E13.sketch_text.stroke-206")])]});
            var Q187;
            Q187=makeQuery(id+"F4.opExtrude","SWEPT_BODY",BODY,{"disambiguationData":[OSD([sQuery(id+"F2.wireOp",EDGE,"E13.sketch_text.stroke-207"),sQuery(id+"F2.wireOp",EDGE,"E13.sketch_text.stroke-208"),sQuery(id+"F2.wireOp",EDGE,"E13.sketch_text.stroke-209"),sQuery(id+"F2.wireOp",EDGE,"E13.sketch_text.stroke-210"),sQuery(id+"F2.wireOp",EDGE,"E13.sketch_text.stroke-211"),sQuery(id+"F2.wireOp",EDGE,"E13.sketch_text.stroke-212"),sQuery(id+"F2.wireOp",EDGE,"E13.sketch_text.stroke-213"),sQuery(id+"F2.wireOp",EDGE,"E13.sketch_text.stroke-214"),sQuery(id+"F2.wireOp",EDGE,"E13.sketch_text.stroke-215"),sQuery(id+"F2.wireOp",EDGE,"E13.sketch_text.stroke-216"),sQuery(id+"F2.wireOp",EDGE,"E13.sketch_text.stroke-217"),sQuery(id+"F2.wireOp",EDGE,"E13.sketch_text.stroke-218"),sQuery(id+"F2.wireOp",EDGE,"E13.sketch_text.stroke-219"),sQuery(id+"F2.wireOp",EDGE,"E13.sketch_text.stroke-220"),sQuery(id+"F2.wireOp",EDGE,"E13.sketch_text.stroke-221"),sQuery(id+"F2.wireOp",EDGE,"E13.sketch_text.stroke-222"),sQuery(id+"F2.wireOp",EDGE,"E13.sketch_text.stroke-223"),sQuery(id+"F2.wireOp",EDGE,"E13.sketch_text.stroke-224"),sQuery(id+"F2.wireOp",EDGE,"E13.sketch_text.stroke-225"),sQuery(id+"F2.wireOp",EDGE,"E13.sketch_text.stroke-226"),sQuery(id+"F2.wireOp",EDGE,"E13.sketch_text.stroke-227"),sQuery(id+"F2.wireOp",EDGE,"E13.sketch_text.stroke-228"),sQuery(id+"F2.wireOp",EDGE,"E13.sketch_text.stroke-229"),sQuery(id+"F2.wireOp",EDGE,"E13.sketch_text.stroke-230"),sQuery(id+"F2.wireOp",EDGE,"E13.sketch_text.stroke-231")])]});
            var Q188;
            Q188=makeQuery(id+"F4.opExtrude","SWEPT_BODY",BODY,{"disambiguationData":[OSD([sQuery(id+"F2.wireOp",EDGE,"E13.sketch_text.stroke-232"),sQuery(id+"F2.wireOp",EDGE,"E13.sketch_text.stroke-233"),sQuery(id+"F2.wireOp",EDGE,"E13.sketch_text.stroke-234"),sQuery(id+"F2.wireOp",EDGE,"E13.sketch_text.stroke-235"),sQuery(id+"F2.wireOp",EDGE,"E13.sketch_text.stroke-236"),sQuery(id+"F2.wireOp",EDGE,"E13.sketch_text.stroke-237"),sQuery(id+"F2.wireOp",EDGE,"E13.sketch_text.stroke-238")])]});
            var Q189;
            Q189=makeQuery(id+"F4.opExtrude","SWEPT_BODY",BODY,{"disambiguationData":[OSD([sQuery(id+"F2.wireOp",EDGE,"E13.sketch_text.stroke-239"),sQuery(id+"F2.wireOp",EDGE,"E13.sketch_text.stroke-240"),sQuery(id+"F2.wireOp",EDGE,"E13.sketch_text.stroke-241"),sQuery(id+"F2.wireOp",EDGE,"E13.sketch_text.stroke-242"),sQuery(id+"F2.wireOp",EDGE,"E13.sketch_text.stroke-243"),sQuery(id+"F2.wireOp",EDGE,"E13.sketch_text.stroke-244"),sQuery(id+"F2.wireOp",EDGE,"E13.sketch_text.stroke-245")])]});
            var Q190;
            Q190=makeQuery(id+"F4.opExtrude","SWEPT_BODY",BODY,{"disambiguationData":[OSD([sQuery(id+"F2.wireOp",EDGE,"E5.sketch_text.stroke-14"),sQuery(id+"F2.wireOp",EDGE,"E5.sketch_text.stroke-15"),sQuery(id+"F2.wireOp",EDGE,"E5.sketch_text.stroke-16"),sQuery(id+"F2.wireOp",EDGE,"E5.sketch_text.stroke-17"),sQuery(id+"F2.wireOp",EDGE,"E5.sketch_text.stroke-18"),sQuery(id+"F2.wireOp",EDGE,"E5.sketch_text.stroke-19"),sQuery(id+"F2.wireOp",EDGE,"E5.sketch_text.stroke-20"),sQuery(id+"F2.wireOp",EDGE,"E5.sketch_text.stroke-21"),sQuery(id+"F2.wireOp",EDGE,"E5.sketch_text.stroke-22"),sQuery(id+"F2.wireOp",EDGE,"E5.sketch_text.stroke-23"),sQuery(id+"F2.wireOp",EDGE,"E5.sketch_text.stroke-24"),sQuery(id+"F2.wireOp",EDGE,"E5.sketch_text.stroke-25"),sQuery(id+"F2.wireOp",EDGE,"E5.sketch_text.stroke-26"),sQuery(id+"F2.wireOp",EDGE,"E5.sketch_text.stroke-27"),sQuery(id+"F2.wireOp",EDGE,"E5.sketch_text.stroke-28"),sQuery(id+"F2.wireOp",EDGE,"E5.sketch_text.stroke-29"),sQuery(id+"F2.wireOp",EDGE,"E5.sketch_text.stroke-30"),sQuery(id+"F2.wireOp",EDGE,"E5.sketch_text.stroke-31")])]});
            var Q191;
            Q191=makeQuery(id+"F4.opExtrude","SWEPT_BODY",BODY,{"disambiguationData":[OSD([sQuery(id+"F2.wireOp",EDGE,"E5.sketch_text.stroke-32"),sQuery(id+"F2.wireOp",EDGE,"E5.sketch_text.stroke-33"),sQuery(id+"F2.wireOp",EDGE,"E5.sketch_text.stroke-34"),sQuery(id+"F2.wireOp",EDGE,"E5.sketch_text.stroke-35")])]});
            var Q192;
            Q192=makeQuery(id+"F4.opExtrude","SWEPT_BODY",BODY,{"disambiguationData":[OSD([sQuery(id+"F2.wireOp",EDGE,"E5.sketch_text.stroke-36"),sQuery(id+"F2.wireOp",EDGE,"E5.sketch_text.stroke-37"),sQuery(id+"F2.wireOp",EDGE,"E5.sketch_text.stroke-38"),sQuery(id+"F2.wireOp",EDGE,"E5.sketch_text.stroke-39"),sQuery(id+"F2.wireOp",EDGE,"E5.sketch_text.stroke-40"),sQuery(id+"F2.wireOp",EDGE,"E5.sketch_text.stroke-41"),sQuery(id+"F2.wireOp",EDGE,"E5.sketch_text.stroke-42"),sQuery(id+"F2.wireOp",EDGE,"E5.sketch_text.stroke-43"),sQuery(id+"F2.wireOp",EDGE,"E5.sketch_text.stroke-44"),sQuery(id+"F2.wireOp",EDGE,"E5.sketch_text.stroke-45")])]});
            var Q193;
            Q193=makeQuery(id+"F4.opExtrude","SWEPT_BODY",BODY,{"disambiguationData":[OSD([sQuery(id+"F2.wireOp",EDGE,"E5.sketch_text.stroke-46"),sQuery(id+"F2.wireOp",EDGE,"E5.sketch_text.stroke-47"),sQuery(id+"F2.wireOp",EDGE,"E5.sketch_text.stroke-48"),sQuery(id+"F2.wireOp",EDGE,"E5.sketch_text.stroke-49"),sQuery(id+"F2.wireOp",EDGE,"E5.sketch_text.stroke-50"),sQuery(id+"F2.wireOp",EDGE,"E5.sketch_text.stroke-51"),sQuery(id+"F2.wireOp",EDGE,"E5.sketch_text.stroke-52"),sQuery(id+"F2.wireOp",EDGE,"E5.sketch_text.stroke-53")])]});
            var Q194;
            Q194=makeQuery(id+"F4.opExtrude","SWEPT_BODY",BODY,{"disambiguationData":[OSD([sQuery(id+"F2.wireOp",EDGE,"E5.sketch_text.stroke-54"),sQuery(id+"F2.wireOp",EDGE,"E5.sketch_text.stroke-55"),sQuery(id+"F2.wireOp",EDGE,"E5.sketch_text.stroke-56"),sQuery(id+"F2.wireOp",EDGE,"E5.sketch_text.stroke-57"),sQuery(id+"F2.wireOp",EDGE,"E5.sketch_text.stroke-58"),sQuery(id+"F2.wireOp",EDGE,"E5.sketch_text.stroke-59"),sQuery(id+"F2.wireOp",EDGE,"E5.sketch_text.stroke-60"),sQuery(id+"F2.wireOp",EDGE,"E5.sketch_text.stroke-61"),sQuery(id+"F2.wireOp",EDGE,"E5.sketch_text.stroke-62"),sQuery(id+"F2.wireOp",EDGE,"E5.sketch_text.stroke-63"),sQuery(id+"F2.wireOp",EDGE,"E5.sketch_text.stroke-64"),sQuery(id+"F2.wireOp",EDGE,"E5.sketch_text.stroke-65")])]});
            var Q195;
            Q195=makeQuery(id+"F4.opExtrude","SWEPT_BODY",BODY,{"disambiguationData":[OSD([sQuery(id+"F2.wireOp",EDGE,"E5.sketch_text.stroke-66"),sQuery(id+"F2.wireOp",EDGE,"E5.sketch_text.stroke-67"),sQuery(id+"F2.wireOp",EDGE,"E5.sketch_text.stroke-68"),sQuery(id+"F2.wireOp",EDGE,"E5.sketch_text.stroke-69"),sQuery(id+"F2.wireOp",EDGE,"E5.sketch_text.stroke-70"),sQuery(id+"F2.wireOp",EDGE,"E5.sketch_text.stroke-71"),sQuery(id+"F2.wireOp",EDGE,"E5.sketch_text.stroke-72"),sQuery(id+"F2.wireOp",EDGE,"E5.sketch_text.stroke-73"),sQuery(id+"F2.wireOp",EDGE,"E5.sketch_text.stroke-74"),sQuery(id+"F2.wireOp",EDGE,"E5.sketch_text.stroke-75"),sQuery(id+"F2.wireOp",EDGE,"E5.sketch_text.stroke-76"),sQuery(id+"F2.wireOp",EDGE,"E5.sketch_text.stroke-77"),sQuery(id+"F2.wireOp",EDGE,"E5.sketch_text.stroke-78"),sQuery(id+"F2.wireOp",EDGE,"E5.sketch_text.stroke-79"),sQuery(id+"F2.wireOp",EDGE,"E5.sketch_text.stroke-80"),sQuery(id+"F2.wireOp",EDGE,"E5.sketch_text.stroke-81"),sQuery(id+"F2.wireOp",EDGE,"E5.sketch_text.stroke-82"),sQuery(id+"F2.wireOp",EDGE,"E5.sketch_text.stroke-83")])]});
            var Q196;
            Q196=makeQuery(id+"F4.opExtrude","SWEPT_BODY",BODY,{"disambiguationData":[OSD([sQuery(id+"F2.wireOp",EDGE,"E5.sketch_text.stroke-84"),sQuery(id+"F2.wireOp",EDGE,"E5.sketch_text.stroke-85"),sQuery(id+"F2.wireOp",EDGE,"E5.sketch_text.stroke-86"),sQuery(id+"F2.wireOp",EDGE,"E5.sketch_text.stroke-87")])]});
            var Q197;
            Q197=makeQuery(id+"F4.opExtrude","SWEPT_BODY",BODY,{"disambiguationData":[OSD([sQuery(id+"F2.wireOp",EDGE,"E5.sketch_text.stroke-88"),sQuery(id+"F2.wireOp",EDGE,"E5.sketch_text.stroke-89"),sQuery(id+"F2.wireOp",EDGE,"E5.sketch_text.stroke-90"),sQuery(id+"F2.wireOp",EDGE,"E5.sketch_text.stroke-91")])]});
            var Q198;
            Q198=makeQuery(id+"F4.opExtrude","SWEPT_BODY",BODY,{"disambiguationData":[OSD([sQuery(id+"F2.wireOp",EDGE,"E7.sketch_text.stroke-0"),sQuery(id+"F2.wireOp",EDGE,"E7.sketch_text.stroke-1"),sQuery(id+"F2.wireOp",EDGE,"E7.sketch_text.stroke-2"),sQuery(id+"F2.wireOp",EDGE,"E7.sketch_text.stroke-3"),sQuery(id+"F2.wireOp",EDGE,"E7.sketch_text.stroke-4"),sQuery(id+"F2.wireOp",EDGE,"E7.sketch_text.stroke-5"),sQuery(id+"F2.wireOp",EDGE,"E7.sketch_text.stroke-6"),sQuery(id+"F2.wireOp",EDGE,"E7.sketch_text.stroke-7"),sQuery(id+"F2.wireOp",EDGE,"E7.sketch_text.stroke-8"),sQuery(id+"F2.wireOp",EDGE,"E7.sketch_text.stroke-9"),sQuery(id+"F2.wireOp",EDGE,"E7.sketch_text.stroke-10"),sQuery(id+"F2.wireOp",EDGE,"E7.sketch_text.stroke-11"),sQuery(id+"F2.wireOp",EDGE,"E7.sketch_text.stroke-12"),sQuery(id+"F2.wireOp",EDGE,"E7.sketch_text.stroke-13"),sQuery(id+"F2.wireOp",EDGE,"E7.sketch_text.stroke-14"),sQuery(id+"F2.wireOp",EDGE,"E7.sketch_text.stroke-15"),sQuery(id+"F2.wireOp",EDGE,"E7.sketch_text.stroke-16"),sQuery(id+"F2.wireOp",EDGE,"E7.sketch_text.stroke-17")])]});
            var Q199;
            Q199=makeQuery(id+"F4.opExtrude","SWEPT_BODY",BODY,{"disambiguationData":[OSD([sQuery(id+"F2.wireOp",EDGE,"E7.sketch_text.stroke-18"),sQuery(id+"F2.wireOp",EDGE,"E7.sketch_text.stroke-19"),sQuery(id+"F2.wireOp",EDGE,"E7.sketch_text.stroke-20"),sQuery(id+"F2.wireOp",EDGE,"E7.sketch_text.stroke-21"),sQuery(id+"F2.wireOp",EDGE,"E7.sketch_text.stroke-22"),sQuery(id+"F2.wireOp",EDGE,"E7.sketch_text.stroke-23"),sQuery(id+"F2.wireOp",EDGE,"E7.sketch_text.stroke-24"),sQuery(id+"F2.wireOp",EDGE,"E7.sketch_text.stroke-25"),sQuery(id+"F2.wireOp",EDGE,"E7.sketch_text.stroke-26"),sQuery(id+"F2.wireOp",EDGE,"E7.sketch_text.stroke-27"),sQuery(id+"F2.wireOp",EDGE,"E7.sketch_text.stroke-28"),sQuery(id+"F2.wireOp",EDGE,"E7.sketch_text.stroke-29"),sQuery(id+"F2.wireOp",EDGE,"E7.sketch_text.stroke-30"),sQuery(id+"F2.wireOp",EDGE,"E7.sketch_text.stroke-31"),sQuery(id+"F2.wireOp",EDGE,"E7.sketch_text.stroke-32"),sQuery(id+"F2.wireOp",EDGE,"E7.sketch_text.stroke-33"),sQuery(id+"F2.wireOp",EDGE,"E7.sketch_text.stroke-34")])]});
            var Q200;
            Q200=makeQuery(id+"F4.opExtrude","SWEPT_BODY",BODY,{"disambiguationData":[OSD([sQuery(id+"F2.wireOp",EDGE,"E7.sketch_text.stroke-35"),sQuery(id+"F2.wireOp",EDGE,"E7.sketch_text.stroke-36"),sQuery(id+"F2.wireOp",EDGE,"E7.sketch_text.stroke-37"),sQuery(id+"F2.wireOp",EDGE,"E7.sketch_text.stroke-38"),sQuery(id+"F2.wireOp",EDGE,"E7.sketch_text.stroke-39"),sQuery(id+"F2.wireOp",EDGE,"E7.sketch_text.stroke-40"),sQuery(id+"F2.wireOp",EDGE,"E7.sketch_text.stroke-41"),sQuery(id+"F2.wireOp",EDGE,"E7.sketch_text.stroke-42"),sQuery(id+"F2.wireOp",EDGE,"E7.sketch_text.stroke-43"),sQuery(id+"F2.wireOp",EDGE,"E7.sketch_text.stroke-44"),sQuery(id+"F2.wireOp",EDGE,"E7.sketch_text.stroke-45"),sQuery(id+"F2.wireOp",EDGE,"E7.sketch_text.stroke-46"),sQuery(id+"F2.wireOp",EDGE,"E7.sketch_text.stroke-47"),sQuery(id+"F2.wireOp",EDGE,"E7.sketch_text.stroke-48"),sQuery(id+"F2.wireOp",EDGE,"E7.sketch_text.stroke-49"),sQuery(id+"F2.wireOp",EDGE,"E7.sketch_text.stroke-50"),sQuery(id+"F2.wireOp",EDGE,"E7.sketch_text.stroke-51"),sQuery(id+"F2.wireOp",EDGE,"E7.sketch_text.stroke-52"),sQuery(id+"F2.wireOp",EDGE,"E7.sketch_text.stroke-53"),sQuery(id+"F2.wireOp",EDGE,"E7.sketch_text.stroke-54"),sQuery(id+"F2.wireOp",EDGE,"E7.sketch_text.stroke-55"),sQuery(id+"F2.wireOp",EDGE,"E7.sketch_text.stroke-56"),sQuery(id+"F2.wireOp",EDGE,"E7.sketch_text.stroke-57"),sQuery(id+"F2.wireOp",EDGE,"E7.sketch_text.stroke-58"),sQuery(id+"F2.wireOp",EDGE,"E7.sketch_text.stroke-59")])]});
            var Q201;
            Q201=makeQuery(id+"F4.opExtrude","SWEPT_BODY",BODY,{"disambiguationData":[OSD([sQuery(id+"F2.wireOp",EDGE,"E7.sketch_text.stroke-60"),sQuery(id+"F2.wireOp",EDGE,"E7.sketch_text.stroke-61"),sQuery(id+"F2.wireOp",EDGE,"E7.sketch_text.stroke-62"),sQuery(id+"F2.wireOp",EDGE,"E7.sketch_text.stroke-63"),sQuery(id+"F2.wireOp",EDGE,"E7.sketch_text.stroke-64"),sQuery(id+"F2.wireOp",EDGE,"E7.sketch_text.stroke-65"),sQuery(id+"F2.wireOp",EDGE,"E7.sketch_text.stroke-66"),sQuery(id+"F2.wireOp",EDGE,"E7.sketch_text.stroke-67"),sQuery(id+"F2.wireOp",EDGE,"E7.sketch_text.stroke-68"),sQuery(id+"F2.wireOp",EDGE,"E7.sketch_text.stroke-69"),sQuery(id+"F2.wireOp",EDGE,"E7.sketch_text.stroke-70"),sQuery(id+"F2.wireOp",EDGE,"E7.sketch_text.stroke-71"),sQuery(id+"F2.wireOp",EDGE,"E7.sketch_text.stroke-72"),sQuery(id+"F2.wireOp",EDGE,"E7.sketch_text.stroke-73"),sQuery(id+"F2.wireOp",EDGE,"E7.sketch_text.stroke-74"),sQuery(id+"F2.wireOp",EDGE,"E7.sketch_text.stroke-75"),sQuery(id+"F2.wireOp",EDGE,"E7.sketch_text.stroke-76"),sQuery(id+"F2.wireOp",EDGE,"E7.sketch_text.stroke-77"),sQuery(id+"F2.wireOp",EDGE,"E7.sketch_text.stroke-78")])]});
            var Q202;
            Q202=makeQuery(id+"F4.opExtrude","SWEPT_BODY",BODY,{"disambiguationData":[OSD([sQuery(id+"F2.wireOp",EDGE,"E7.sketch_text.stroke-79"),sQuery(id+"F2.wireOp",EDGE,"E7.sketch_text.stroke-80"),sQuery(id+"F2.wireOp",EDGE,"E7.sketch_text.stroke-81"),sQuery(id+"F2.wireOp",EDGE,"E7.sketch_text.stroke-82")])]});
            var Q203;
            Q203=makeQuery(id+"F4.opExtrude","SWEPT_BODY",BODY,{"disambiguationData":[OSD([sQuery(id+"F2.wireOp",EDGE,"E7.sketch_text.stroke-83"),sQuery(id+"F2.wireOp",EDGE,"E7.sketch_text.stroke-84"),sQuery(id+"F2.wireOp",EDGE,"E7.sketch_text.stroke-85"),sQuery(id+"F2.wireOp",EDGE,"E7.sketch_text.stroke-86"),sQuery(id+"F2.wireOp",EDGE,"E7.sketch_text.stroke-87"),sQuery(id+"F2.wireOp",EDGE,"E7.sketch_text.stroke-88"),sQuery(id+"F2.wireOp",EDGE,"E7.sketch_text.stroke-89"),sQuery(id+"F2.wireOp",EDGE,"E7.sketch_text.stroke-90"),sQuery(id+"F2.wireOp",EDGE,"E7.sketch_text.stroke-91"),sQuery(id+"F2.wireOp",EDGE,"E7.sketch_text.stroke-92"),sQuery(id+"F2.wireOp",EDGE,"E7.sketch_text.stroke-93"),sQuery(id+"F2.wireOp",EDGE,"E7.sketch_text.stroke-94"),sQuery(id+"F2.wireOp",EDGE,"E7.sketch_text.stroke-95"),sQuery(id+"F2.wireOp",EDGE,"E7.sketch_text.stroke-96"),sQuery(id+"F2.wireOp",EDGE,"E7.sketch_text.stroke-97"),sQuery(id+"F2.wireOp",EDGE,"E7.sketch_text.stroke-98"),sQuery(id+"F2.wireOp",EDGE,"E7.sketch_text.stroke-99"),sQuery(id+"F2.wireOp",EDGE,"E7.sketch_text.stroke-100"),sQuery(id+"F2.wireOp",EDGE,"E7.sketch_text.stroke-101")])]});
            var Q204;
            Q204=makeQuery(id+"F4.opExtrude","SWEPT_BODY",BODY,{"disambiguationData":[OSD([sQuery(id+"F2.wireOp",EDGE,"E7.sketch_text.stroke-102"),sQuery(id+"F2.wireOp",EDGE,"E7.sketch_text.stroke-103"),sQuery(id+"F2.wireOp",EDGE,"E7.sketch_text.stroke-104"),sQuery(id+"F2.wireOp",EDGE,"E7.sketch_text.stroke-105"),sQuery(id+"F2.wireOp",EDGE,"E7.sketch_text.stroke-106"),sQuery(id+"F2.wireOp",EDGE,"E7.sketch_text.stroke-107"),sQuery(id+"F2.wireOp",EDGE,"E7.sketch_text.stroke-108"),sQuery(id+"F2.wireOp",EDGE,"E7.sketch_text.stroke-109"),sQuery(id+"F2.wireOp",EDGE,"E7.sketch_text.stroke-110"),sQuery(id+"F2.wireOp",EDGE,"E7.sketch_text.stroke-111"),sQuery(id+"F2.wireOp",EDGE,"E7.sketch_text.stroke-112"),sQuery(id+"F2.wireOp",EDGE,"E7.sketch_text.stroke-113"),sQuery(id+"F2.wireOp",EDGE,"E7.sketch_text.stroke-114")])]});
            var Q205;
            Q205=makeQuery(id+"F4.opExtrude","SWEPT_BODY",BODY,{"disambiguationData":[OSD([sQuery(id+"F2.wireOp",EDGE,"E7.sketch_text.stroke-115"),sQuery(id+"F2.wireOp",EDGE,"E7.sketch_text.stroke-116"),sQuery(id+"F2.wireOp",EDGE,"E7.sketch_text.stroke-117"),sQuery(id+"F2.wireOp",EDGE,"E7.sketch_text.stroke-118"),sQuery(id+"F2.wireOp",EDGE,"E7.sketch_text.stroke-119"),sQuery(id+"F2.wireOp",EDGE,"E7.sketch_text.stroke-120"),sQuery(id+"F2.wireOp",EDGE,"E7.sketch_text.stroke-121"),sQuery(id+"F2.wireOp",EDGE,"E7.sketch_text.stroke-122"),sQuery(id+"F2.wireOp",EDGE,"E7.sketch_text.stroke-123"),sQuery(id+"F2.wireOp",EDGE,"E7.sketch_text.stroke-124"),sQuery(id+"F2.wireOp",EDGE,"E7.sketch_text.stroke-125"),sQuery(id+"F2.wireOp",EDGE,"E7.sketch_text.stroke-126"),sQuery(id+"F2.wireOp",EDGE,"E7.sketch_text.stroke-127"),sQuery(id+"F2.wireOp",EDGE,"E7.sketch_text.stroke-128"),sQuery(id+"F2.wireOp",EDGE,"E7.sketch_text.stroke-129"),sQuery(id+"F2.wireOp",EDGE,"E7.sketch_text.stroke-130"),sQuery(id+"F2.wireOp",EDGE,"E7.sketch_text.stroke-131"),sQuery(id+"F2.wireOp",EDGE,"E7.sketch_text.stroke-132"),sQuery(id+"F2.wireOp",EDGE,"E7.sketch_text.stroke-133"),sQuery(id+"F2.wireOp",EDGE,"E7.sketch_text.stroke-134"),sQuery(id+"F2.wireOp",EDGE,"E7.sketch_text.stroke-135"),sQuery(id+"F2.wireOp",EDGE,"E7.sketch_text.stroke-136"),sQuery(id+"F2.wireOp",EDGE,"E7.sketch_text.stroke-137"),sQuery(id+"F2.wireOp",EDGE,"E7.sketch_text.stroke-138"),sQuery(id+"F2.wireOp",EDGE,"E7.sketch_text.stroke-139"),sQuery(id+"F2.wireOp",EDGE,"E7.sketch_text.stroke-140"),sQuery(id+"F2.wireOp",EDGE,"E7.sketch_text.stroke-141"),sQuery(id+"F2.wireOp",EDGE,"E7.sketch_text.stroke-142")])]});
            var Q206;
            Q206=makeQuery(id+"F4.opExtrude","SWEPT_BODY",BODY,{"disambiguationData":[OSD([sQuery(id+"F2.wireOp",EDGE,"E7.sketch_text.stroke-143"),sQuery(id+"F2.wireOp",EDGE,"E7.sketch_text.stroke-144"),sQuery(id+"F2.wireOp",EDGE,"E7.sketch_text.stroke-145"),sQuery(id+"F2.wireOp",EDGE,"E7.sketch_text.stroke-146"),sQuery(id+"F2.wireOp",EDGE,"E7.sketch_text.stroke-147"),sQuery(id+"F2.wireOp",EDGE,"E7.sketch_text.stroke-148"),sQuery(id+"F2.wireOp",EDGE,"E7.sketch_text.stroke-149"),sQuery(id+"F2.wireOp",EDGE,"E7.sketch_text.stroke-150"),sQuery(id+"F2.wireOp",EDGE,"E7.sketch_text.stroke-151"),sQuery(id+"F2.wireOp",EDGE,"E7.sketch_text.stroke-152"),sQuery(id+"F2.wireOp",EDGE,"E7.sketch_text.stroke-153"),sQuery(id+"F2.wireOp",EDGE,"E7.sketch_text.stroke-154"),sQuery(id+"F2.wireOp",EDGE,"E7.sketch_text.stroke-155"),sQuery(id+"F2.wireOp",EDGE,"E7.sketch_text.stroke-156"),sQuery(id+"F2.wireOp",EDGE,"E7.sketch_text.stroke-157"),sQuery(id+"F2.wireOp",EDGE,"E7.sketch_text.stroke-158"),sQuery(id+"F2.wireOp",EDGE,"E7.sketch_text.stroke-159"),sQuery(id+"F2.wireOp",EDGE,"E7.sketch_text.stroke-160"),sQuery(id+"F2.wireOp",EDGE,"E7.sketch_text.stroke-161"),sQuery(id+"F2.wireOp",EDGE,"E7.sketch_text.stroke-162"),sQuery(id+"F2.wireOp",EDGE,"E7.sketch_text.stroke-163"),sQuery(id+"F2.wireOp",EDGE,"E7.sketch_text.stroke-164"),sQuery(id+"F2.wireOp",EDGE,"E7.sketch_text.stroke-165"),sQuery(id+"F2.wireOp",EDGE,"E7.sketch_text.stroke-166"),sQuery(id+"F2.wireOp",EDGE,"E7.sketch_text.stroke-167")])]});
            var Q207;
            Q207=makeQuery(id+"F4.opExtrude","SWEPT_BODY",BODY,{"disambiguationData":[OSD([sQuery(id+"F2.wireOp",EDGE,"E7.sketch_text.stroke-168"),sQuery(id+"F2.wireOp",EDGE,"E7.sketch_text.stroke-169"),sQuery(id+"F2.wireOp",EDGE,"E7.sketch_text.stroke-170"),sQuery(id+"F2.wireOp",EDGE,"E7.sketch_text.stroke-171"),sQuery(id+"F2.wireOp",EDGE,"E7.sketch_text.stroke-172"),sQuery(id+"F2.wireOp",EDGE,"E7.sketch_text.stroke-173"),sQuery(id+"F2.wireOp",EDGE,"E7.sketch_text.stroke-174"),sQuery(id+"F2.wireOp",EDGE,"E7.sketch_text.stroke-175"),sQuery(id+"F2.wireOp",EDGE,"E7.sketch_text.stroke-176"),sQuery(id+"F2.wireOp",EDGE,"E7.sketch_text.stroke-177"),sQuery(id+"F2.wireOp",EDGE,"E7.sketch_text.stroke-178"),sQuery(id+"F2.wireOp",EDGE,"E7.sketch_text.stroke-179"),sQuery(id+"F2.wireOp",EDGE,"E7.sketch_text.stroke-180"),sQuery(id+"F2.wireOp",EDGE,"E7.sketch_text.stroke-181"),sQuery(id+"F2.wireOp",EDGE,"E7.sketch_text.stroke-182"),sQuery(id+"F2.wireOp",EDGE,"E7.sketch_text.stroke-183"),sQuery(id+"F2.wireOp",EDGE,"E7.sketch_text.stroke-184"),sQuery(id+"F2.wireOp",EDGE,"E7.sketch_text.stroke-185"),sQuery(id+"F2.wireOp",EDGE,"E7.sketch_text.stroke-186"),sQuery(id+"F2.wireOp",EDGE,"E7.sketch_text.stroke-187"),sQuery(id+"F2.wireOp",EDGE,"E7.sketch_text.stroke-188"),sQuery(id+"F2.wireOp",EDGE,"E7.sketch_text.stroke-189"),sQuery(id+"F2.wireOp",EDGE,"E7.sketch_text.stroke-190"),sQuery(id+"F2.wireOp",EDGE,"E7.sketch_text.stroke-191")])]});
            var Q208;
            Q208=makeQuery(id+"F4.opExtrude","SWEPT_BODY",BODY,{"disambiguationData":[OSD([sQuery(id+"F2.wireOp",EDGE,"E7.sketch_text.stroke-192"),sQuery(id+"F2.wireOp",EDGE,"E7.sketch_text.stroke-193"),sQuery(id+"F2.wireOp",EDGE,"E7.sketch_text.stroke-194"),sQuery(id+"F2.wireOp",EDGE,"E7.sketch_text.stroke-195"),sQuery(id+"F2.wireOp",EDGE,"E7.sketch_text.stroke-196"),sQuery(id+"F2.wireOp",EDGE,"E7.sketch_text.stroke-197"),sQuery(id+"F2.wireOp",EDGE,"E7.sketch_text.stroke-198"),sQuery(id+"F2.wireOp",EDGE,"E7.sketch_text.stroke-199"),sQuery(id+"F2.wireOp",EDGE,"E7.sketch_text.stroke-200"),sQuery(id+"F2.wireOp",EDGE,"E7.sketch_text.stroke-201"),sQuery(id+"F2.wireOp",EDGE,"E7.sketch_text.stroke-202"),sQuery(id+"F2.wireOp",EDGE,"E7.sketch_text.stroke-203"),sQuery(id+"F2.wireOp",EDGE,"E7.sketch_text.stroke-204"),sQuery(id+"F2.wireOp",EDGE,"E7.sketch_text.stroke-205"),sQuery(id+"F2.wireOp",EDGE,"E7.sketch_text.stroke-206"),sQuery(id+"F2.wireOp",EDGE,"E7.sketch_text.stroke-207"),sQuery(id+"F2.wireOp",EDGE,"E7.sketch_text.stroke-208"),sQuery(id+"F2.wireOp",EDGE,"E7.sketch_text.stroke-209"),sQuery(id+"F2.wireOp",EDGE,"E7.sketch_text.stroke-210")])]});
            var Q209;
            Q209=makeQuery(id+"F4.opExtrude","SWEPT_BODY",BODY,{"disambiguationData":[OSD([sQuery(id+"F2.wireOp",EDGE,"E7.sketch_text.stroke-211"),sQuery(id+"F2.wireOp",EDGE,"E7.sketch_text.stroke-212"),sQuery(id+"F2.wireOp",EDGE,"E7.sketch_text.stroke-213"),sQuery(id+"F2.wireOp",EDGE,"E7.sketch_text.stroke-214"),sQuery(id+"F2.wireOp",EDGE,"E7.sketch_text.stroke-215"),sQuery(id+"F2.wireOp",EDGE,"E7.sketch_text.stroke-216"),sQuery(id+"F2.wireOp",EDGE,"E7.sketch_text.stroke-217"),sQuery(id+"F2.wireOp",EDGE,"E7.sketch_text.stroke-218"),sQuery(id+"F2.wireOp",EDGE,"E7.sketch_text.stroke-219"),sQuery(id+"F2.wireOp",EDGE,"E7.sketch_text.stroke-220"),sQuery(id+"F2.wireOp",EDGE,"E7.sketch_text.stroke-221"),sQuery(id+"F2.wireOp",EDGE,"E7.sketch_text.stroke-222"),sQuery(id+"F2.wireOp",EDGE,"E7.sketch_text.stroke-223"),sQuery(id+"F2.wireOp",EDGE,"E7.sketch_text.stroke-224"),sQuery(id+"F2.wireOp",EDGE,"E7.sketch_text.stroke-225"),sQuery(id+"F2.wireOp",EDGE,"E7.sketch_text.stroke-226"),sQuery(id+"F2.wireOp",EDGE,"E7.sketch_text.stroke-227"),sQuery(id+"F2.wireOp",EDGE,"E7.sketch_text.stroke-228"),sQuery(id+"F2.wireOp",EDGE,"E7.sketch_text.stroke-229"),sQuery(id+"F2.wireOp",EDGE,"E7.sketch_text.stroke-230"),sQuery(id+"F2.wireOp",EDGE,"E7.sketch_text.stroke-231"),sQuery(id+"F2.wireOp",EDGE,"E7.sketch_text.stroke-232"),sQuery(id+"F2.wireOp",EDGE,"E7.sketch_text.stroke-233"),sQuery(id+"F2.wireOp",EDGE,"E7.sketch_text.stroke-234"),sQuery(id+"F2.wireOp",EDGE,"E7.sketch_text.stroke-235")])]});
            var Q210;
            Q210=makeQuery(id+"F4.opExtrude","SWEPT_BODY",BODY,{"disambiguationData":[OSD([sQuery(id+"F2.wireOp",EDGE,"E7.sketch_text.stroke-236"),sQuery(id+"F2.wireOp",EDGE,"E7.sketch_text.stroke-237"),sQuery(id+"F2.wireOp",EDGE,"E7.sketch_text.stroke-238"),sQuery(id+"F2.wireOp",EDGE,"E7.sketch_text.stroke-239")])]});
            var Q211;
            Q211=makeQuery(id+"F4.opExtrude","SWEPT_BODY",BODY,{"disambiguationData":[OSD([sQuery(id+"F2.wireOp",EDGE,"E7.sketch_text.stroke-240"),sQuery(id+"F2.wireOp",EDGE,"E7.sketch_text.stroke-241"),sQuery(id+"F2.wireOp",EDGE,"E7.sketch_text.stroke-242"),sQuery(id+"F2.wireOp",EDGE,"E7.sketch_text.stroke-243"),sQuery(id+"F2.wireOp",EDGE,"E7.sketch_text.stroke-244"),sQuery(id+"F2.wireOp",EDGE,"E7.sketch_text.stroke-245"),sQuery(id+"F2.wireOp",EDGE,"E7.sketch_text.stroke-246"),sQuery(id+"F2.wireOp",EDGE,"E7.sketch_text.stroke-247")])]});
            var Q212;
            Q212=makeQuery(id+"F4.opExtrude","SWEPT_BODY",BODY,{"disambiguationData":[OSD([sQuery(id+"F2.wireOp",EDGE,"E7.sketch_text.stroke-248"),sQuery(id+"F2.wireOp",EDGE,"E7.sketch_text.stroke-249"),sQuery(id+"F2.wireOp",EDGE,"E7.sketch_text.stroke-250"),sQuery(id+"F2.wireOp",EDGE,"E7.sketch_text.stroke-251"),sQuery(id+"F2.wireOp",EDGE,"E7.sketch_text.stroke-252"),sQuery(id+"F2.wireOp",EDGE,"E7.sketch_text.stroke-253"),sQuery(id+"F2.wireOp",EDGE,"E7.sketch_text.stroke-254"),sQuery(id+"F2.wireOp",EDGE,"E7.sketch_text.stroke-255"),sQuery(id+"F2.wireOp",EDGE,"E7.sketch_text.stroke-256"),sQuery(id+"F2.wireOp",EDGE,"E7.sketch_text.stroke-257"),sQuery(id+"F2.wireOp",EDGE,"E7.sketch_text.stroke-258"),sQuery(id+"F2.wireOp",EDGE,"E7.sketch_text.stroke-259"),sQuery(id+"F2.wireOp",EDGE,"E7.sketch_text.stroke-260"),sQuery(id+"F2.wireOp",EDGE,"E7.sketch_text.stroke-261"),sQuery(id+"F2.wireOp",EDGE,"E7.sketch_text.stroke-262"),sQuery(id+"F2.wireOp",EDGE,"E7.sketch_text.stroke-263"),sQuery(id+"F2.wireOp",EDGE,"E7.sketch_text.stroke-264"),sQuery(id+"F2.wireOp",EDGE,"E7.sketch_text.stroke-265"),sQuery(id+"F2.wireOp",EDGE,"E7.sketch_text.stroke-266"),sQuery(id+"F2.wireOp",EDGE,"E7.sketch_text.stroke-267"),sQuery(id+"F2.wireOp",EDGE,"E7.sketch_text.stroke-268"),sQuery(id+"F2.wireOp",EDGE,"E7.sketch_text.stroke-269"),sQuery(id+"F2.wireOp",EDGE,"E7.sketch_text.stroke-270"),sQuery(id+"F2.wireOp",EDGE,"E7.sketch_text.stroke-271"),sQuery(id+"F2.wireOp",EDGE,"E7.sketch_text.stroke-272"),sQuery(id+"F2.wireOp",EDGE,"E7.sketch_text.stroke-273"),sQuery(id+"F2.wireOp",EDGE,"E7.sketch_text.stroke-274"),sQuery(id+"F2.wireOp",EDGE,"E7.sketch_text.stroke-275"),sQuery(id+"F2.wireOp",EDGE,"E7.sketch_text.stroke-276"),sQuery(id+"F2.wireOp",EDGE,"E7.sketch_text.stroke-277"),sQuery(id+"F2.wireOp",EDGE,"E7.sketch_text.stroke-278"),sQuery(id+"F2.wireOp",EDGE,"E7.sketch_text.stroke-279"),sQuery(id+"F2.wireOp",EDGE,"E7.sketch_text.stroke-280"),sQuery(id+"F2.wireOp",EDGE,"E7.sketch_text.stroke-281"),sQuery(id+"F2.wireOp",EDGE,"E7.sketch_text.stroke-282"),sQuery(id+"F2.wireOp",EDGE,"E7.sketch_text.stroke-283"),sQuery(id+"F2.wireOp",EDGE,"E7.sketch_text.stroke-284"),sQuery(id+"F2.wireOp",EDGE,"E7.sketch_text.stroke-285"),sQuery(id+"F2.wireOp",EDGE,"E7.sketch_text.stroke-286"),sQuery(id+"F2.wireOp",EDGE,"E7.sketch_text.stroke-287"),sQuery(id+"F2.wireOp",EDGE,"E7.sketch_text.stroke-288"),sQuery(id+"F2.wireOp",EDGE,"E7.sketch_text.stroke-289"),sQuery(id+"F2.wireOp",EDGE,"E7.sketch_text.stroke-290"),sQuery(id+"F2.wireOp",EDGE,"E7.sketch_text.stroke-291")])]});
            var Q213;
            Q213=makeQuery(id+"F4.opExtrude","SWEPT_BODY",BODY,{"disambiguationData":[OSD([sQuery(id+"F2.wireOp",EDGE,"E7.sketch_text.stroke-292"),sQuery(id+"F2.wireOp",EDGE,"E7.sketch_text.stroke-293"),sQuery(id+"F2.wireOp",EDGE,"E7.sketch_text.stroke-294"),sQuery(id+"F2.wireOp",EDGE,"E7.sketch_text.stroke-295"),sQuery(id+"F2.wireOp",EDGE,"E7.sketch_text.stroke-296"),sQuery(id+"F2.wireOp",EDGE,"E7.sketch_text.stroke-297"),sQuery(id+"F2.wireOp",EDGE,"E7.sketch_text.stroke-298"),sQuery(id+"F2.wireOp",EDGE,"E7.sketch_text.stroke-299"),sQuery(id+"F2.wireOp",EDGE,"E7.sketch_text.stroke-300"),sQuery(id+"F2.wireOp",EDGE,"E7.sketch_text.stroke-301"),sQuery(id+"F2.wireOp",EDGE,"E7.sketch_text.stroke-302"),sQuery(id+"F2.wireOp",EDGE,"E7.sketch_text.stroke-303"),sQuery(id+"F2.wireOp",EDGE,"E7.sketch_text.stroke-304"),sQuery(id+"F2.wireOp",EDGE,"E7.sketch_text.stroke-305"),sQuery(id+"F2.wireOp",EDGE,"E7.sketch_text.stroke-306"),sQuery(id+"F2.wireOp",EDGE,"E7.sketch_text.stroke-307"),sQuery(id+"F2.wireOp",EDGE,"E7.sketch_text.stroke-308")])]});
            var Q214;
            Q214=makeQuery(id+"F4.opExtrude","SWEPT_BODY",BODY,{"disambiguationData":[OSD([sQuery(id+"F2.wireOp",EDGE,"E7.sketch_text.stroke-309"),sQuery(id+"F2.wireOp",EDGE,"E7.sketch_text.stroke-310"),sQuery(id+"F2.wireOp",EDGE,"E7.sketch_text.stroke-311"),sQuery(id+"F2.wireOp",EDGE,"E7.sketch_text.stroke-312"),sQuery(id+"F2.wireOp",EDGE,"E7.sketch_text.stroke-313"),sQuery(id+"F2.wireOp",EDGE,"E7.sketch_text.stroke-314"),sQuery(id+"F2.wireOp",EDGE,"E7.sketch_text.stroke-315"),sQuery(id+"F2.wireOp",EDGE,"E7.sketch_text.stroke-316"),sQuery(id+"F2.wireOp",EDGE,"E7.sketch_text.stroke-317"),sQuery(id+"F2.wireOp",EDGE,"E7.sketch_text.stroke-318"),sQuery(id+"F2.wireOp",EDGE,"E7.sketch_text.stroke-319"),sQuery(id+"F2.wireOp",EDGE,"E7.sketch_text.stroke-320"),sQuery(id+"F2.wireOp",EDGE,"E7.sketch_text.stroke-321"),sQuery(id+"F2.wireOp",EDGE,"E7.sketch_text.stroke-322"),sQuery(id+"F2.wireOp",EDGE,"E7.sketch_text.stroke-323"),sQuery(id+"F2.wireOp",EDGE,"E7.sketch_text.stroke-324"),sQuery(id+"F2.wireOp",EDGE,"E7.sketch_text.stroke-325"),sQuery(id+"F2.wireOp",EDGE,"E7.sketch_text.stroke-326"),sQuery(id+"F2.wireOp",EDGE,"E7.sketch_text.stroke-327")])]});
            var Q215;
            Q215=makeQuery(id+"F4.opExtrude","SWEPT_BODY",BODY,{"disambiguationData":[OSD([sQuery(id+"F2.wireOp",EDGE,"E7.sketch_text.stroke-328"),sQuery(id+"F2.wireOp",EDGE,"E7.sketch_text.stroke-329"),sQuery(id+"F2.wireOp",EDGE,"E7.sketch_text.stroke-330"),sQuery(id+"F2.wireOp",EDGE,"E7.sketch_text.stroke-331"),sQuery(id+"F2.wireOp",EDGE,"E7.sketch_text.stroke-332"),sQuery(id+"F2.wireOp",EDGE,"E7.sketch_text.stroke-333"),sQuery(id+"F2.wireOp",EDGE,"E7.sketch_text.stroke-334"),sQuery(id+"F2.wireOp",EDGE,"E7.sketch_text.stroke-335"),sQuery(id+"F2.wireOp",EDGE,"E7.sketch_text.stroke-336"),sQuery(id+"F2.wireOp",EDGE,"E7.sketch_text.stroke-337"),sQuery(id+"F2.wireOp",EDGE,"E7.sketch_text.stroke-338"),sQuery(id+"F2.wireOp",EDGE,"E7.sketch_text.stroke-339"),sQuery(id+"F2.wireOp",EDGE,"E7.sketch_text.stroke-340"),sQuery(id+"F2.wireOp",EDGE,"E7.sketch_text.stroke-341"),sQuery(id+"F2.wireOp",EDGE,"E7.sketch_text.stroke-342"),sQuery(id+"F2.wireOp",EDGE,"E7.sketch_text.stroke-343"),sQuery(id+"F2.wireOp",EDGE,"E7.sketch_text.stroke-344"),sQuery(id+"F2.wireOp",EDGE,"E7.sketch_text.stroke-345"),sQuery(id+"F2.wireOp",EDGE,"E7.sketch_text.stroke-346"),sQuery(id+"F2.wireOp",EDGE,"E7.sketch_text.stroke-347"),sQuery(id+"F2.wireOp",EDGE,"E7.sketch_text.stroke-348"),sQuery(id+"F2.wireOp",EDGE,"E7.sketch_text.stroke-349"),sQuery(id+"F2.wireOp",EDGE,"E7.sketch_text.stroke-350"),sQuery(id+"F2.wireOp",EDGE,"E7.sketch_text.stroke-351")])]});
            var Q216;
            Q216=makeQuery(id+"F4.opExtrude","SWEPT_BODY",BODY,{"disambiguationData":[OSD([sQuery(id+"F2.wireOp",EDGE,"E7.sketch_text.stroke-352"),sQuery(id+"F2.wireOp",EDGE,"E7.sketch_text.stroke-353"),sQuery(id+"F2.wireOp",EDGE,"E7.sketch_text.stroke-354"),sQuery(id+"F2.wireOp",EDGE,"E7.sketch_text.stroke-355"),sQuery(id+"F2.wireOp",EDGE,"E7.sketch_text.stroke-356"),sQuery(id+"F2.wireOp",EDGE,"E7.sketch_text.stroke-357"),sQuery(id+"F2.wireOp",EDGE,"E7.sketch_text.stroke-358"),sQuery(id+"F2.wireOp",EDGE,"E7.sketch_text.stroke-359"),sQuery(id+"F2.wireOp",EDGE,"E7.sketch_text.stroke-360"),sQuery(id+"F2.wireOp",EDGE,"E7.sketch_text.stroke-361"),sQuery(id+"F2.wireOp",EDGE,"E7.sketch_text.stroke-362"),sQuery(id+"F2.wireOp",EDGE,"E7.sketch_text.stroke-363"),sQuery(id+"F2.wireOp",EDGE,"E7.sketch_text.stroke-364"),sQuery(id+"F2.wireOp",EDGE,"E7.sketch_text.stroke-365"),sQuery(id+"F2.wireOp",EDGE,"E7.sketch_text.stroke-366"),sQuery(id+"F2.wireOp",EDGE,"E7.sketch_text.stroke-367"),sQuery(id+"F2.wireOp",EDGE,"E7.sketch_text.stroke-368"),sQuery(id+"F2.wireOp",EDGE,"E7.sketch_text.stroke-369"),sQuery(id+"F2.wireOp",EDGE,"E7.sketch_text.stroke-370"),sQuery(id+"F2.wireOp",EDGE,"E7.sketch_text.stroke-371"),sQuery(id+"F2.wireOp",EDGE,"E7.sketch_text.stroke-372"),sQuery(id+"F2.wireOp",EDGE,"E7.sketch_text.stroke-373"),sQuery(id+"F2.wireOp",EDGE,"E7.sketch_text.stroke-374")])]});
            var Q217;
            Q217=makeQuery(id+"F4.opExtrude","SWEPT_BODY",BODY,{"disambiguationData":[OSD([sQuery(id+"F2.wireOp",EDGE,"E7.sketch_text.stroke-375"),sQuery(id+"F2.wireOp",EDGE,"E7.sketch_text.stroke-376"),sQuery(id+"F2.wireOp",EDGE,"E7.sketch_text.stroke-377"),sQuery(id+"F2.wireOp",EDGE,"E7.sketch_text.stroke-378"),sQuery(id+"F2.wireOp",EDGE,"E7.sketch_text.stroke-379"),sQuery(id+"F2.wireOp",EDGE,"E7.sketch_text.stroke-380"),sQuery(id+"F2.wireOp",EDGE,"E7.sketch_text.stroke-381"),sQuery(id+"F2.wireOp",EDGE,"E7.sketch_text.stroke-382"),sQuery(id+"F2.wireOp",EDGE,"E7.sketch_text.stroke-383"),sQuery(id+"F2.wireOp",EDGE,"E7.sketch_text.stroke-384"),sQuery(id+"F2.wireOp",EDGE,"E7.sketch_text.stroke-385"),sQuery(id+"F2.wireOp",EDGE,"E7.sketch_text.stroke-386"),sQuery(id+"F2.wireOp",EDGE,"E7.sketch_text.stroke-387"),sQuery(id+"F2.wireOp",EDGE,"E7.sketch_text.stroke-388"),sQuery(id+"F2.wireOp",EDGE,"E7.sketch_text.stroke-389"),sQuery(id+"F2.wireOp",EDGE,"E7.sketch_text.stroke-390")])]});
            var Q218;
            Q218=makeQuery(id+"F4.opExtrude","SWEPT_BODY",BODY,{"disambiguationData":[OSD([sQuery(id+"F2.wireOp",EDGE,"E7.sketch_text.stroke-391"),sQuery(id+"F2.wireOp",EDGE,"E7.sketch_text.stroke-392"),sQuery(id+"F2.wireOp",EDGE,"E7.sketch_text.stroke-393"),sQuery(id+"F2.wireOp",EDGE,"E7.sketch_text.stroke-394"),sQuery(id+"F2.wireOp",EDGE,"E7.sketch_text.stroke-395"),sQuery(id+"F2.wireOp",EDGE,"E7.sketch_text.stroke-396"),sQuery(id+"F2.wireOp",EDGE,"E7.sketch_text.stroke-397"),sQuery(id+"F2.wireOp",EDGE,"E7.sketch_text.stroke-398"),sQuery(id+"F2.wireOp",EDGE,"E7.sketch_text.stroke-399"),sQuery(id+"F2.wireOp",EDGE,"E7.sketch_text.stroke-400"),sQuery(id+"F2.wireOp",EDGE,"E7.sketch_text.stroke-401"),sQuery(id+"F2.wireOp",EDGE,"E7.sketch_text.stroke-402")])]});
            var Q219;
            Q219=makeQuery(id+"F4.opExtrude","SWEPT_BODY",BODY,{"disambiguationData":[OSD([sQuery(id+"F2.wireOp",EDGE,"E7.sketch_text.stroke-403"),sQuery(id+"F2.wireOp",EDGE,"E7.sketch_text.stroke-404"),sQuery(id+"F2.wireOp",EDGE,"E7.sketch_text.stroke-405"),sQuery(id+"F2.wireOp",EDGE,"E7.sketch_text.stroke-406"),sQuery(id+"F2.wireOp",EDGE,"E7.sketch_text.stroke-407"),sQuery(id+"F2.wireOp",EDGE,"E7.sketch_text.stroke-408"),sQuery(id+"F2.wireOp",EDGE,"E7.sketch_text.stroke-409"),sQuery(id+"F2.wireOp",EDGE,"E7.sketch_text.stroke-410"),sQuery(id+"F2.wireOp",EDGE,"E7.sketch_text.stroke-411"),sQuery(id+"F2.wireOp",EDGE,"E7.sketch_text.stroke-412"),sQuery(id+"F2.wireOp",EDGE,"E7.sketch_text.stroke-413"),sQuery(id+"F2.wireOp",EDGE,"E7.sketch_text.stroke-414"),sQuery(id+"F2.wireOp",EDGE,"E7.sketch_text.stroke-415"),sQuery(id+"F2.wireOp",EDGE,"E7.sketch_text.stroke-416"),sQuery(id+"F2.wireOp",EDGE,"E7.sketch_text.stroke-417"),sQuery(id+"F2.wireOp",EDGE,"E7.sketch_text.stroke-418"),sQuery(id+"F2.wireOp",EDGE,"E7.sketch_text.stroke-419")])]});
            var Q220;
            Q220=makeQuery(id+"F4.opExtrude","SWEPT_BODY",BODY,{"disambiguationData":[OSD([sQuery(id+"F2.wireOp",EDGE,"E7.sketch_text.stroke-420"),sQuery(id+"F2.wireOp",EDGE,"E7.sketch_text.stroke-421"),sQuery(id+"F2.wireOp",EDGE,"E7.sketch_text.stroke-422"),sQuery(id+"F2.wireOp",EDGE,"E7.sketch_text.stroke-423")])]});
            var Q221;
            Q221=makeQuery(id+"F4.opExtrude","SWEPT_BODY",BODY,{"disambiguationData":[OSD([sQuery(id+"F2.wireOp",EDGE,"E7.sketch_text.stroke-424"),sQuery(id+"F2.wireOp",EDGE,"E7.sketch_text.stroke-425"),sQuery(id+"F2.wireOp",EDGE,"E7.sketch_text.stroke-426"),sQuery(id+"F2.wireOp",EDGE,"E7.sketch_text.stroke-427"),sQuery(id+"F2.wireOp",EDGE,"E7.sketch_text.stroke-428"),sQuery(id+"F2.wireOp",EDGE,"E7.sketch_text.stroke-429"),sQuery(id+"F2.wireOp",EDGE,"E7.sketch_text.stroke-430"),sQuery(id+"F2.wireOp",EDGE,"E7.sketch_text.stroke-431"),sQuery(id+"F2.wireOp",EDGE,"E7.sketch_text.stroke-432"),sQuery(id+"F2.wireOp",EDGE,"E7.sketch_text.stroke-433"),sQuery(id+"F2.wireOp",EDGE,"E7.sketch_text.stroke-434"),sQuery(id+"F2.wireOp",EDGE,"E7.sketch_text.stroke-435"),sQuery(id+"F2.wireOp",EDGE,"E7.sketch_text.stroke-436"),sQuery(id+"F2.wireOp",EDGE,"E7.sketch_text.stroke-437"),sQuery(id+"F2.wireOp",EDGE,"E7.sketch_text.stroke-438"),sQuery(id+"F2.wireOp",EDGE,"E7.sketch_text.stroke-439"),sQuery(id+"F2.wireOp",EDGE,"E7.sketch_text.stroke-440"),sQuery(id+"F2.wireOp",EDGE,"E7.sketch_text.stroke-441"),sQuery(id+"F2.wireOp",EDGE,"E7.sketch_text.stroke-442"),sQuery(id+"F2.wireOp",EDGE,"E7.sketch_text.stroke-443"),sQuery(id+"F2.wireOp",EDGE,"E7.sketch_text.stroke-444"),sQuery(id+"F2.wireOp",EDGE,"E7.sketch_text.stroke-445"),sQuery(id+"F2.wireOp",EDGE,"E7.sketch_text.stroke-446"),sQuery(id+"F2.wireOp",EDGE,"E7.sketch_text.stroke-447"),sQuery(id+"F2.wireOp",EDGE,"E7.sketch_text.stroke-448"),sQuery(id+"F2.wireOp",EDGE,"E7.sketch_text.stroke-449"),sQuery(id+"F2.wireOp",EDGE,"E7.sketch_text.stroke-450"),sQuery(id+"F2.wireOp",EDGE,"E7.sketch_text.stroke-451")])]});
            var Q222;
            Q222=makeQuery(id+"F4.opExtrude","SWEPT_BODY",BODY,{"disambiguationData":[OSD([sQuery(id+"F2.wireOp",EDGE,"E7.sketch_text.stroke-452"),sQuery(id+"F2.wireOp",EDGE,"E7.sketch_text.stroke-453"),sQuery(id+"F2.wireOp",EDGE,"E7.sketch_text.stroke-454"),sQuery(id+"F2.wireOp",EDGE,"E7.sketch_text.stroke-455"),sQuery(id+"F2.wireOp",EDGE,"E7.sketch_text.stroke-456"),sQuery(id+"F2.wireOp",EDGE,"E7.sketch_text.stroke-457"),sQuery(id+"F2.wireOp",EDGE,"E7.sketch_text.stroke-458"),sQuery(id+"F2.wireOp",EDGE,"E7.sketch_text.stroke-459"),sQuery(id+"F2.wireOp",EDGE,"E7.sketch_text.stroke-460"),sQuery(id+"F2.wireOp",EDGE,"E7.sketch_text.stroke-461"),sQuery(id+"F2.wireOp",EDGE,"E7.sketch_text.stroke-462"),sQuery(id+"F2.wireOp",EDGE,"E7.sketch_text.stroke-463"),sQuery(id+"F2.wireOp",EDGE,"E7.sketch_text.stroke-464"),sQuery(id+"F2.wireOp",EDGE,"E7.sketch_text.stroke-465"),sQuery(id+"F2.wireOp",EDGE,"E7.sketch_text.stroke-466"),sQuery(id+"F2.wireOp",EDGE,"E7.sketch_text.stroke-467"),sQuery(id+"F2.wireOp",EDGE,"E7.sketch_text.stroke-468"),sQuery(id+"F2.wireOp",EDGE,"E7.sketch_text.stroke-469"),sQuery(id+"F2.wireOp",EDGE,"E7.sketch_text.stroke-470"),sQuery(id+"F2.wireOp",EDGE,"E7.sketch_text.stroke-471"),sQuery(id+"F2.wireOp",EDGE,"E7.sketch_text.stroke-472"),sQuery(id+"F2.wireOp",EDGE,"E7.sketch_text.stroke-473"),sQuery(id+"F2.wireOp",EDGE,"E7.sketch_text.stroke-474"),sQuery(id+"F2.wireOp",EDGE,"E7.sketch_text.stroke-475"),sQuery(id+"F2.wireOp",EDGE,"E7.sketch_text.stroke-476"),sQuery(id+"F2.wireOp",EDGE,"E7.sketch_text.stroke-477"),sQuery(id+"F2.wireOp",EDGE,"E7.sketch_text.stroke-478")])]});
            var Q223;
            Q223=makeQuery(id+"F4.opExtrude","SWEPT_BODY",BODY,{"disambiguationData":[OSD([sQuery(id+"F2.wireOp",EDGE,"E7.sketch_text.stroke-479"),sQuery(id+"F2.wireOp",EDGE,"E7.sketch_text.stroke-480"),sQuery(id+"F2.wireOp",EDGE,"E7.sketch_text.stroke-481"),sQuery(id+"F2.wireOp",EDGE,"E7.sketch_text.stroke-482"),sQuery(id+"F2.wireOp",EDGE,"E7.sketch_text.stroke-483"),sQuery(id+"F2.wireOp",EDGE,"E7.sketch_text.stroke-484"),sQuery(id+"F2.wireOp",EDGE,"E7.sketch_text.stroke-485"),sQuery(id+"F2.wireOp",EDGE,"E7.sketch_text.stroke-486"),sQuery(id+"F2.wireOp",EDGE,"E7.sketch_text.stroke-487"),sQuery(id+"F2.wireOp",EDGE,"E7.sketch_text.stroke-488"),sQuery(id+"F2.wireOp",EDGE,"E7.sketch_text.stroke-489"),sQuery(id+"F2.wireOp",EDGE,"E7.sketch_text.stroke-490"),sQuery(id+"F2.wireOp",EDGE,"E7.sketch_text.stroke-491"),sQuery(id+"F2.wireOp",EDGE,"E7.sketch_text.stroke-492"),sQuery(id+"F2.wireOp",EDGE,"E7.sketch_text.stroke-493"),sQuery(id+"F2.wireOp",EDGE,"E7.sketch_text.stroke-494"),sQuery(id+"F2.wireOp",EDGE,"E7.sketch_text.stroke-495")])]});
            var Q224;
            Q224=makeQuery(id+"F4.opExtrude","SWEPT_BODY",BODY,{"disambiguationData":[OSD([sQuery(id+"F2.wireOp",EDGE,"E7.sketch_text.stroke-496"),sQuery(id+"F2.wireOp",EDGE,"E7.sketch_text.stroke-497"),sQuery(id+"F2.wireOp",EDGE,"E7.sketch_text.stroke-498"),sQuery(id+"F2.wireOp",EDGE,"E7.sketch_text.stroke-499"),sQuery(id+"F2.wireOp",EDGE,"E7.sketch_text.stroke-500"),sQuery(id+"F2.wireOp",EDGE,"E7.sketch_text.stroke-501"),sQuery(id+"F2.wireOp",EDGE,"E7.sketch_text.stroke-502"),sQuery(id+"F2.wireOp",EDGE,"E7.sketch_text.stroke-503"),sQuery(id+"F2.wireOp",EDGE,"E7.sketch_text.stroke-504"),sQuery(id+"F2.wireOp",EDGE,"E7.sketch_text.stroke-505"),sQuery(id+"F2.wireOp",EDGE,"E7.sketch_text.stroke-506"),sQuery(id+"F2.wireOp",EDGE,"E7.sketch_text.stroke-507"),sQuery(id+"F2.wireOp",EDGE,"E7.sketch_text.stroke-508"),sQuery(id+"F2.wireOp",EDGE,"E7.sketch_text.stroke-509"),sQuery(id+"F2.wireOp",EDGE,"E7.sketch_text.stroke-510"),sQuery(id+"F2.wireOp",EDGE,"E7.sketch_text.stroke-511"),sQuery(id+"F2.wireOp",EDGE,"E7.sketch_text.stroke-512"),sQuery(id+"F2.wireOp",EDGE,"E7.sketch_text.stroke-513"),sQuery(id+"F2.wireOp",EDGE,"E7.sketch_text.stroke-514"),sQuery(id+"F2.wireOp",EDGE,"E7.sketch_text.stroke-515"),sQuery(id+"F2.wireOp",EDGE,"E7.sketch_text.stroke-516"),sQuery(id+"F2.wireOp",EDGE,"E7.sketch_text.stroke-517"),sQuery(id+"F2.wireOp",EDGE,"E7.sketch_text.stroke-518"),sQuery(id+"F2.wireOp",EDGE,"E7.sketch_text.stroke-519"),sQuery(id+"F2.wireOp",EDGE,"E7.sketch_text.stroke-520"),sQuery(id+"F2.wireOp",EDGE,"E7.sketch_text.stroke-521"),sQuery(id+"F2.wireOp",EDGE,"E7.sketch_text.stroke-522")])]});
            var Q225;
            Q225=makeQuery(id+"F1.opExtrude","SWEPT_BODY",BODY,{"disambiguationData":[OSD([sQuery(id+"F0.wireOp",EDGE,"E0.bottom"),sQuery(id+"F0.wireOp",EDGE,"E0.top"),sQuery(id+"F0.wireOp",EDGE,"E0.left"),sQuery(id+"F0.wireOp",EDGE,"E0.right")])]});
            booleanBodies(context, id + "F5", {"operationType" : BooleanOperationType.SUBTRACTION, "tools" : qUnion([Q0, Q1, Q2, Q3, Q4, Q5, Q6, Q7, Q8, Q9, Q10, Q11, Q12, Q13, Q14, Q15, Q16, Q17, Q18, Q19, Q20, Q21, Q22, Q23, Q24, Q25, Q26, Q27, Q28, Q29, Q30, Q31, Q32, Q33, Q34, Q35, Q36, Q37, Q38, Q39, Q40, Q41, Q42, Q43, Q44, Q45, Q46, Q47, Q48, Q49, Q50, Q51, Q52, Q53, Q54, Q55, Q56, Q57, Q58, Q59, Q60, Q61, Q62, Q63, Q64, Q65, Q66, Q67, Q68, Q69, Q70, Q71, Q72, Q73, Q74, Q75, Q76, Q77, Q78, Q79, Q80, Q81, Q82, Q83, Q84, Q85, Q86, Q87, Q88, Q89, Q90, Q91, Q92, Q93, Q94, Q95, Q96, Q97, Q98, Q99, Q100, Q101, Q102, Q103, Q104, Q105, Q106, Q107, Q108, Q109, Q110, Q111, Q112, Q113, Q114, Q115, Q116, Q117, Q118, Q119, Q120, Q121, Q122, Q123, Q124, Q125, Q126, Q127, Q128, Q129, Q130, Q131, Q132, Q133, Q134, Q135, Q136, Q137, Q138, Q139, Q140, Q141, Q142, Q143, Q144, Q145, Q146, Q147, Q148, Q149, Q150, Q151, Q152, Q153, Q154, Q155, Q156, Q157, Q158, Q159, Q160, Q161, Q162, Q163, Q164, Q165, Q166, Q167, Q168, Q169, Q170, Q171, Q172, Q173, Q174, Q175, Q176, Q177, Q178, Q179, Q180, Q181, Q182, Q183, Q184, Q185, Q186, Q187, Q188, Q189, Q190, Q191, Q192, Q193, Q194, Q195, Q196, Q197, Q198, Q199, Q200, Q201, Q202, Q203, Q204, Q205, Q206, Q207, Q208, Q209, Q210, Q211, Q212, Q213, Q214, Q215, Q216, Q217, Q218, Q219, Q220, Q221, Q222, Q223, Q224]), "targets" : qUnion([Q225]), "keepTools" : true});
        }
    });